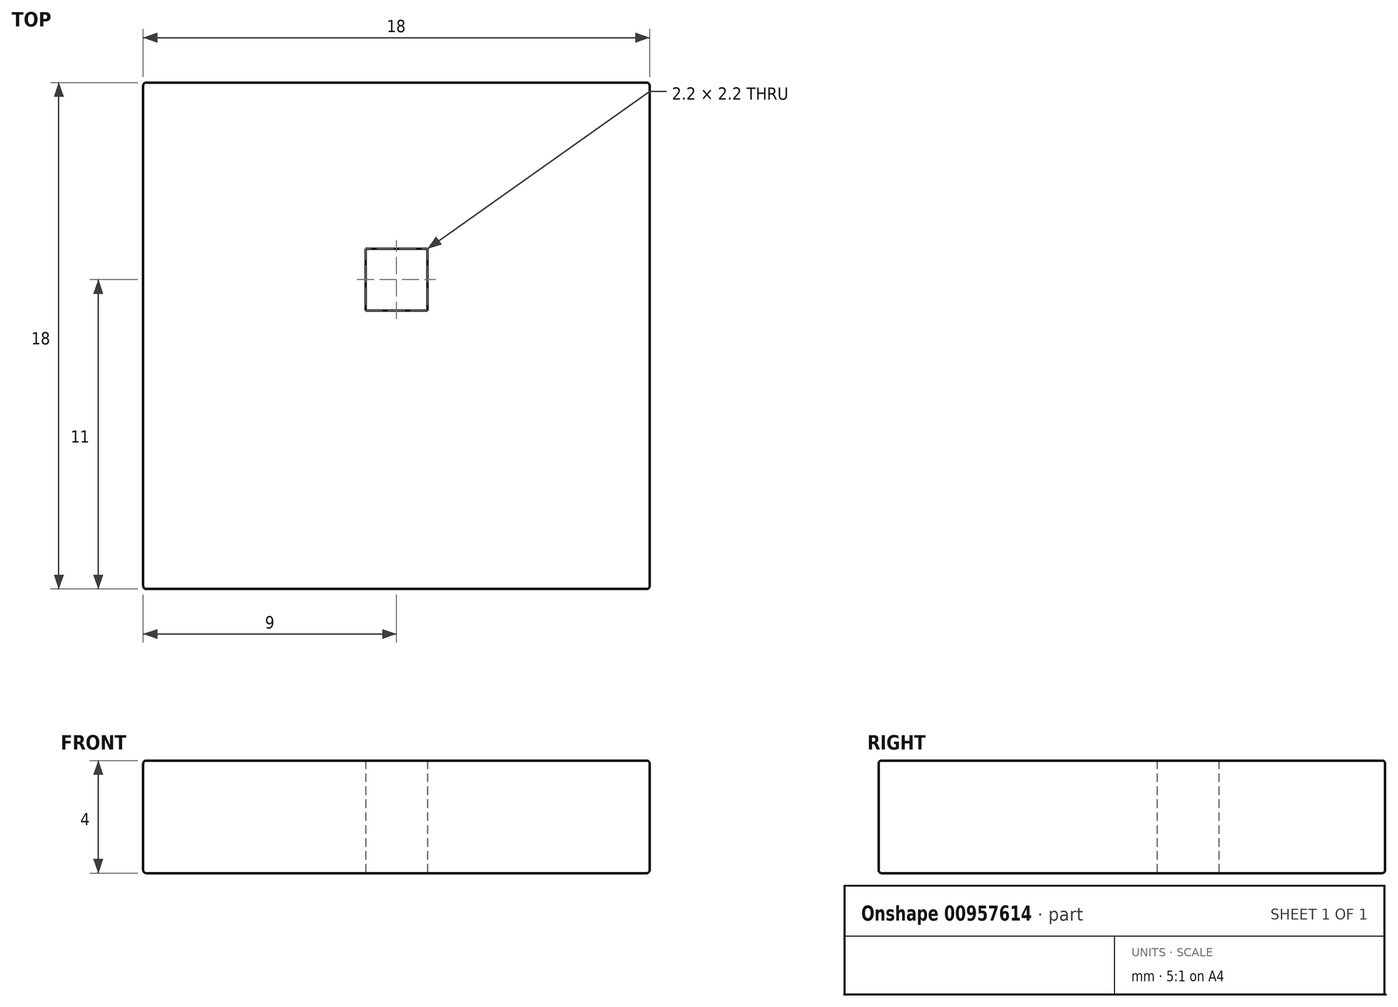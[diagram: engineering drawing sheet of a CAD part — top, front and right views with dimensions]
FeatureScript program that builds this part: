
annotation { "Feature Type Name" : "Feature", "Feature Type Description" : "" }
export const myFeature = defineFeature(function(context is Context, id is Id, definition is map)
    precondition{}
    {
        {
            var Q0;
            Q0=qCreatedBy(makeId("Top.planeOp"),FACE);
            var sketch = newSketch(context, id + "F0", { "sketchPlane" : qUnion([Q0])});
            skLineSegment(sketch, "E0.bottom", {"start": v(-9, 9) * mm, "end": v(9, 9) * mm});
            skLineSegment(sketch, "E0.top", {"start": v(-9, -9) * mm, "end": v(9, -9) * mm});
            skLineSegment(sketch, "E0.left", {"start": v(-9, 9) * mm, "end": v(-9, -9) * mm});
            skLineSegment(sketch, "E0.right", {"start": v(9, 9) * mm, "end": v(9, -9) * mm});
            skPoint(sketch, "E0.middle", {"position": v(0, 0) * mm});
            skLineSegment(sketch, "E1", {"start": v(-8, 9) * mm, "end": v(-8, -9) * mm});
            skLineSegment(sketch, "E2", {"start": v(-7.1, 9) * mm, "end": v(-7.1, -9) * mm});
            skLineSegment(sketch, "E3", {"start": v(-6.9, 9) * mm, "end": v(-6.9, -9) * mm});
            skLineSegment(sketch, "E4", {"start": v(-5.1, 9) * mm, "end": v(-5.1, -9) * mm});
            skLineSegment(sketch, "E5", {"start": v(-4.9, 9) * mm, "end": v(-4.9, -9) * mm});
            skLineSegment(sketch, "E6", {"start": v(-3.1, 9) * mm, "end": v(-3.1, -9) * mm});
            skLineSegment(sketch, "E7", {"start": v(-2.9, 9) * mm, "end": v(-2.9, -9) * mm});
            skLineSegment(sketch, "E8", {"start": v(-1.1, 9) * mm, "end": v(-1.1, -9) * mm});
            skLineSegment(sketch, "E9", {"start": v(-0.9, 9) * mm, "end": v(-0.9, -9) * mm});
            skLineSegment(sketch, "E10", {"start": v(0.9, 9) * mm, "end": v(0.9, -9) * mm});
            skLineSegment(sketch, "E11", {"start": v(1.1, 9) * mm, "end": v(1.1, -9) * mm});
            skLineSegment(sketch, "E12", {"start": v(2.9, 9) * mm, "end": v(2.9, -9) * mm});
            skLineSegment(sketch, "E13", {"start": v(3.1, 9) * mm, "end": v(3.1, -9) * mm});
            skLineSegment(sketch, "E14", {"start": v(4.9, 9) * mm, "end": v(4.9, -9) * mm});
            skLineSegment(sketch, "E15", {"start": v(5.1, 9) * mm, "end": v(5.1, -9) * mm});
            skLineSegment(sketch, "E16", {"start": v(6.9, 9) * mm, "end": v(6.9, -9) * mm});
            skLineSegment(sketch, "E17", {"start": v(7.1, 9) * mm, "end": v(7.1, -9) * mm});
            skLineSegment(sketch, "E18", {"start": v(8, 9) * mm, "end": v(8, -9) * mm});
            skLineSegment(sketch, "E19", {"start": v(9, 8) * mm, "end": v(-9, 8) * mm});
            skLineSegment(sketch, "E20", {"start": v(9, 7.1) * mm, "end": v(-9, 7.1) * mm});
            skLineSegment(sketch, "E21", {"start": v(9, 6.9) * mm, "end": v(-9, 6.9) * mm});
            skLineSegment(sketch, "E22", {"start": v(9, 5.1) * mm, "end": v(-9, 5.1) * mm});
            skLineSegment(sketch, "E23", {"start": v(9, 4.9) * mm, "end": v(-9, 4.9) * mm});
            skLineSegment(sketch, "E24", {"start": v(9, 3.1) * mm, "end": v(-9, 3.1) * mm});
            skLineSegment(sketch, "E25", {"start": v(9, 2.9) * mm, "end": v(-9, 2.9) * mm});
            skLineSegment(sketch, "E26", {"start": v(9, 1.1) * mm, "end": v(-9, 1.1) * mm});
            skLineSegment(sketch, "E27", {"start": v(9, 0.9) * mm, "end": v(-9, 0.9) * mm});
            skLineSegment(sketch, "E28", {"start": v(9, -0.9) * mm, "end": v(-9, -0.9) * mm});
            skLineSegment(sketch, "E29", {"start": v(9, -1.1) * mm, "end": v(-9, -1.1) * mm});
            skLineSegment(sketch, "E30", {"start": v(9, -2.9) * mm, "end": v(-9, -2.9) * mm});
            skLineSegment(sketch, "E31", {"start": v(9, -3.1) * mm, "end": v(-9, -3.1) * mm});
            skLineSegment(sketch, "E32", {"start": v(9, -4.9) * mm, "end": v(-9, -4.9) * mm});
            skLineSegment(sketch, "E33", {"start": v(9, -5.1) * mm, "end": v(-9, -5.1) * mm});
            skLineSegment(sketch, "E34", {"start": v(9, -6.9) * mm, "end": v(-9, -6.9) * mm});
            skLineSegment(sketch, "E35", {"start": v(9, -7.1) * mm, "end": v(-9, -7.1) * mm});
            skLineSegment(sketch, "E36", {"start": v(9, -8) * mm, "end": v(-9, -8) * mm});
            skSolve(sketch);
        }
        {
            var Q0;
            {var subQ0=sQuery(id+"F0.wireOp",EDGE,"E30");var subQ1=sQuery(id+"F0.wireOp",EDGE,"E10");var subQ2=makeQuery(id+"F0.imprint","INTERSECT",VERTEX,{"derivedFrom":[subQ1,subQ0]});Q0=makeQuery(id+"F0.imprint","IMPRINT",FACE,{"disambiguationData":[TD([[makeQuery(id+"F0.imprint","IMPRINT",EDGE,{"disambiguationData":[TD([[subQ2,-1.0]])],"derivedFrom":subQ1}),1.0]])]});}
            var Q1;
            {var subQ0=sQuery(id+"F0.wireOp",EDGE,"E26");var subQ1=sQuery(id+"F0.wireOp",EDGE,"E11");var subQ2=makeQuery(id+"F0.imprint","INTERSECT",VERTEX,{"derivedFrom":[subQ1,subQ0]});Q1=makeQuery(id+"F0.imprint","IMPRINT",FACE,{"disambiguationData":[TD([[makeQuery(id+"F0.imprint","IMPRINT",EDGE,{"disambiguationData":[TD([[subQ2,-1.0]])],"derivedFrom":subQ1}),1.0]])]});}
            var Q2;
            {var subQ0=sQuery(id+"F0.wireOp",EDGE,"E30");var subQ1=sQuery(id+"F0.wireOp",EDGE,"E15");var subQ2=makeQuery(id+"F0.imprint","INTERSECT",VERTEX,{"derivedFrom":[subQ1,subQ0]});Q2=makeQuery(id+"F0.imprint","IMPRINT",FACE,{"disambiguationData":[TD([[makeQuery(id+"F0.imprint","IMPRINT",EDGE,{"disambiguationData":[TD([[subQ2,-1.0]])],"derivedFrom":subQ1}),1.0]])]});}
            var Q3;
            {var subQ0=sQuery(id+"F0.wireOp",EDGE,"E35");var subQ1=sQuery(id+"F0.wireOp",EDGE,"E12");var subQ2=makeQuery(id+"F0.imprint","INTERSECT",VERTEX,{"derivedFrom":[subQ1,subQ0]});Q3=makeQuery(id+"F0.imprint","IMPRINT",FACE,{"disambiguationData":[TD([[makeQuery(id+"F0.imprint","IMPRINT",EDGE,{"disambiguationData":[TD([[subQ2,-1.0]])],"derivedFrom":subQ1}),1.0]])]});}
            var Q4;
            {var subQ0=sQuery(id+"F0.wireOp",EDGE,"E35");var subQ1=sQuery(id+"F0.wireOp",EDGE,"E14");var subQ2=makeQuery(id+"F0.imprint","INTERSECT",VERTEX,{"derivedFrom":[subQ1,subQ0]});Q4=makeQuery(id+"F0.imprint","IMPRINT",FACE,{"disambiguationData":[TD([[makeQuery(id+"F0.imprint","IMPRINT",EDGE,{"disambiguationData":[TD([[subQ2,-1.0]])],"derivedFrom":subQ1}),1.0]])]});}
            var Q5;
            {var subQ0=sQuery(id+"F0.wireOp",EDGE,"E32");var subQ1=sQuery(id+"F0.wireOp",EDGE,"E10");var subQ2=makeQuery(id+"F0.imprint","INTERSECT",VERTEX,{"derivedFrom":[subQ1,subQ0]});Q5=makeQuery(id+"F0.imprint","IMPRINT",FACE,{"disambiguationData":[TD([[makeQuery(id+"F0.imprint","IMPRINT",EDGE,{"disambiguationData":[TD([[subQ2,-1.0]])],"derivedFrom":subQ1}),1.0]])]});}
            var Q6;
            {var subQ0=sQuery(id+"F0.wireOp",EDGE,"E23");var subQ1=sQuery(id+"F0.wireOp",EDGE,"E14");var subQ2=makeQuery(id+"F0.imprint","INTERSECT",VERTEX,{"derivedFrom":[subQ1,subQ0]});Q6=makeQuery(id+"F0.imprint","IMPRINT",FACE,{"disambiguationData":[TD([[makeQuery(id+"F0.imprint","IMPRINT",EDGE,{"disambiguationData":[TD([[subQ2,-1.0]])],"derivedFrom":subQ1}),1.0]])]});}
            var Q7;
            {var subQ0=sQuery(id+"F0.wireOp",EDGE,"E23");var subQ1=sQuery(id+"F0.wireOp",EDGE,"E16");var subQ2=makeQuery(id+"F0.imprint","INTERSECT",VERTEX,{"derivedFrom":[subQ1,subQ0]});Q7=makeQuery(id+"F0.imprint","IMPRINT",FACE,{"disambiguationData":[TD([[makeQuery(id+"F0.imprint","IMPRINT",EDGE,{"disambiguationData":[TD([[subQ2,-1.0]])],"derivedFrom":subQ1}),1.0]])]});}
            var Q8;
            {var subQ0=sQuery(id+"F0.wireOp",EDGE,"E27");var subQ1=sQuery(id+"F0.wireOp",EDGE,"E10");var subQ2=makeQuery(id+"F0.imprint","INTERSECT",VERTEX,{"derivedFrom":[subQ1,subQ0]});Q8=makeQuery(id+"F0.imprint","IMPRINT",FACE,{"disambiguationData":[TD([[makeQuery(id+"F0.imprint","IMPRINT",EDGE,{"disambiguationData":[TD([[subQ2,-1.0]])],"derivedFrom":subQ1}),1.0]])]});}
            var Q9;
            {var subQ0=sQuery(id+"F0.wireOp",EDGE,"E31");var subQ1=sQuery(id+"F0.wireOp",EDGE,"E2");var subQ2=makeQuery(id+"F0.imprint","INTERSECT",VERTEX,{"derivedFrom":[subQ1,subQ0]});Q9=makeQuery(id+"F0.imprint","IMPRINT",FACE,{"disambiguationData":[TD([[makeQuery(id+"F0.imprint","IMPRINT",EDGE,{"disambiguationData":[TD([[subQ2,-1.0]])],"derivedFrom":subQ1}),1.0]])]});}
            var Q10;
            {var subQ0=sQuery(id+"F0.wireOp",EDGE,"E30");var subQ1=sQuery(id+"F0.wireOp",EDGE,"E13");var subQ2=makeQuery(id+"F0.imprint","INTERSECT",VERTEX,{"derivedFrom":[subQ1,subQ0]});Q10=makeQuery(id+"F0.imprint","IMPRINT",FACE,{"disambiguationData":[TD([[makeQuery(id+"F0.imprint","IMPRINT",EDGE,{"disambiguationData":[TD([[subQ2,-1.0]])],"derivedFrom":subQ1}),1.0]])]});}
            var Q11;
            {var subQ0=sQuery(id+"F0.wireOp",EDGE,"E33");var subQ1=sQuery(id+"F0.wireOp",EDGE,"E16");var subQ2=makeQuery(id+"F0.imprint","INTERSECT",VERTEX,{"derivedFrom":[subQ1,subQ0]});Q11=makeQuery(id+"F0.imprint","IMPRINT",FACE,{"disambiguationData":[TD([[makeQuery(id+"F0.imprint","IMPRINT",EDGE,{"disambiguationData":[TD([[subQ2,-1.0]])],"derivedFrom":subQ1}),1.0]])]});}
            var Q12;
            {var subQ0=sQuery(id+"F0.wireOp",EDGE,"E29");var subQ1=sQuery(id+"F0.wireOp",EDGE,"E8");var subQ2=makeQuery(id+"F0.imprint","INTERSECT",VERTEX,{"derivedFrom":[subQ1,subQ0]});Q12=makeQuery(id+"F0.imprint","IMPRINT",FACE,{"disambiguationData":[TD([[makeQuery(id+"F0.imprint","IMPRINT",EDGE,{"disambiguationData":[TD([[subQ2,-1.0]])],"derivedFrom":subQ1}),1.0]])]});}
            var Q13;
            {var subQ0=sQuery(id+"F0.wireOp",EDGE,"E26");var subQ1=sQuery(id+"F0.wireOp",EDGE,"E1");var subQ2=makeQuery(id+"F0.imprint","INTERSECT",VERTEX,{"derivedFrom":[subQ1,subQ0]});Q13=makeQuery(id+"F0.imprint","IMPRINT",FACE,{"disambiguationData":[TD([[makeQuery(id+"F0.imprint","IMPRINT",EDGE,{"disambiguationData":[TD([[subQ2,-1.0]])],"derivedFrom":subQ1}),1.0]])]});}
            var Q14;
            {var subQ0=sQuery(id+"F0.wireOp",EDGE,"E30");var subQ1=sQuery(id+"F0.wireOp",EDGE,"E12");var subQ2=makeQuery(id+"F0.imprint","INTERSECT",VERTEX,{"derivedFrom":[subQ1,subQ0]});Q14=makeQuery(id+"F0.imprint","IMPRINT",FACE,{"disambiguationData":[TD([[makeQuery(id+"F0.imprint","IMPRINT",EDGE,{"disambiguationData":[TD([[subQ2,-1.0]])],"derivedFrom":subQ1}),1.0]])]});}
            var Q15;
            {var subQ0=sQuery(id+"F0.wireOp",EDGE,"E29");var subQ1=sQuery(id+"F0.wireOp",EDGE,"E12");var subQ2=makeQuery(id+"F0.imprint","INTERSECT",VERTEX,{"derivedFrom":[subQ1,subQ0]});Q15=makeQuery(id+"F0.imprint","IMPRINT",FACE,{"disambiguationData":[TD([[makeQuery(id+"F0.imprint","IMPRINT",EDGE,{"disambiguationData":[TD([[subQ2,-1.0]])],"derivedFrom":subQ1}),1.0]])]});}
            var Q16;
            {var subQ0=sQuery(id+"F0.wireOp",EDGE,"E31");var subQ1=sQuery(id+"F0.wireOp",EDGE,"E6");var subQ2=makeQuery(id+"F0.imprint","INTERSECT",VERTEX,{"derivedFrom":[subQ1,subQ0]});Q16=makeQuery(id+"F0.imprint","IMPRINT",FACE,{"disambiguationData":[TD([[makeQuery(id+"F0.imprint","IMPRINT",EDGE,{"disambiguationData":[TD([[subQ2,-1.0]])],"derivedFrom":subQ1}),1.0]])]});}
            var Q17;
            {var subQ0=sQuery(id+"F0.wireOp",EDGE,"E29");var subQ1=sQuery(id+"F0.wireOp",EDGE,"E10");var subQ2=makeQuery(id+"F0.imprint","INTERSECT",VERTEX,{"derivedFrom":[subQ1,subQ0]});Q17=makeQuery(id+"F0.imprint","IMPRINT",FACE,{"disambiguationData":[TD([[makeQuery(id+"F0.imprint","IMPRINT",EDGE,{"disambiguationData":[TD([[subQ2,-1.0]])],"derivedFrom":subQ1}),1.0]])]});}
            var Q18;
            {var subQ0=sQuery(id+"F0.wireOp",EDGE,"E25");var subQ1=sQuery(id+"F0.wireOp",EDGE,"E16");var subQ2=makeQuery(id+"F0.imprint","INTERSECT",VERTEX,{"derivedFrom":[subQ1,subQ0]});Q18=makeQuery(id+"F0.imprint","IMPRINT",FACE,{"disambiguationData":[TD([[makeQuery(id+"F0.imprint","IMPRINT",EDGE,{"disambiguationData":[TD([[subQ2,-1.0]])],"derivedFrom":subQ1}),1.0]])]});}
            var Q19;
            {var subQ0=sQuery(id+"F0.wireOp",EDGE,"E35");var subQ1=sQuery(id+"F0.wireOp",EDGE,"E16");var subQ2=makeQuery(id+"F0.imprint","INTERSECT",VERTEX,{"derivedFrom":[subQ1,subQ0]});Q19=makeQuery(id+"F0.imprint","IMPRINT",FACE,{"disambiguationData":[TD([[makeQuery(id+"F0.imprint","IMPRINT",EDGE,{"disambiguationData":[TD([[subQ2,-1.0]])],"derivedFrom":subQ1}),1.0]])]});}
            var Q20;
            {var subQ0=sQuery(id+"F0.wireOp",EDGE,"E31");var subQ1=sQuery(id+"F0.wireOp",EDGE,"E12");var subQ2=makeQuery(id+"F0.imprint","INTERSECT",VERTEX,{"derivedFrom":[subQ1,subQ0]});Q20=makeQuery(id+"F0.imprint","IMPRINT",FACE,{"disambiguationData":[TD([[makeQuery(id+"F0.imprint","IMPRINT",EDGE,{"disambiguationData":[TD([[subQ2,-1.0]])],"derivedFrom":subQ1}),1.0]])]});}
            var Q21;
            {var subQ0=sQuery(id+"F0.wireOp",EDGE,"E24");var subQ1=sQuery(id+"F0.wireOp",EDGE,"E1");var subQ2=makeQuery(id+"F0.imprint","INTERSECT",VERTEX,{"derivedFrom":[subQ1,subQ0]});Q21=makeQuery(id+"F0.imprint","IMPRINT",FACE,{"disambiguationData":[TD([[makeQuery(id+"F0.imprint","IMPRINT",EDGE,{"disambiguationData":[TD([[subQ2,-1.0]])],"derivedFrom":subQ1}),1.0]])]});}
            var Q22;
            {var subQ0=sQuery(id+"F0.wireOp",EDGE,"E27");var subQ1=sQuery(id+"F0.wireOp",EDGE,"E16");var subQ2=makeQuery(id+"F0.imprint","INTERSECT",VERTEX,{"derivedFrom":[subQ1,subQ0]});Q22=makeQuery(id+"F0.imprint","IMPRINT",FACE,{"disambiguationData":[TD([[makeQuery(id+"F0.imprint","IMPRINT",EDGE,{"disambiguationData":[TD([[subQ2,-1.0]])],"derivedFrom":subQ1}),1.0]])]});}
            var Q23;
            {var subQ0=sQuery(id+"F0.wireOp",EDGE,"E35");var subQ1=sQuery(id+"F0.wireOp",EDGE,"E2");var subQ2=makeQuery(id+"F0.imprint","INTERSECT",VERTEX,{"derivedFrom":[subQ1,subQ0]});Q23=makeQuery(id+"F0.imprint","IMPRINT",FACE,{"disambiguationData":[TD([[makeQuery(id+"F0.imprint","IMPRINT",EDGE,{"disambiguationData":[TD([[subQ2,-1.0]])],"derivedFrom":subQ1}),1.0]])]});}
            var Q24;
            {var subQ0=sQuery(id+"F0.wireOp",EDGE,"E22");var subQ1=sQuery(id+"F0.wireOp",EDGE,"E16");var subQ2=makeQuery(id+"F0.imprint","INTERSECT",VERTEX,{"derivedFrom":[subQ1,subQ0]});Q24=makeQuery(id+"F0.imprint","IMPRINT",FACE,{"disambiguationData":[TD([[makeQuery(id+"F0.imprint","IMPRINT",EDGE,{"disambiguationData":[TD([[subQ2,-1.0]])],"derivedFrom":subQ1}),1.0]])]});}
            var Q25;
            {var subQ0=sQuery(id+"F0.wireOp",EDGE,"E35");var subQ1=sQuery(id+"F0.wireOp",EDGE,"E8");var subQ2=makeQuery(id+"F0.imprint","INTERSECT",VERTEX,{"derivedFrom":[subQ1,subQ0]});Q25=makeQuery(id+"F0.imprint","IMPRINT",FACE,{"disambiguationData":[TD([[makeQuery(id+"F0.imprint","IMPRINT",EDGE,{"disambiguationData":[TD([[subQ2,-1.0]])],"derivedFrom":subQ1}),1.0]])]});}
            var Q26;
            {var subQ0=sQuery(id+"F0.wireOp",EDGE,"E24");var subQ1=sQuery(id+"F0.wireOp",EDGE,"E7");var subQ2=makeQuery(id+"F0.imprint","INTERSECT",VERTEX,{"derivedFrom":[subQ1,subQ0]});Q26=makeQuery(id+"F0.imprint","IMPRINT",FACE,{"disambiguationData":[TD([[makeQuery(id+"F0.imprint","IMPRINT",EDGE,{"disambiguationData":[TD([[subQ2,-1.0]])],"derivedFrom":subQ1}),1.0]])]});}
            var Q27;
            {var subQ0=sQuery(id+"F0.wireOp",EDGE,"E21");var subQ1=sQuery(id+"F0.wireOp",EDGE,"E16");var subQ2=makeQuery(id+"F0.imprint","INTERSECT",VERTEX,{"derivedFrom":[subQ1,subQ0]});Q27=makeQuery(id+"F0.imprint","IMPRINT",FACE,{"disambiguationData":[TD([[makeQuery(id+"F0.imprint","IMPRINT",EDGE,{"disambiguationData":[TD([[subQ2,-1.0]])],"derivedFrom":subQ1}),1.0]])]});}
            var Q28;
            {var subQ0=sQuery(id+"F0.wireOp",EDGE,"E32");var subQ1=sQuery(id+"F0.wireOp",EDGE,"E11");var subQ2=makeQuery(id+"F0.imprint","INTERSECT",VERTEX,{"derivedFrom":[subQ1,subQ0]});Q28=makeQuery(id+"F0.imprint","IMPRINT",FACE,{"disambiguationData":[TD([[makeQuery(id+"F0.imprint","IMPRINT",EDGE,{"disambiguationData":[TD([[subQ2,-1.0]])],"derivedFrom":subQ1}),1.0]])]});}
            var Q29;
            {var subQ0=sQuery(id+"F0.wireOp",EDGE,"E33");var subQ1=sQuery(id+"F0.wireOp",EDGE,"E8");var subQ2=makeQuery(id+"F0.imprint","INTERSECT",VERTEX,{"derivedFrom":[subQ1,subQ0]});Q29=makeQuery(id+"F0.imprint","IMPRINT",FACE,{"disambiguationData":[TD([[makeQuery(id+"F0.imprint","IMPRINT",EDGE,{"disambiguationData":[TD([[subQ2,-1.0]])],"derivedFrom":subQ1}),1.0]])]});}
            var Q30;
            {var subQ0=sQuery(id+"F0.wireOp",EDGE,"E30");var subQ1=sQuery(id+"F0.wireOp",EDGE,"E9");var subQ2=makeQuery(id+"F0.imprint","INTERSECT",VERTEX,{"derivedFrom":[subQ1,subQ0]});Q30=makeQuery(id+"F0.imprint","IMPRINT",FACE,{"disambiguationData":[TD([[makeQuery(id+"F0.imprint","IMPRINT",EDGE,{"disambiguationData":[TD([[subQ2,-1.0]])],"derivedFrom":subQ1}),1.0]])]});}
            var Q31;
            {var subQ0=sQuery(id+"F0.wireOp",EDGE,"E27");var subQ1=sQuery(id+"F0.wireOp",EDGE,"E2");var subQ2=makeQuery(id+"F0.imprint","INTERSECT",VERTEX,{"derivedFrom":[subQ1,subQ0]});Q31=makeQuery(id+"F0.imprint","IMPRINT",FACE,{"disambiguationData":[TD([[makeQuery(id+"F0.imprint","IMPRINT",EDGE,{"disambiguationData":[TD([[subQ2,-1.0]])],"derivedFrom":subQ1}),1.0]])]});}
            var Q32;
            {var subQ0=sQuery(id+"F0.wireOp",EDGE,"E30");var subQ1=sQuery(id+"F0.wireOp",EDGE,"E11");var subQ2=makeQuery(id+"F0.imprint","INTERSECT",VERTEX,{"derivedFrom":[subQ1,subQ0]});Q32=makeQuery(id+"F0.imprint","IMPRINT",FACE,{"disambiguationData":[TD([[makeQuery(id+"F0.imprint","IMPRINT",EDGE,{"disambiguationData":[TD([[subQ2,-1.0]])],"derivedFrom":subQ1}),1.0]])]});}
            var Q33;
            {var subQ0=sQuery(id+"F0.wireOp",EDGE,"E26");var subQ1=sQuery(id+"F0.wireOp",EDGE,"E5");var subQ2=makeQuery(id+"F0.imprint","INTERSECT",VERTEX,{"derivedFrom":[subQ1,subQ0]});Q33=makeQuery(id+"F0.imprint","IMPRINT",FACE,{"disambiguationData":[TD([[makeQuery(id+"F0.imprint","IMPRINT",EDGE,{"disambiguationData":[TD([[subQ2,-1.0]])],"derivedFrom":subQ1}),1.0]])]});}
            var Q34;
            {var subQ0=sQuery(id+"F0.wireOp",EDGE,"E31");var subQ1=sQuery(id+"F0.wireOp",EDGE,"E8");var subQ2=makeQuery(id+"F0.imprint","INTERSECT",VERTEX,{"derivedFrom":[subQ1,subQ0]});Q34=makeQuery(id+"F0.imprint","IMPRINT",FACE,{"disambiguationData":[TD([[makeQuery(id+"F0.imprint","IMPRINT",EDGE,{"disambiguationData":[TD([[subQ2,-1.0]])],"derivedFrom":subQ1}),1.0]])]});}
            var Q35;
            {var subQ0=sQuery(id+"F0.wireOp",EDGE,"E32");var subQ1=sQuery(id+"F0.wireOp",EDGE,"E7");var subQ2=makeQuery(id+"F0.imprint","INTERSECT",VERTEX,{"derivedFrom":[subQ1,subQ0]});Q35=makeQuery(id+"F0.imprint","IMPRINT",FACE,{"disambiguationData":[TD([[makeQuery(id+"F0.imprint","IMPRINT",EDGE,{"disambiguationData":[TD([[subQ2,-1.0]])],"derivedFrom":subQ1}),1.0]])]});}
            var Q36;
            {var subQ0=sQuery(id+"F0.wireOp",EDGE,"E24");var subQ1=sQuery(id+"F0.wireOp",EDGE,"E17");var subQ2=makeQuery(id+"F0.imprint","INTERSECT",VERTEX,{"derivedFrom":[subQ1,subQ0]});Q36=makeQuery(id+"F0.imprint","IMPRINT",FACE,{"disambiguationData":[TD([[makeQuery(id+"F0.imprint","IMPRINT",EDGE,{"disambiguationData":[TD([[subQ2,-1.0]])],"derivedFrom":subQ1}),1.0]])]});}
            var Q37;
            {var subQ0=sQuery(id+"F0.wireOp",EDGE,"E26");var subQ1=sQuery(id+"F0.wireOp",EDGE,"E14");var subQ2=makeQuery(id+"F0.imprint","INTERSECT",VERTEX,{"derivedFrom":[subQ1,subQ0]});Q37=makeQuery(id+"F0.imprint","IMPRINT",FACE,{"disambiguationData":[TD([[makeQuery(id+"F0.imprint","IMPRINT",EDGE,{"disambiguationData":[TD([[subQ2,-1.0]])],"derivedFrom":subQ1}),1.0]])]});}
            var Q38;
            {var subQ0=sQuery(id+"F0.wireOp",EDGE,"E31");var subQ1=sQuery(id+"F0.wireOp",EDGE,"E14");var subQ2=makeQuery(id+"F0.imprint","INTERSECT",VERTEX,{"derivedFrom":[subQ1,subQ0]});Q38=makeQuery(id+"F0.imprint","IMPRINT",FACE,{"disambiguationData":[TD([[makeQuery(id+"F0.imprint","IMPRINT",EDGE,{"disambiguationData":[TD([[subQ2,-1.0]])],"derivedFrom":subQ1}),1.0]])]});}
            var Q39;
            {var subQ0=sQuery(id+"F0.wireOp",EDGE,"E24");var subQ1=sQuery(id+"F0.wireOp",EDGE,"E5");var subQ2=makeQuery(id+"F0.imprint","INTERSECT",VERTEX,{"derivedFrom":[subQ1,subQ0]});Q39=makeQuery(id+"F0.imprint","IMPRINT",FACE,{"disambiguationData":[TD([[makeQuery(id+"F0.imprint","IMPRINT",EDGE,{"disambiguationData":[TD([[subQ2,-1.0]])],"derivedFrom":subQ1}),1.0]])]});}
            var Q40;
            {var subQ0=sQuery(id+"F0.wireOp",EDGE,"E26");var subQ1=sQuery(id+"F0.wireOp",EDGE,"E12");var subQ2=makeQuery(id+"F0.imprint","INTERSECT",VERTEX,{"derivedFrom":[subQ1,subQ0]});Q40=makeQuery(id+"F0.imprint","IMPRINT",FACE,{"disambiguationData":[TD([[makeQuery(id+"F0.imprint","IMPRINT",EDGE,{"disambiguationData":[TD([[subQ2,-1.0]])],"derivedFrom":subQ1}),1.0]])]});}
            var Q41;
            {var subQ0=sQuery(id+"F0.wireOp",EDGE,"E30");var subQ1=sQuery(id+"F0.wireOp",EDGE,"E5");var subQ2=makeQuery(id+"F0.imprint","INTERSECT",VERTEX,{"derivedFrom":[subQ1,subQ0]});Q41=makeQuery(id+"F0.imprint","IMPRINT",FACE,{"disambiguationData":[TD([[makeQuery(id+"F0.imprint","IMPRINT",EDGE,{"disambiguationData":[TD([[subQ2,-1.0]])],"derivedFrom":subQ1}),1.0]])]});}
            var Q42;
            {var subQ0=sQuery(id+"F0.wireOp",EDGE,"E33");var subQ1=sQuery(id+"F0.wireOp",EDGE,"E14");var subQ2=makeQuery(id+"F0.imprint","INTERSECT",VERTEX,{"derivedFrom":[subQ1,subQ0]});Q42=makeQuery(id+"F0.imprint","IMPRINT",FACE,{"disambiguationData":[TD([[makeQuery(id+"F0.imprint","IMPRINT",EDGE,{"disambiguationData":[TD([[subQ2,-1.0]])],"derivedFrom":subQ1}),1.0]])]});}
            var Q43;
            {var subQ0=sQuery(id+"F0.wireOp",EDGE,"E32");var subQ1=sQuery(id+"F0.wireOp",EDGE,"E9");var subQ2=makeQuery(id+"F0.imprint","INTERSECT",VERTEX,{"derivedFrom":[subQ1,subQ0]});Q43=makeQuery(id+"F0.imprint","IMPRINT",FACE,{"disambiguationData":[TD([[makeQuery(id+"F0.imprint","IMPRINT",EDGE,{"disambiguationData":[TD([[subQ2,-1.0]])],"derivedFrom":subQ1}),1.0]])]});}
            var Q44;
            {var subQ0=sQuery(id+"F0.wireOp",EDGE,"E25");var subQ1=sQuery(id+"F0.wireOp",EDGE,"E6");var subQ2=makeQuery(id+"F0.imprint","INTERSECT",VERTEX,{"derivedFrom":[subQ1,subQ0]});Q44=makeQuery(id+"F0.imprint","IMPRINT",FACE,{"disambiguationData":[TD([[makeQuery(id+"F0.imprint","IMPRINT",EDGE,{"disambiguationData":[TD([[subQ2,-1.0]])],"derivedFrom":subQ1}),1.0]])]});}
            var Q45;
            {var subQ0=sQuery(id+"F0.wireOp",EDGE,"E19");var subQ1=sQuery(id+"F0.wireOp",EDGE,"E16");var subQ2=makeQuery(id+"F0.imprint","INTERSECT",VERTEX,{"derivedFrom":[subQ1,subQ0]});Q45=makeQuery(id+"F0.imprint","IMPRINT",FACE,{"disambiguationData":[TD([[makeQuery(id+"F0.imprint","IMPRINT",EDGE,{"disambiguationData":[TD([[subQ2,-1.0]])],"derivedFrom":subQ1}),1.0]])]});}
            var Q46;
            {var subQ0=sQuery(id+"F0.wireOp",EDGE,"E19");var subQ1=sQuery(id+"F0.wireOp",EDGE,"E10");var subQ2=makeQuery(id+"F0.imprint","INTERSECT",VERTEX,{"derivedFrom":[subQ1,subQ0]});Q46=makeQuery(id+"F0.imprint","IMPRINT",FACE,{"disambiguationData":[TD([[makeQuery(id+"F0.imprint","IMPRINT",EDGE,{"disambiguationData":[TD([[subQ2,-1.0]])],"derivedFrom":subQ1}),1.0]])]});}
            var Q47;
            {var subQ0=sQuery(id+"F0.wireOp",EDGE,"E19");var subQ1=sQuery(id+"F0.wireOp",EDGE,"E2");var subQ2=makeQuery(id+"F0.imprint","INTERSECT",VERTEX,{"derivedFrom":[subQ1,subQ0]});Q47=makeQuery(id+"F0.imprint","IMPRINT",FACE,{"disambiguationData":[TD([[makeQuery(id+"F0.imprint","IMPRINT",EDGE,{"disambiguationData":[TD([[subQ2,-1.0]])],"derivedFrom":subQ1}),1.0]])]});}
            var Q48;
            {var subQ0=sQuery(id+"F0.wireOp",EDGE,"E32");var subQ1=sQuery(id+"F0.wireOp",EDGE,"E17");var subQ2=makeQuery(id+"F0.imprint","INTERSECT",VERTEX,{"derivedFrom":[subQ1,subQ0]});Q48=makeQuery(id+"F0.imprint","IMPRINT",FACE,{"disambiguationData":[TD([[makeQuery(id+"F0.imprint","IMPRINT",EDGE,{"disambiguationData":[TD([[subQ2,-1.0]])],"derivedFrom":subQ1}),1.0]])]});}
            var Q49;
            {var subQ0=sQuery(id+"F0.wireOp",EDGE,"E30");var subQ1=sQuery(id+"F0.wireOp",EDGE,"E17");var subQ2=makeQuery(id+"F0.imprint","INTERSECT",VERTEX,{"derivedFrom":[subQ1,subQ0]});Q49=makeQuery(id+"F0.imprint","IMPRINT",FACE,{"disambiguationData":[TD([[makeQuery(id+"F0.imprint","IMPRINT",EDGE,{"disambiguationData":[TD([[subQ2,-1.0]])],"derivedFrom":subQ1}),1.0]])]});}
            var Q50;
            {var subQ0=sQuery(id+"F0.wireOp",EDGE,"E33");var subQ1=sQuery(id+"F0.wireOp",EDGE,"E12");var subQ2=makeQuery(id+"F0.imprint","INTERSECT",VERTEX,{"derivedFrom":[subQ1,subQ0]});Q50=makeQuery(id+"F0.imprint","IMPRINT",FACE,{"disambiguationData":[TD([[makeQuery(id+"F0.imprint","IMPRINT",EDGE,{"disambiguationData":[TD([[subQ2,-1.0]])],"derivedFrom":subQ1}),1.0]])]});}
            var Q51;
            {var subQ0=sQuery(id+"F0.wireOp",EDGE,"E22");var subQ1=sQuery(id+"F0.wireOp",EDGE,"E13");var subQ2=makeQuery(id+"F0.imprint","INTERSECT",VERTEX,{"derivedFrom":[subQ1,subQ0]});Q51=makeQuery(id+"F0.imprint","IMPRINT",FACE,{"disambiguationData":[TD([[makeQuery(id+"F0.imprint","IMPRINT",EDGE,{"disambiguationData":[TD([[subQ2,-1.0]])],"derivedFrom":subQ1}),1.0]])]});}
            var Q52;
            {var subQ0=sQuery(id+"F0.wireOp",EDGE,"E19");var subQ1=sQuery(id+"F0.wireOp",EDGE,"E14");var subQ2=makeQuery(id+"F0.imprint","INTERSECT",VERTEX,{"derivedFrom":[subQ1,subQ0]});Q52=makeQuery(id+"F0.imprint","IMPRINT",FACE,{"disambiguationData":[TD([[makeQuery(id+"F0.imprint","IMPRINT",EDGE,{"disambiguationData":[TD([[subQ2,-1.0]])],"derivedFrom":subQ1}),1.0]])]});}
            var Q53;
            {var subQ0=sQuery(id+"F0.wireOp",EDGE,"E32");var subQ1=sQuery(id+"F0.wireOp",EDGE,"E16");var subQ2=makeQuery(id+"F0.imprint","INTERSECT",VERTEX,{"derivedFrom":[subQ1,subQ0]});Q53=makeQuery(id+"F0.imprint","IMPRINT",FACE,{"disambiguationData":[TD([[makeQuery(id+"F0.imprint","IMPRINT",EDGE,{"disambiguationData":[TD([[subQ2,-1.0]])],"derivedFrom":subQ1}),1.0]])]});}
            var Q54;
            {var subQ0=sQuery(id+"F0.wireOp",EDGE,"E32");var subQ1=sQuery(id+"F0.wireOp",EDGE,"E3");var subQ2=makeQuery(id+"F0.imprint","INTERSECT",VERTEX,{"derivedFrom":[subQ1,subQ0]});Q54=makeQuery(id+"F0.imprint","IMPRINT",FACE,{"disambiguationData":[TD([[makeQuery(id+"F0.imprint","IMPRINT",EDGE,{"disambiguationData":[TD([[subQ2,-1.0]])],"derivedFrom":subQ1}),1.0]])]});}
            var Q55;
            {var subQ0=sQuery(id+"F0.wireOp",EDGE,"E32");var subQ1=sQuery(id+"F0.wireOp",EDGE,"E6");var subQ2=makeQuery(id+"F0.imprint","INTERSECT",VERTEX,{"derivedFrom":[subQ1,subQ0]});Q55=makeQuery(id+"F0.imprint","IMPRINT",FACE,{"disambiguationData":[TD([[makeQuery(id+"F0.imprint","IMPRINT",EDGE,{"disambiguationData":[TD([[subQ2,-1.0]])],"derivedFrom":subQ1}),1.0]])]});}
            var Q56;
            {var subQ0=sQuery(id+"F0.wireOp",EDGE,"E35");var subQ1=sQuery(id+"F0.wireOp",EDGE,"E10");var subQ2=makeQuery(id+"F0.imprint","INTERSECT",VERTEX,{"derivedFrom":[subQ1,subQ0]});Q56=makeQuery(id+"F0.imprint","IMPRINT",FACE,{"disambiguationData":[TD([[makeQuery(id+"F0.imprint","IMPRINT",EDGE,{"disambiguationData":[TD([[subQ2,-1.0]])],"derivedFrom":subQ1}),1.0]])]});}
            var Q57;
            {var subQ0=sQuery(id+"F0.wireOp",EDGE,"E23");var subQ1=sQuery(id+"F0.wireOp",EDGE,"E12");var subQ2=makeQuery(id+"F0.imprint","INTERSECT",VERTEX,{"derivedFrom":[subQ1,subQ0]});Q57=makeQuery(id+"F0.imprint","IMPRINT",FACE,{"disambiguationData":[TD([[makeQuery(id+"F0.imprint","IMPRINT",EDGE,{"disambiguationData":[TD([[subQ2,-1.0]])],"derivedFrom":subQ1}),1.0]])]});}
            var Q58;
            {var subQ0=sQuery(id+"F0.wireOp",EDGE,"E32");var subQ1=sQuery(id+"F0.wireOp",EDGE,"E5");var subQ2=makeQuery(id+"F0.imprint","INTERSECT",VERTEX,{"derivedFrom":[subQ1,subQ0]});Q58=makeQuery(id+"F0.imprint","IMPRINT",FACE,{"disambiguationData":[TD([[makeQuery(id+"F0.imprint","IMPRINT",EDGE,{"disambiguationData":[TD([[subQ2,-1.0]])],"derivedFrom":subQ1}),1.0]])]});}
            var Q59;
            {var subQ0=sQuery(id+"F0.wireOp",EDGE,"E33");var subQ1=sQuery(id+"F0.wireOp",EDGE,"E6");var subQ2=makeQuery(id+"F0.imprint","INTERSECT",VERTEX,{"derivedFrom":[subQ1,subQ0]});Q59=makeQuery(id+"F0.imprint","IMPRINT",FACE,{"disambiguationData":[TD([[makeQuery(id+"F0.imprint","IMPRINT",EDGE,{"disambiguationData":[TD([[subQ2,-1.0]])],"derivedFrom":subQ1}),1.0]])]});}
            var Q60;
            {var subQ0=sQuery(id+"F0.wireOp",EDGE,"E30");var subQ1=sQuery(id+"F0.wireOp",EDGE,"E7");var subQ2=makeQuery(id+"F0.imprint","INTERSECT",VERTEX,{"derivedFrom":[subQ1,subQ0]});Q60=makeQuery(id+"F0.imprint","IMPRINT",FACE,{"disambiguationData":[TD([[makeQuery(id+"F0.imprint","IMPRINT",EDGE,{"disambiguationData":[TD([[subQ2,-1.0]])],"derivedFrom":subQ1}),1.0]])]});}
            var Q61;
            {var subQ0=sQuery(id+"F0.wireOp",EDGE,"E33");var subQ1=sQuery(id+"F0.wireOp",EDGE,"E10");var subQ2=makeQuery(id+"F0.imprint","INTERSECT",VERTEX,{"derivedFrom":[subQ1,subQ0]});Q61=makeQuery(id+"F0.imprint","IMPRINT",FACE,{"disambiguationData":[TD([[makeQuery(id+"F0.imprint","IMPRINT",EDGE,{"disambiguationData":[TD([[subQ2,-1.0]])],"derivedFrom":subQ1}),1.0]])]});}
            var Q62;
            {var subQ0=sQuery(id+"F0.wireOp",EDGE,"E30");var subQ1=sQuery(id+"F0.wireOp",EDGE,"E14");var subQ2=makeQuery(id+"F0.imprint","INTERSECT",VERTEX,{"derivedFrom":[subQ1,subQ0]});Q62=makeQuery(id+"F0.imprint","IMPRINT",FACE,{"disambiguationData":[TD([[makeQuery(id+"F0.imprint","IMPRINT",EDGE,{"disambiguationData":[TD([[subQ2,-1.0]])],"derivedFrom":subQ1}),1.0]])]});}
            var Q63;
            {var subQ0=sQuery(id+"F0.wireOp",EDGE,"E26");var subQ1=sQuery(id+"F0.wireOp",EDGE,"E13");var subQ2=makeQuery(id+"F0.imprint","INTERSECT",VERTEX,{"derivedFrom":[subQ1,subQ0]});Q63=makeQuery(id+"F0.imprint","IMPRINT",FACE,{"disambiguationData":[TD([[makeQuery(id+"F0.imprint","IMPRINT",EDGE,{"disambiguationData":[TD([[subQ2,-1.0]])],"derivedFrom":subQ1}),1.0]])]});}
            var Q64;
            {var subQ0=sQuery(id+"F0.wireOp",EDGE,"E26");var subQ1=sQuery(id+"F0.wireOp",EDGE,"E16");var subQ2=makeQuery(id+"F0.imprint","INTERSECT",VERTEX,{"derivedFrom":[subQ1,subQ0]});Q64=makeQuery(id+"F0.imprint","IMPRINT",FACE,{"disambiguationData":[TD([[makeQuery(id+"F0.imprint","IMPRINT",EDGE,{"disambiguationData":[TD([[subQ2,-1.0]])],"derivedFrom":subQ1}),1.0]])]});}
            var Q65;
            {var subQ0=sQuery(id+"F0.wireOp",EDGE,"E32");var subQ1=sQuery(id+"F0.wireOp",EDGE,"E14");var subQ2=makeQuery(id+"F0.imprint","INTERSECT",VERTEX,{"derivedFrom":[subQ1,subQ0]});Q65=makeQuery(id+"F0.imprint","IMPRINT",FACE,{"disambiguationData":[TD([[makeQuery(id+"F0.imprint","IMPRINT",EDGE,{"disambiguationData":[TD([[subQ2,-1.0]])],"derivedFrom":subQ1}),1.0]])]});}
            var Q66;
            {var subQ0=sQuery(id+"F0.wireOp",EDGE,"E24");var subQ1=sQuery(id+"F0.wireOp",EDGE,"E11");var subQ2=makeQuery(id+"F0.imprint","INTERSECT",VERTEX,{"derivedFrom":[subQ1,subQ0]});Q66=makeQuery(id+"F0.imprint","IMPRINT",FACE,{"disambiguationData":[TD([[makeQuery(id+"F0.imprint","IMPRINT",EDGE,{"disambiguationData":[TD([[subQ2,-1.0]])],"derivedFrom":subQ1}),1.0]])]});}
            var Q67;
            {var subQ0=sQuery(id+"F0.wireOp",EDGE,"E30");var subQ1=sQuery(id+"F0.wireOp",EDGE,"E3");var subQ2=makeQuery(id+"F0.imprint","INTERSECT",VERTEX,{"derivedFrom":[subQ1,subQ0]});Q67=makeQuery(id+"F0.imprint","IMPRINT",FACE,{"disambiguationData":[TD([[makeQuery(id+"F0.imprint","IMPRINT",EDGE,{"disambiguationData":[TD([[subQ2,-1.0]])],"derivedFrom":subQ1}),1.0]])]});}
            var Q68;
            {var subQ0=sQuery(id+"F0.wireOp",EDGE,"E22");var subQ1=sQuery(id+"F0.wireOp",EDGE,"E14");var subQ2=makeQuery(id+"F0.imprint","INTERSECT",VERTEX,{"derivedFrom":[subQ1,subQ0]});Q68=makeQuery(id+"F0.imprint","IMPRINT",FACE,{"disambiguationData":[TD([[makeQuery(id+"F0.imprint","IMPRINT",EDGE,{"disambiguationData":[TD([[subQ2,-1.0]])],"derivedFrom":subQ1}),1.0]])]});}
            var Q69;
            {var subQ0=sQuery(id+"F0.wireOp",EDGE,"E22");var subQ1=sQuery(id+"F0.wireOp",EDGE,"E15");var subQ2=makeQuery(id+"F0.imprint","INTERSECT",VERTEX,{"derivedFrom":[subQ1,subQ0]});Q69=makeQuery(id+"F0.imprint","IMPRINT",FACE,{"disambiguationData":[TD([[makeQuery(id+"F0.imprint","IMPRINT",EDGE,{"disambiguationData":[TD([[subQ2,-1.0]])],"derivedFrom":subQ1}),1.0]])]});}
            var Q70;
            {var subQ0=sQuery(id+"F0.wireOp",EDGE,"E29");var subQ1=sQuery(id+"F0.wireOp",EDGE,"E16");var subQ2=makeQuery(id+"F0.imprint","INTERSECT",VERTEX,{"derivedFrom":[subQ1,subQ0]});Q70=makeQuery(id+"F0.imprint","IMPRINT",FACE,{"disambiguationData":[TD([[makeQuery(id+"F0.imprint","IMPRINT",EDGE,{"disambiguationData":[TD([[subQ2,-1.0]])],"derivedFrom":subQ1}),1.0]])]});}
            var Q71;
            {var subQ0=sQuery(id+"F0.wireOp",EDGE,"E22");var subQ1=sQuery(id+"F0.wireOp",EDGE,"E17");var subQ2=makeQuery(id+"F0.imprint","INTERSECT",VERTEX,{"derivedFrom":[subQ1,subQ0]});Q71=makeQuery(id+"F0.imprint","IMPRINT",FACE,{"disambiguationData":[TD([[makeQuery(id+"F0.imprint","IMPRINT",EDGE,{"disambiguationData":[TD([[subQ2,-1.0]])],"derivedFrom":subQ1}),1.0]])]});}
            var Q72;
            {var subQ0=sQuery(id+"F0.wireOp",EDGE,"E30");var subQ1=sQuery(id+"F0.wireOp",EDGE,"E6");var subQ2=makeQuery(id+"F0.imprint","INTERSECT",VERTEX,{"derivedFrom":[subQ1,subQ0]});Q72=makeQuery(id+"F0.imprint","IMPRINT",FACE,{"disambiguationData":[TD([[makeQuery(id+"F0.imprint","IMPRINT",EDGE,{"disambiguationData":[TD([[subQ2,-1.0]])],"derivedFrom":subQ1}),1.0]])]});}
            var Q73;
            {var subQ0=sQuery(id+"F0.wireOp",EDGE,"E21");var subQ1=sQuery(id+"F0.wireOp",EDGE,"E10");var subQ2=makeQuery(id+"F0.imprint","INTERSECT",VERTEX,{"derivedFrom":[subQ1,subQ0]});Q73=makeQuery(id+"F0.imprint","IMPRINT",FACE,{"disambiguationData":[TD([[makeQuery(id+"F0.imprint","IMPRINT",EDGE,{"disambiguationData":[TD([[subQ2,-1.0]])],"derivedFrom":subQ1}),1.0]])]});}
            var Q74;
            {var subQ0=sQuery(id+"F0.wireOp",EDGE,"E24");var subQ1=sQuery(id+"F0.wireOp",EDGE,"E6");var subQ2=makeQuery(id+"F0.imprint","INTERSECT",VERTEX,{"derivedFrom":[subQ1,subQ0]});Q74=makeQuery(id+"F0.imprint","IMPRINT",FACE,{"disambiguationData":[TD([[makeQuery(id+"F0.imprint","IMPRINT",EDGE,{"disambiguationData":[TD([[subQ2,-1.0]])],"derivedFrom":subQ1}),1.0]])]});}
            var Q75;
            {var subQ0=sQuery(id+"F0.wireOp",EDGE,"E32");var subQ1=sQuery(id+"F0.wireOp",EDGE,"E1");var subQ2=makeQuery(id+"F0.imprint","INTERSECT",VERTEX,{"derivedFrom":[subQ1,subQ0]});Q75=makeQuery(id+"F0.imprint","IMPRINT",FACE,{"disambiguationData":[TD([[makeQuery(id+"F0.imprint","IMPRINT",EDGE,{"disambiguationData":[TD([[subQ2,-1.0]])],"derivedFrom":subQ1}),1.0]])]});}
            var Q76;
            {var subQ0=sQuery(id+"F0.wireOp",EDGE,"E24");var subQ1=sQuery(id+"F0.wireOp",EDGE,"E12");var subQ2=makeQuery(id+"F0.imprint","INTERSECT",VERTEX,{"derivedFrom":[subQ1,subQ0]});Q76=makeQuery(id+"F0.imprint","IMPRINT",FACE,{"disambiguationData":[TD([[makeQuery(id+"F0.imprint","IMPRINT",EDGE,{"disambiguationData":[TD([[subQ2,-1.0]])],"derivedFrom":subQ1}),1.0]])]});}
            var Q77;
            {var subQ0=sQuery(id+"F0.wireOp",EDGE,"E25");var subQ1=sQuery(id+"F0.wireOp",EDGE,"E14");var subQ2=makeQuery(id+"F0.imprint","INTERSECT",VERTEX,{"derivedFrom":[subQ1,subQ0]});Q77=makeQuery(id+"F0.imprint","IMPRINT",FACE,{"disambiguationData":[TD([[makeQuery(id+"F0.imprint","IMPRINT",EDGE,{"disambiguationData":[TD([[subQ2,-1.0]])],"derivedFrom":subQ1}),1.0]])]});}
            var Q78;
            {var subQ0=sQuery(id+"F0.wireOp",EDGE,"E26");var subQ1=sQuery(id+"F0.wireOp",EDGE,"E6");var subQ2=makeQuery(id+"F0.imprint","INTERSECT",VERTEX,{"derivedFrom":[subQ1,subQ0]});Q78=makeQuery(id+"F0.imprint","IMPRINT",FACE,{"disambiguationData":[TD([[makeQuery(id+"F0.imprint","IMPRINT",EDGE,{"disambiguationData":[TD([[subQ2,-1.0]])],"derivedFrom":subQ1}),1.0]])]});}
            var Q79;
            {var subQ0=sQuery(id+"F0.wireOp",EDGE,"E24");var subQ1=sQuery(id+"F0.wireOp",EDGE,"E13");var subQ2=makeQuery(id+"F0.imprint","INTERSECT",VERTEX,{"derivedFrom":[subQ1,subQ0]});Q79=makeQuery(id+"F0.imprint","IMPRINT",FACE,{"disambiguationData":[TD([[makeQuery(id+"F0.imprint","IMPRINT",EDGE,{"disambiguationData":[TD([[subQ2,-1.0]])],"derivedFrom":subQ1}),1.0]])]});}
            var Q80;
            {var subQ0=sQuery(id+"F0.wireOp",EDGE,"E31");var subQ1=sQuery(id+"F0.wireOp",EDGE,"E10");var subQ2=makeQuery(id+"F0.imprint","INTERSECT",VERTEX,{"derivedFrom":[subQ1,subQ0]});Q80=makeQuery(id+"F0.imprint","IMPRINT",FACE,{"disambiguationData":[TD([[makeQuery(id+"F0.imprint","IMPRINT",EDGE,{"disambiguationData":[TD([[subQ2,-1.0]])],"derivedFrom":subQ1}),1.0]])]});}
            var Q81;
            {var subQ0=sQuery(id+"F0.wireOp",EDGE,"E32");var subQ1=sQuery(id+"F0.wireOp",EDGE,"E12");var subQ2=makeQuery(id+"F0.imprint","INTERSECT",VERTEX,{"derivedFrom":[subQ1,subQ0]});Q81=makeQuery(id+"F0.imprint","IMPRINT",FACE,{"disambiguationData":[TD([[makeQuery(id+"F0.imprint","IMPRINT",EDGE,{"disambiguationData":[TD([[subQ2,-1.0]])],"derivedFrom":subQ1}),1.0]])]});}
            var Q82;
            {var subQ0=sQuery(id+"F0.wireOp",EDGE,"E23");var subQ1=sQuery(id+"F0.wireOp",EDGE,"E6");var subQ2=makeQuery(id+"F0.imprint","INTERSECT",VERTEX,{"derivedFrom":[subQ1,subQ0]});Q82=makeQuery(id+"F0.imprint","IMPRINT",FACE,{"disambiguationData":[TD([[makeQuery(id+"F0.imprint","IMPRINT",EDGE,{"disambiguationData":[TD([[subQ2,-1.0]])],"derivedFrom":subQ1}),1.0]])]});}
            var Q83;
            {var subQ0=sQuery(id+"F0.wireOp",EDGE,"E32");var subQ1=sQuery(id+"F0.wireOp",EDGE,"E8");var subQ2=makeQuery(id+"F0.imprint","INTERSECT",VERTEX,{"derivedFrom":[subQ1,subQ0]});Q83=makeQuery(id+"F0.imprint","IMPRINT",FACE,{"disambiguationData":[TD([[makeQuery(id+"F0.imprint","IMPRINT",EDGE,{"disambiguationData":[TD([[subQ2,-1.0]])],"derivedFrom":subQ1}),1.0]])]});}
            var Q84;
            {var subQ0=sQuery(id+"F0.wireOp",EDGE,"E27");var subQ1=sQuery(id+"F0.wireOp",EDGE,"E14");var subQ2=makeQuery(id+"F0.imprint","INTERSECT",VERTEX,{"derivedFrom":[subQ1,subQ0]});Q84=makeQuery(id+"F0.imprint","IMPRINT",FACE,{"disambiguationData":[TD([[makeQuery(id+"F0.imprint","IMPRINT",EDGE,{"disambiguationData":[TD([[subQ2,-1.0]])],"derivedFrom":subQ1}),1.0]])]});}
            var Q85;
            {var subQ0=sQuery(id+"F0.wireOp",EDGE,"E22");var subQ1=sQuery(id+"F0.wireOp",EDGE,"E1");var subQ2=makeQuery(id+"F0.imprint","INTERSECT",VERTEX,{"derivedFrom":[subQ1,subQ0]});Q85=makeQuery(id+"F0.imprint","IMPRINT",FACE,{"disambiguationData":[TD([[makeQuery(id+"F0.imprint","IMPRINT",EDGE,{"disambiguationData":[TD([[subQ2,-1.0]])],"derivedFrom":subQ1}),1.0]])]});}
            var Q86;
            {var subQ0=sQuery(id+"F0.wireOp",EDGE,"E26");var subQ1=sQuery(id+"F0.wireOp",EDGE,"E17");var subQ2=makeQuery(id+"F0.imprint","INTERSECT",VERTEX,{"derivedFrom":[subQ1,subQ0]});Q86=makeQuery(id+"F0.imprint","IMPRINT",FACE,{"disambiguationData":[TD([[makeQuery(id+"F0.imprint","IMPRINT",EDGE,{"disambiguationData":[TD([[subQ2,-1.0]])],"derivedFrom":subQ1}),1.0]])]});}
            var Q87;
            {var subQ0=sQuery(id+"F0.wireOp",EDGE,"E32");var subQ1=sQuery(id+"F0.wireOp",EDGE,"E15");var subQ2=makeQuery(id+"F0.imprint","INTERSECT",VERTEX,{"derivedFrom":[subQ1,subQ0]});Q87=makeQuery(id+"F0.imprint","IMPRINT",FACE,{"disambiguationData":[TD([[makeQuery(id+"F0.imprint","IMPRINT",EDGE,{"disambiguationData":[TD([[subQ2,-1.0]])],"derivedFrom":subQ1}),1.0]])]});}
            var Q88;
            {var subQ0=sQuery(id+"F0.wireOp",EDGE,"E25");var subQ1=sQuery(id+"F0.wireOp",EDGE,"E12");var subQ2=makeQuery(id+"F0.imprint","INTERSECT",VERTEX,{"derivedFrom":[subQ1,subQ0]});Q88=makeQuery(id+"F0.imprint","IMPRINT",FACE,{"disambiguationData":[TD([[makeQuery(id+"F0.imprint","IMPRINT",EDGE,{"disambiguationData":[TD([[subQ2,-1.0]])],"derivedFrom":subQ1}),1.0]])]});}
            var Q89;
            {var subQ0=sQuery(id+"F0.wireOp",EDGE,"E26");var subQ1=sQuery(id+"F0.wireOp",EDGE,"E7");var subQ2=makeQuery(id+"F0.imprint","INTERSECT",VERTEX,{"derivedFrom":[subQ1,subQ0]});Q89=makeQuery(id+"F0.imprint","IMPRINT",FACE,{"disambiguationData":[TD([[makeQuery(id+"F0.imprint","IMPRINT",EDGE,{"disambiguationData":[TD([[subQ2,-1.0]])],"derivedFrom":subQ1}),1.0]])]});}
            var Q90;
            {var subQ0=sQuery(id+"F0.wireOp",EDGE,"E22");var subQ1=sQuery(id+"F0.wireOp",EDGE,"E6");var subQ2=makeQuery(id+"F0.imprint","INTERSECT",VERTEX,{"derivedFrom":[subQ1,subQ0]});Q90=makeQuery(id+"F0.imprint","IMPRINT",FACE,{"disambiguationData":[TD([[makeQuery(id+"F0.imprint","IMPRINT",EDGE,{"disambiguationData":[TD([[subQ2,-1.0]])],"derivedFrom":subQ1}),1.0]])]});}
            var Q91;
            {var subQ0=sQuery(id+"F0.wireOp",EDGE,"E33");var subQ1=sQuery(id+"F0.wireOp",EDGE,"E2");var subQ2=makeQuery(id+"F0.imprint","INTERSECT",VERTEX,{"derivedFrom":[subQ1,subQ0]});Q91=makeQuery(id+"F0.imprint","IMPRINT",FACE,{"disambiguationData":[TD([[makeQuery(id+"F0.imprint","IMPRINT",EDGE,{"disambiguationData":[TD([[subQ2,-1.0]])],"derivedFrom":subQ1}),1.0]])]});}
            var Q92;
            {var subQ0=sQuery(id+"F0.wireOp",EDGE,"E21");var subQ1=sQuery(id+"F0.wireOp",EDGE,"E8");var subQ2=makeQuery(id+"F0.imprint","INTERSECT",VERTEX,{"derivedFrom":[subQ1,subQ0]});Q92=makeQuery(id+"F0.imprint","IMPRINT",FACE,{"disambiguationData":[TD([[makeQuery(id+"F0.imprint","IMPRINT",EDGE,{"disambiguationData":[TD([[subQ2,-1.0]])],"derivedFrom":subQ1}),1.0]])]});}
            var Q93;
            {var subQ0=sQuery(id+"F0.wireOp",EDGE,"E22");var subQ1=sQuery(id+"F0.wireOp",EDGE,"E11");var subQ2=makeQuery(id+"F0.imprint","INTERSECT",VERTEX,{"derivedFrom":[subQ1,subQ0]});Q93=makeQuery(id+"F0.imprint","IMPRINT",FACE,{"disambiguationData":[TD([[makeQuery(id+"F0.imprint","IMPRINT",EDGE,{"disambiguationData":[TD([[subQ2,-1.0]])],"derivedFrom":subQ1}),1.0]])]});}
            var Q94;
            {var subQ0=sQuery(id+"F0.wireOp",EDGE,"E32");var subQ1=sQuery(id+"F0.wireOp",EDGE,"E13");var subQ2=makeQuery(id+"F0.imprint","INTERSECT",VERTEX,{"derivedFrom":[subQ1,subQ0]});Q94=makeQuery(id+"F0.imprint","IMPRINT",FACE,{"disambiguationData":[TD([[makeQuery(id+"F0.imprint","IMPRINT",EDGE,{"disambiguationData":[TD([[subQ2,-1.0]])],"derivedFrom":subQ1}),1.0]])]});}
            var Q95;
            {var subQ0=sQuery(id+"F0.wireOp",EDGE,"E21");var subQ1=sQuery(id+"F0.wireOp",EDGE,"E14");var subQ2=makeQuery(id+"F0.imprint","INTERSECT",VERTEX,{"derivedFrom":[subQ1,subQ0]});Q95=makeQuery(id+"F0.imprint","IMPRINT",FACE,{"disambiguationData":[TD([[makeQuery(id+"F0.imprint","IMPRINT",EDGE,{"disambiguationData":[TD([[subQ2,-1.0]])],"derivedFrom":subQ1}),1.0]])]});}
            var Q96;
            {var subQ0=sQuery(id+"F0.wireOp",EDGE,"E29");var subQ1=sQuery(id+"F0.wireOp",EDGE,"E6");var subQ2=makeQuery(id+"F0.imprint","INTERSECT",VERTEX,{"derivedFrom":[subQ1,subQ0]});Q96=makeQuery(id+"F0.imprint","IMPRINT",FACE,{"disambiguationData":[TD([[makeQuery(id+"F0.imprint","IMPRINT",EDGE,{"disambiguationData":[TD([[subQ2,-1.0]])],"derivedFrom":subQ1}),1.0]])]});}
            var Q97;
            {var subQ0=sQuery(id+"F0.wireOp",EDGE,"E30");var subQ1=sQuery(id+"F0.wireOp",EDGE,"E1");var subQ2=makeQuery(id+"F0.imprint","INTERSECT",VERTEX,{"derivedFrom":[subQ1,subQ0]});Q97=makeQuery(id+"F0.imprint","IMPRINT",FACE,{"disambiguationData":[TD([[makeQuery(id+"F0.imprint","IMPRINT",EDGE,{"disambiguationData":[TD([[subQ2,-1.0]])],"derivedFrom":subQ1}),1.0]])]});}
            var Q98;
            {var subQ0=sQuery(id+"F0.wireOp",EDGE,"E35");var subQ1=sQuery(id+"F0.wireOp",EDGE,"E6");var subQ2=makeQuery(id+"F0.imprint","INTERSECT",VERTEX,{"derivedFrom":[subQ1,subQ0]});Q98=makeQuery(id+"F0.imprint","IMPRINT",FACE,{"disambiguationData":[TD([[makeQuery(id+"F0.imprint","IMPRINT",EDGE,{"disambiguationData":[TD([[subQ2,-1.0]])],"derivedFrom":subQ1}),1.0]])]});}
            var Q99;
            {var subQ0=sQuery(id+"F0.wireOp",EDGE,"E19");var subQ1=sQuery(id+"F0.wireOp",EDGE,"E6");var subQ2=makeQuery(id+"F0.imprint","INTERSECT",VERTEX,{"derivedFrom":[subQ1,subQ0]});Q99=makeQuery(id+"F0.imprint","IMPRINT",FACE,{"disambiguationData":[TD([[makeQuery(id+"F0.imprint","IMPRINT",EDGE,{"disambiguationData":[TD([[subQ2,-1.0]])],"derivedFrom":subQ1}),1.0]])]});}
            var Q100;
            {var subQ0=sQuery(id+"F0.wireOp",EDGE,"E30");var subQ1=sQuery(id+"F0.wireOp",EDGE,"E8");var subQ2=makeQuery(id+"F0.imprint","INTERSECT",VERTEX,{"derivedFrom":[subQ1,subQ0]});Q100=makeQuery(id+"F0.imprint","IMPRINT",FACE,{"disambiguationData":[TD([[makeQuery(id+"F0.imprint","IMPRINT",EDGE,{"disambiguationData":[TD([[subQ2,-1.0]])],"derivedFrom":subQ1}),1.0]])]});}
            var Q101;
            {var subQ0=sQuery(id+"F0.wireOp",EDGE,"E30");var subQ1=sQuery(id+"F0.wireOp",EDGE,"E2");var subQ2=makeQuery(id+"F0.imprint","INTERSECT",VERTEX,{"derivedFrom":[subQ1,subQ0]});Q101=makeQuery(id+"F0.imprint","IMPRINT",FACE,{"disambiguationData":[TD([[makeQuery(id+"F0.imprint","IMPRINT",EDGE,{"disambiguationData":[TD([[subQ2,-1.0]])],"derivedFrom":subQ1}),1.0]])]});}
            var Q102;
            {var subQ0=sQuery(id+"F0.wireOp",EDGE,"E21");var subQ1=sQuery(id+"F0.wireOp",EDGE,"E2");var subQ2=makeQuery(id+"F0.imprint","INTERSECT",VERTEX,{"derivedFrom":[subQ1,subQ0]});Q102=makeQuery(id+"F0.imprint","IMPRINT",FACE,{"disambiguationData":[TD([[makeQuery(id+"F0.imprint","IMPRINT",EDGE,{"disambiguationData":[TD([[subQ2,-1.0]])],"derivedFrom":subQ1}),1.0]])]});}
            var Q103;
            {var subQ0=sQuery(id+"F0.wireOp",EDGE,"E27");var subQ1=sQuery(id+"F0.wireOp",EDGE,"E6");var subQ2=makeQuery(id+"F0.imprint","INTERSECT",VERTEX,{"derivedFrom":[subQ1,subQ0]});Q103=makeQuery(id+"F0.imprint","IMPRINT",FACE,{"disambiguationData":[TD([[makeQuery(id+"F0.imprint","IMPRINT",EDGE,{"disambiguationData":[TD([[subQ2,-1.0]])],"derivedFrom":subQ1}),1.0]])]});}
            var Q104;
            {var subQ0=sQuery(id+"F0.wireOp",EDGE,"E19");var subQ1=sQuery(id+"F0.wireOp",EDGE,"E8");var subQ2=makeQuery(id+"F0.imprint","INTERSECT",VERTEX,{"derivedFrom":[subQ1,subQ0]});Q104=makeQuery(id+"F0.imprint","IMPRINT",FACE,{"disambiguationData":[TD([[makeQuery(id+"F0.imprint","IMPRINT",EDGE,{"disambiguationData":[TD([[subQ2,-1.0]])],"derivedFrom":subQ1}),1.0]])]});}
            var Q105;
            {var subQ0=sQuery(id+"F0.wireOp",EDGE,"E30");var subQ1=sQuery(id+"F0.wireOp",EDGE,"E16");var subQ2=makeQuery(id+"F0.imprint","INTERSECT",VERTEX,{"derivedFrom":[subQ1,subQ0]});Q105=makeQuery(id+"F0.imprint","IMPRINT",FACE,{"disambiguationData":[TD([[makeQuery(id+"F0.imprint","IMPRINT",EDGE,{"disambiguationData":[TD([[subQ2,-1.0]])],"derivedFrom":subQ1}),1.0]])]});}
            var Q106;
            {var subQ0=sQuery(id+"F0.wireOp",EDGE,"E24");var subQ1=sQuery(id+"F0.wireOp",EDGE,"E16");var subQ2=makeQuery(id+"F0.imprint","INTERSECT",VERTEX,{"derivedFrom":[subQ1,subQ0]});Q106=makeQuery(id+"F0.imprint","IMPRINT",FACE,{"disambiguationData":[TD([[makeQuery(id+"F0.imprint","IMPRINT",EDGE,{"disambiguationData":[TD([[subQ2,-1.0]])],"derivedFrom":subQ1}),1.0]])]});}
            var Q107;
            {var subQ0=sQuery(id+"F0.wireOp",EDGE,"E19");var subQ1=sQuery(id+"F0.wireOp",EDGE,"E12");var subQ2=makeQuery(id+"F0.imprint","INTERSECT",VERTEX,{"derivedFrom":[subQ1,subQ0]});Q107=makeQuery(id+"F0.imprint","IMPRINT",FACE,{"disambiguationData":[TD([[makeQuery(id+"F0.imprint","IMPRINT",EDGE,{"disambiguationData":[TD([[subQ2,-1.0]])],"derivedFrom":subQ1}),1.0]])]});}
            var Q108;
            {var subQ0=sQuery(id+"F0.wireOp",EDGE,"E27");var subQ1=sQuery(id+"F0.wireOp",EDGE,"E8");var subQ2=makeQuery(id+"F0.imprint","INTERSECT",VERTEX,{"derivedFrom":[subQ1,subQ0]});Q108=makeQuery(id+"F0.imprint","IMPRINT",FACE,{"disambiguationData":[TD([[makeQuery(id+"F0.imprint","IMPRINT",EDGE,{"disambiguationData":[TD([[subQ2,-1.0]])],"derivedFrom":subQ1}),1.0]])]});}
            var Q109;
            {var subQ0=sQuery(id+"F0.wireOp",EDGE,"E22");var subQ1=sQuery(id+"F0.wireOp",EDGE,"E7");var subQ2=makeQuery(id+"F0.imprint","INTERSECT",VERTEX,{"derivedFrom":[subQ1,subQ0]});Q109=makeQuery(id+"F0.imprint","IMPRINT",FACE,{"disambiguationData":[TD([[makeQuery(id+"F0.imprint","IMPRINT",EDGE,{"disambiguationData":[TD([[subQ2,-1.0]])],"derivedFrom":subQ1}),1.0]])]});}
            var Q110;
            {var subQ0=sQuery(id+"F0.wireOp",EDGE,"E21");var subQ1=sQuery(id+"F0.wireOp",EDGE,"E6");var subQ2=makeQuery(id+"F0.imprint","INTERSECT",VERTEX,{"derivedFrom":[subQ1,subQ0]});Q110=makeQuery(id+"F0.imprint","IMPRINT",FACE,{"disambiguationData":[TD([[makeQuery(id+"F0.imprint","IMPRINT",EDGE,{"disambiguationData":[TD([[subQ2,-1.0]])],"derivedFrom":subQ1}),1.0]])]});}
            var Q111;
            {var subQ0=sQuery(id+"F0.wireOp",EDGE,"E29");var subQ1=sQuery(id+"F0.wireOp",EDGE,"E2");var subQ2=makeQuery(id+"F0.imprint","INTERSECT",VERTEX,{"derivedFrom":[subQ1,subQ0]});Q111=makeQuery(id+"F0.imprint","IMPRINT",FACE,{"disambiguationData":[TD([[makeQuery(id+"F0.imprint","IMPRINT",EDGE,{"disambiguationData":[TD([[subQ2,-1.0]])],"derivedFrom":subQ1}),1.0]])]});}
            var Q112;
            {var subQ0=sQuery(id+"F0.wireOp",EDGE,"E27");var subQ1=sQuery(id+"F0.wireOp",EDGE,"E12");var subQ2=makeQuery(id+"F0.imprint","INTERSECT",VERTEX,{"derivedFrom":[subQ1,subQ0]});Q112=makeQuery(id+"F0.imprint","IMPRINT",FACE,{"disambiguationData":[TD([[makeQuery(id+"F0.imprint","IMPRINT",EDGE,{"disambiguationData":[TD([[subQ2,-1.0]])],"derivedFrom":subQ1}),1.0]])]});}
            var Q113;
            {var subQ0=sQuery(id+"F0.wireOp",EDGE,"E32");var subQ1=sQuery(id+"F0.wireOp",EDGE,"E2");var subQ2=makeQuery(id+"F0.imprint","INTERSECT",VERTEX,{"derivedFrom":[subQ1,subQ0]});Q113=makeQuery(id+"F0.imprint","IMPRINT",FACE,{"disambiguationData":[TD([[makeQuery(id+"F0.imprint","IMPRINT",EDGE,{"disambiguationData":[TD([[subQ2,-1.0]])],"derivedFrom":subQ1}),1.0]])]});}
            var Q114;
            {var subQ0=sQuery(id+"F0.wireOp",EDGE,"E22");var subQ1=sQuery(id+"F0.wireOp",EDGE,"E12");var subQ2=makeQuery(id+"F0.imprint","INTERSECT",VERTEX,{"derivedFrom":[subQ1,subQ0]});Q114=makeQuery(id+"F0.imprint","IMPRINT",FACE,{"disambiguationData":[TD([[makeQuery(id+"F0.imprint","IMPRINT",EDGE,{"disambiguationData":[TD([[subQ2,-1.0]])],"derivedFrom":subQ1}),1.0]])]});}
            var Q115;
            {var subQ0=sQuery(id+"F0.wireOp",EDGE,"E26");var subQ1=sQuery(id+"F0.wireOp",EDGE,"E15");var subQ2=makeQuery(id+"F0.imprint","INTERSECT",VERTEX,{"derivedFrom":[subQ1,subQ0]});Q115=makeQuery(id+"F0.imprint","IMPRINT",FACE,{"disambiguationData":[TD([[makeQuery(id+"F0.imprint","IMPRINT",EDGE,{"disambiguationData":[TD([[subQ2,-1.0]])],"derivedFrom":subQ1}),1.0]])]});}
            var Q116;
            {var subQ0=sQuery(id+"F0.wireOp",EDGE,"E24");var subQ1=sQuery(id+"F0.wireOp",EDGE,"E14");var subQ2=makeQuery(id+"F0.imprint","INTERSECT",VERTEX,{"derivedFrom":[subQ1,subQ0]});Q116=makeQuery(id+"F0.imprint","IMPRINT",FACE,{"disambiguationData":[TD([[makeQuery(id+"F0.imprint","IMPRINT",EDGE,{"disambiguationData":[TD([[subQ2,-1.0]])],"derivedFrom":subQ1}),1.0]])]});}
            var Q117;
            {var subQ0=sQuery(id+"F0.wireOp",EDGE,"E21");var subQ1=sQuery(id+"F0.wireOp",EDGE,"E12");var subQ2=makeQuery(id+"F0.imprint","INTERSECT",VERTEX,{"derivedFrom":[subQ1,subQ0]});Q117=makeQuery(id+"F0.imprint","IMPRINT",FACE,{"disambiguationData":[TD([[makeQuery(id+"F0.imprint","IMPRINT",EDGE,{"disambiguationData":[TD([[subQ2,-1.0]])],"derivedFrom":subQ1}),1.0]])]});}
            var Q118;
            {var subQ0=sQuery(id+"F0.wireOp",EDGE,"E22");var subQ1=sQuery(id+"F0.wireOp",EDGE,"E5");var subQ2=makeQuery(id+"F0.imprint","INTERSECT",VERTEX,{"derivedFrom":[subQ1,subQ0]});Q118=makeQuery(id+"F0.imprint","IMPRINT",FACE,{"disambiguationData":[TD([[makeQuery(id+"F0.imprint","IMPRINT",EDGE,{"disambiguationData":[TD([[subQ2,-1.0]])],"derivedFrom":subQ1}),1.0]])]});}
            var Q119;
            {var subQ0=sQuery(id+"F0.wireOp",EDGE,"E24");var subQ1=sQuery(id+"F0.wireOp",EDGE,"E15");var subQ2=makeQuery(id+"F0.imprint","INTERSECT",VERTEX,{"derivedFrom":[subQ1,subQ0]});Q119=makeQuery(id+"F0.imprint","IMPRINT",FACE,{"disambiguationData":[TD([[makeQuery(id+"F0.imprint","IMPRINT",EDGE,{"disambiguationData":[TD([[subQ2,-1.0]])],"derivedFrom":subQ1}),1.0]])]});}
            var Q120;
            {var subQ0=sQuery(id+"F0.wireOp",EDGE,"E29");var subQ1=sQuery(id+"F0.wireOp",EDGE,"E14");var subQ2=makeQuery(id+"F0.imprint","INTERSECT",VERTEX,{"derivedFrom":[subQ1,subQ0]});Q120=makeQuery(id+"F0.imprint","IMPRINT",FACE,{"disambiguationData":[TD([[makeQuery(id+"F0.imprint","IMPRINT",EDGE,{"disambiguationData":[TD([[subQ2,-1.0]])],"derivedFrom":subQ1}),1.0]])]});}
            var Q121;
            {var subQ0=sQuery(id+"F0.wireOp",EDGE,"E31");var subQ1=sQuery(id+"F0.wireOp",EDGE,"E16");var subQ2=makeQuery(id+"F0.imprint","INTERSECT",VERTEX,{"derivedFrom":[subQ1,subQ0]});Q121=makeQuery(id+"F0.imprint","IMPRINT",FACE,{"disambiguationData":[TD([[makeQuery(id+"F0.imprint","IMPRINT",EDGE,{"disambiguationData":[TD([[subQ2,-1.0]])],"derivedFrom":subQ1}),1.0]])]});}
            var Q122;
            {var subQ0=sQuery(id+"F0.wireOp",EDGE,"E34");var subQ1=sQuery(id+"F0.wireOp",EDGE,"E15");var subQ2=makeQuery(id+"F0.imprint","INTERSECT",VERTEX,{"derivedFrom":[subQ1,subQ0]});Q122=makeQuery(id+"F0.imprint","IMPRINT",FACE,{"disambiguationData":[TD([[makeQuery(id+"F0.imprint","IMPRINT",EDGE,{"disambiguationData":[TD([[subQ2,-1.0]])],"derivedFrom":subQ1}),1.0]])]});}
            var Q123;
            {var subQ0=sQuery(id+"F0.wireOp",EDGE,"E20");var subQ1=sQuery(id+"F0.wireOp",EDGE,"E6");var subQ2=makeQuery(id+"F0.imprint","INTERSECT",VERTEX,{"derivedFrom":[subQ1,subQ0]});Q123=makeQuery(id+"F0.imprint","IMPRINT",FACE,{"disambiguationData":[TD([[makeQuery(id+"F0.imprint","IMPRINT",EDGE,{"disambiguationData":[TD([[subQ2,-1.0]])],"derivedFrom":subQ1}),1.0]])]});}
            var Q124;
            {var subQ0=sQuery(id+"F0.wireOp",EDGE,"E22");var subQ1=sQuery(id+"F0.wireOp",EDGE,"E0.right");var subQ2=makeQuery(id+"F0.imprint","INTERSECT",VERTEX,{"derivedFrom":[subQ1,subQ0]});Q124=makeQuery(id+"F0.imprint","IMPRINT",FACE,{"disambiguationData":[TD([[makeQuery(id+"F0.imprint","IMPRINT",EDGE,{"disambiguationData":[TD([[subQ2,-1.0]])],"derivedFrom":subQ1}),-1.0]])]});}
            var Q125;
            {var subQ0=sQuery(id+"F0.wireOp",EDGE,"E7");var subQ1=sQuery(id+"F0.wireOp",EDGE,"E0.bottom");var subQ2=makeQuery(id+"F0.imprint","INTERSECT",VERTEX,{"derivedFrom":[subQ1,subQ0]});Q125=makeQuery(id+"F0.imprint","IMPRINT",FACE,{"disambiguationData":[TD([[makeQuery(id+"F0.imprint","IMPRINT",EDGE,{"disambiguationData":[TD([[subQ2,-1.0]])],"derivedFrom":subQ1}),-1.0]])]});}
            var Q126;
            {var subQ0=sQuery(id+"F0.wireOp",EDGE,"E20");var subQ1=sQuery(id+"F0.wireOp",EDGE,"E15");var subQ2=makeQuery(id+"F0.imprint","INTERSECT",VERTEX,{"derivedFrom":[subQ1,subQ0]});Q126=makeQuery(id+"F0.imprint","IMPRINT",FACE,{"disambiguationData":[TD([[makeQuery(id+"F0.imprint","IMPRINT",EDGE,{"disambiguationData":[TD([[subQ2,-1.0]])],"derivedFrom":subQ1}),1.0]])]});}
            var Q127;
            {var subQ0=sQuery(id+"F0.wireOp",EDGE,"E30");var subQ1=sQuery(id+"F0.wireOp",EDGE,"E0.left");var subQ2=makeQuery(id+"F0.imprint","INTERSECT",VERTEX,{"derivedFrom":[subQ1,subQ0]});Q127=makeQuery(id+"F0.imprint","IMPRINT",FACE,{"disambiguationData":[TD([[makeQuery(id+"F0.imprint","IMPRINT",EDGE,{"disambiguationData":[TD([[subQ2,-1.0]])],"derivedFrom":subQ1}),1.0]])]});}
            var Q128;
            {var subQ0=sQuery(id+"F0.wireOp",EDGE,"E20");var subQ1=sQuery(id+"F0.wireOp",EDGE,"E1");var subQ2=makeQuery(id+"F0.imprint","INTERSECT",VERTEX,{"derivedFrom":[subQ1,subQ0]});Q128=makeQuery(id+"F0.imprint","IMPRINT",FACE,{"disambiguationData":[TD([[makeQuery(id+"F0.imprint","IMPRINT",EDGE,{"disambiguationData":[TD([[subQ2,-1.0]])],"derivedFrom":subQ1}),1.0]])]});}
            var Q129;
            {var subQ0=sQuery(id+"F0.wireOp",EDGE,"E28");var subQ1=sQuery(id+"F0.wireOp",EDGE,"E12");var subQ2=makeQuery(id+"F0.imprint","INTERSECT",VERTEX,{"derivedFrom":[subQ1,subQ0]});Q129=makeQuery(id+"F0.imprint","IMPRINT",FACE,{"disambiguationData":[TD([[makeQuery(id+"F0.imprint","IMPRINT",EDGE,{"disambiguationData":[TD([[subQ2,-1.0]])],"derivedFrom":subQ1}),1.0]])]});}
            var Q130;
            {var subQ0=sQuery(id+"F0.wireOp",EDGE,"E35");var subQ1=sQuery(id+"F0.wireOp",EDGE,"E0.left");var subQ2=makeQuery(id+"F0.imprint","INTERSECT",VERTEX,{"derivedFrom":[subQ1,subQ0]});Q130=makeQuery(id+"F0.imprint","IMPRINT",FACE,{"disambiguationData":[TD([[makeQuery(id+"F0.imprint","IMPRINT",EDGE,{"disambiguationData":[TD([[subQ2,-1.0]])],"derivedFrom":subQ1}),1.0]])]});}
            var Q131;
            {var subQ0=sQuery(id+"F0.wireOp",EDGE,"E34");var subQ1=sQuery(id+"F0.wireOp",EDGE,"E17");var subQ2=makeQuery(id+"F0.imprint","INTERSECT",VERTEX,{"derivedFrom":[subQ1,subQ0]});Q131=makeQuery(id+"F0.imprint","IMPRINT",FACE,{"disambiguationData":[TD([[makeQuery(id+"F0.imprint","IMPRINT",EDGE,{"disambiguationData":[TD([[subQ2,-1.0]])],"derivedFrom":subQ1}),1.0]])]});}
            var Q132;
            {var subQ0=sQuery(id+"F0.wireOp",EDGE,"E28");var subQ1=sQuery(id+"F0.wireOp",EDGE,"E11");var subQ2=makeQuery(id+"F0.imprint","INTERSECT",VERTEX,{"derivedFrom":[subQ1,subQ0]});Q132=makeQuery(id+"F0.imprint","IMPRINT",FACE,{"disambiguationData":[TD([[makeQuery(id+"F0.imprint","IMPRINT",EDGE,{"disambiguationData":[TD([[subQ2,-1.0]])],"derivedFrom":subQ1}),1.0]])]});}
            var Q133;
            {var subQ0=sQuery(id+"F0.wireOp",EDGE,"E35");var subQ1=sQuery(id+"F0.wireOp",EDGE,"E0.right");var subQ2=makeQuery(id+"F0.imprint","INTERSECT",VERTEX,{"derivedFrom":[subQ1,subQ0]});Q133=makeQuery(id+"F0.imprint","IMPRINT",FACE,{"disambiguationData":[TD([[makeQuery(id+"F0.imprint","IMPRINT",EDGE,{"disambiguationData":[TD([[subQ2,-1.0]])],"derivedFrom":subQ1}),-1.0]])]});}
            var Q134;
            {var subQ0=sQuery(id+"F0.wireOp",EDGE,"E28");var subQ1=sQuery(id+"F0.wireOp",EDGE,"E10");var subQ2=makeQuery(id+"F0.imprint","INTERSECT",VERTEX,{"derivedFrom":[subQ1,subQ0]});Q134=makeQuery(id+"F0.imprint","IMPRINT",FACE,{"disambiguationData":[TD([[makeQuery(id+"F0.imprint","IMPRINT",EDGE,{"disambiguationData":[TD([[subQ2,-1.0]])],"derivedFrom":subQ1}),1.0]])]});}
            var Q135;
            {var subQ0=sQuery(id+"F0.wireOp",EDGE,"E17");var subQ1=sQuery(id+"F0.wireOp",EDGE,"E0.bottom");var subQ2=makeQuery(id+"F0.imprint","INTERSECT",VERTEX,{"derivedFrom":[subQ1,subQ0]});Q135=makeQuery(id+"F0.imprint","IMPRINT",FACE,{"disambiguationData":[TD([[makeQuery(id+"F0.imprint","IMPRINT",EDGE,{"disambiguationData":[TD([[subQ2,-1.0]])],"derivedFrom":subQ1}),-1.0]])]});}
            var Q136;
            {var subQ0=sQuery(id+"F0.wireOp",EDGE,"E13");var subQ1=sQuery(id+"F0.wireOp",EDGE,"E0.bottom");var subQ2=makeQuery(id+"F0.imprint","INTERSECT",VERTEX,{"derivedFrom":[subQ1,subQ0]});Q136=makeQuery(id+"F0.imprint","IMPRINT",FACE,{"disambiguationData":[TD([[makeQuery(id+"F0.imprint","IMPRINT",EDGE,{"disambiguationData":[TD([[subQ2,-1.0]])],"derivedFrom":subQ1}),-1.0]])]});}
            var Q137;
            {var subQ0=sQuery(id+"F0.wireOp",EDGE,"E20");var subQ1=sQuery(id+"F0.wireOp",EDGE,"E5");var subQ2=makeQuery(id+"F0.imprint","INTERSECT",VERTEX,{"derivedFrom":[subQ1,subQ0]});Q137=makeQuery(id+"F0.imprint","IMPRINT",FACE,{"disambiguationData":[TD([[makeQuery(id+"F0.imprint","IMPRINT",EDGE,{"disambiguationData":[TD([[subQ2,-1.0]])],"derivedFrom":subQ1}),1.0]])]});}
            var Q138;
            {var subQ0=sQuery(id+"F0.wireOp",EDGE,"E20");var subQ1=sQuery(id+"F0.wireOp",EDGE,"E16");var subQ2=makeQuery(id+"F0.imprint","INTERSECT",VERTEX,{"derivedFrom":[subQ1,subQ0]});Q138=makeQuery(id+"F0.imprint","IMPRINT",FACE,{"disambiguationData":[TD([[makeQuery(id+"F0.imprint","IMPRINT",EDGE,{"disambiguationData":[TD([[subQ2,-1.0]])],"derivedFrom":subQ1}),1.0]])]});}
            var Q139;
            {var subQ0=sQuery(id+"F0.wireOp",EDGE,"E16");var subQ1=sQuery(id+"F0.wireOp",EDGE,"E0.bottom");var subQ2=makeQuery(id+"F0.imprint","INTERSECT",VERTEX,{"derivedFrom":[subQ1,subQ0]});Q139=makeQuery(id+"F0.imprint","IMPRINT",FACE,{"disambiguationData":[TD([[makeQuery(id+"F0.imprint","IMPRINT",EDGE,{"disambiguationData":[TD([[subQ2,-1.0]])],"derivedFrom":subQ1}),-1.0]])]});}
            var Q140;
            {var subQ0=sQuery(id+"F0.wireOp",EDGE,"E33");var subQ1=sQuery(id+"F0.wireOp",EDGE,"E0.right");var subQ2=makeQuery(id+"F0.imprint","INTERSECT",VERTEX,{"derivedFrom":[subQ1,subQ0]});Q140=makeQuery(id+"F0.imprint","IMPRINT",FACE,{"disambiguationData":[TD([[makeQuery(id+"F0.imprint","IMPRINT",EDGE,{"disambiguationData":[TD([[subQ2,-1.0]])],"derivedFrom":subQ1}),-1.0]])]});}
            var Q141;
            {var subQ0=sQuery(id+"F0.wireOp",EDGE,"E28");var subQ1=sQuery(id+"F0.wireOp",EDGE,"E3");var subQ2=makeQuery(id+"F0.imprint","INTERSECT",VERTEX,{"derivedFrom":[subQ1,subQ0]});Q141=makeQuery(id+"F0.imprint","IMPRINT",FACE,{"disambiguationData":[TD([[makeQuery(id+"F0.imprint","IMPRINT",EDGE,{"disambiguationData":[TD([[subQ2,-1.0]])],"derivedFrom":subQ1}),1.0]])]});}
            var Q142;
            {var subQ0=sQuery(id+"F0.wireOp",EDGE,"E28");var subQ1=sQuery(id+"F0.wireOp",EDGE,"E6");var subQ2=makeQuery(id+"F0.imprint","INTERSECT",VERTEX,{"derivedFrom":[subQ1,subQ0]});Q142=makeQuery(id+"F0.imprint","IMPRINT",FACE,{"disambiguationData":[TD([[makeQuery(id+"F0.imprint","IMPRINT",EDGE,{"disambiguationData":[TD([[subQ2,-1.0]])],"derivedFrom":subQ1}),1.0]])]});}
            var Q143;
            {var subQ0=sQuery(id+"F0.wireOp",EDGE,"E28");var subQ1=sQuery(id+"F0.wireOp",EDGE,"E1");var subQ2=makeQuery(id+"F0.imprint","INTERSECT",VERTEX,{"derivedFrom":[subQ1,subQ0]});Q143=makeQuery(id+"F0.imprint","IMPRINT",FACE,{"disambiguationData":[TD([[makeQuery(id+"F0.imprint","IMPRINT",EDGE,{"disambiguationData":[TD([[subQ2,-1.0]])],"derivedFrom":subQ1}),1.0]])]});}
            var Q144;
            {var subQ0=sQuery(id+"F0.wireOp",EDGE,"E20");var subQ1=sQuery(id+"F0.wireOp",EDGE,"E10");var subQ2=makeQuery(id+"F0.imprint","INTERSECT",VERTEX,{"derivedFrom":[subQ1,subQ0]});Q144=makeQuery(id+"F0.imprint","IMPRINT",FACE,{"disambiguationData":[TD([[makeQuery(id+"F0.imprint","IMPRINT",EDGE,{"disambiguationData":[TD([[subQ2,-1.0]])],"derivedFrom":subQ1}),1.0]])]});}
            var Q145;
            {var subQ0=sQuery(id+"F0.wireOp",EDGE,"E20");var subQ1=sQuery(id+"F0.wireOp",EDGE,"E14");var subQ2=makeQuery(id+"F0.imprint","INTERSECT",VERTEX,{"derivedFrom":[subQ1,subQ0]});Q145=makeQuery(id+"F0.imprint","IMPRINT",FACE,{"disambiguationData":[TD([[makeQuery(id+"F0.imprint","IMPRINT",EDGE,{"disambiguationData":[TD([[subQ2,-1.0]])],"derivedFrom":subQ1}),1.0]])]});}
            var Q146;
            {var subQ0=sQuery(id+"F0.wireOp",EDGE,"E4");var subQ1=sQuery(id+"F0.wireOp",EDGE,"E0.bottom");var subQ2=makeQuery(id+"F0.imprint","INTERSECT",VERTEX,{"derivedFrom":[subQ1,subQ0]});Q146=makeQuery(id+"F0.imprint","IMPRINT",FACE,{"disambiguationData":[TD([[makeQuery(id+"F0.imprint","IMPRINT",EDGE,{"disambiguationData":[TD([[subQ2,-1.0]])],"derivedFrom":subQ1}),-1.0]])]});}
            var Q147;
            {var subQ0=sQuery(id+"F0.wireOp",EDGE,"E14");var subQ1=sQuery(id+"F0.wireOp",EDGE,"E0.bottom");var subQ2=makeQuery(id+"F0.imprint","INTERSECT",VERTEX,{"derivedFrom":[subQ1,subQ0]});Q147=makeQuery(id+"F0.imprint","IMPRINT",FACE,{"disambiguationData":[TD([[makeQuery(id+"F0.imprint","IMPRINT",EDGE,{"disambiguationData":[TD([[subQ2,-1.0]])],"derivedFrom":subQ1}),-1.0]])]});}
            var Q148;
            {var subQ0=sQuery(id+"F0.wireOp",EDGE,"E7");var subQ1=sQuery(id+"F0.wireOp",EDGE,"E0.top");var subQ2=makeQuery(id+"F0.imprint","INTERSECT",VERTEX,{"derivedFrom":[subQ1,subQ0]});Q148=makeQuery(id+"F0.imprint","IMPRINT",FACE,{"disambiguationData":[TD([[makeQuery(id+"F0.imprint","IMPRINT",EDGE,{"disambiguationData":[TD([[subQ2,-1.0]])],"derivedFrom":subQ1}),1.0]])]});}
            var Q149;
            {var subQ0=sQuery(id+"F0.wireOp",EDGE,"E30");var subQ1=sQuery(id+"F0.wireOp",EDGE,"E4");var subQ2=makeQuery(id+"F0.imprint","INTERSECT",VERTEX,{"derivedFrom":[subQ1,subQ0]});Q149=makeQuery(id+"F0.imprint","IMPRINT",FACE,{"disambiguationData":[TD([[makeQuery(id+"F0.imprint","IMPRINT",EDGE,{"disambiguationData":[TD([[subQ2,-1.0]])],"derivedFrom":subQ1}),1.0]])]});}
            var Q150;
            {var subQ0=sQuery(id+"F0.wireOp",EDGE,"E23");var subQ1=sQuery(id+"F0.wireOp",EDGE,"E0.right");var subQ2=makeQuery(id+"F0.imprint","INTERSECT",VERTEX,{"derivedFrom":[subQ1,subQ0]});Q150=makeQuery(id+"F0.imprint","IMPRINT",FACE,{"disambiguationData":[TD([[makeQuery(id+"F0.imprint","IMPRINT",EDGE,{"disambiguationData":[TD([[subQ2,-1.0]])],"derivedFrom":subQ1}),-1.0]])]});}
            var Q151;
            {var subQ0=sQuery(id+"F0.wireOp",EDGE,"E34");var subQ1=sQuery(id+"F0.wireOp",EDGE,"E16");var subQ2=makeQuery(id+"F0.imprint","INTERSECT",VERTEX,{"derivedFrom":[subQ1,subQ0]});Q151=makeQuery(id+"F0.imprint","IMPRINT",FACE,{"disambiguationData":[TD([[makeQuery(id+"F0.imprint","IMPRINT",EDGE,{"disambiguationData":[TD([[subQ2,-1.0]])],"derivedFrom":subQ1}),1.0]])]});}
            var Q152;
            {var subQ0=sQuery(id+"F0.wireOp",EDGE,"E32");var subQ1=sQuery(id+"F0.wireOp",EDGE,"E0.left");var subQ2=makeQuery(id+"F0.imprint","INTERSECT",VERTEX,{"derivedFrom":[subQ1,subQ0]});Q152=makeQuery(id+"F0.imprint","IMPRINT",FACE,{"disambiguationData":[TD([[makeQuery(id+"F0.imprint","IMPRINT",EDGE,{"disambiguationData":[TD([[subQ2,-1.0]])],"derivedFrom":subQ1}),1.0]])]});}
            var Q153;
            {var subQ0=sQuery(id+"F0.wireOp",EDGE,"E34");var subQ1=sQuery(id+"F0.wireOp",EDGE,"E7");var subQ2=makeQuery(id+"F0.imprint","INTERSECT",VERTEX,{"derivedFrom":[subQ1,subQ0]});Q153=makeQuery(id+"F0.imprint","IMPRINT",FACE,{"disambiguationData":[TD([[makeQuery(id+"F0.imprint","IMPRINT",EDGE,{"disambiguationData":[TD([[subQ2,-1.0]])],"derivedFrom":subQ1}),1.0]])]});}
            var Q154;
            {var subQ0=sQuery(id+"F0.wireOp",EDGE,"E14");var subQ1=sQuery(id+"F0.wireOp",EDGE,"E0.top");var subQ2=makeQuery(id+"F0.imprint","INTERSECT",VERTEX,{"derivedFrom":[subQ1,subQ0]});Q154=makeQuery(id+"F0.imprint","IMPRINT",FACE,{"disambiguationData":[TD([[makeQuery(id+"F0.imprint","IMPRINT",EDGE,{"disambiguationData":[TD([[subQ2,-1.0]])],"derivedFrom":subQ1}),1.0]])]});}
            var Q155;
            {var subQ0=sQuery(id+"F0.wireOp",EDGE,"E34");var subQ1=sQuery(id+"F0.wireOp",EDGE,"E1");var subQ2=makeQuery(id+"F0.imprint","INTERSECT",VERTEX,{"derivedFrom":[subQ1,subQ0]});Q155=makeQuery(id+"F0.imprint","IMPRINT",FACE,{"disambiguationData":[TD([[makeQuery(id+"F0.imprint","IMPRINT",EDGE,{"disambiguationData":[TD([[subQ2,-1.0]])],"derivedFrom":subQ1}),1.0]])]});}
            var Q156;
            {var subQ0=sQuery(id+"F0.wireOp",EDGE,"E21");var subQ1=sQuery(id+"F0.wireOp",EDGE,"E0.right");var subQ2=makeQuery(id+"F0.imprint","INTERSECT",VERTEX,{"derivedFrom":[subQ1,subQ0]});Q156=makeQuery(id+"F0.imprint","IMPRINT",FACE,{"disambiguationData":[TD([[makeQuery(id+"F0.imprint","IMPRINT",EDGE,{"disambiguationData":[TD([[subQ2,-1.0]])],"derivedFrom":subQ1}),-1.0]])]});}
            var Q157;
            {var subQ0=sQuery(id+"F0.wireOp",EDGE,"E16");var subQ1=sQuery(id+"F0.wireOp",EDGE,"E0.top");var subQ2=makeQuery(id+"F0.imprint","INTERSECT",VERTEX,{"derivedFrom":[subQ1,subQ0]});Q157=makeQuery(id+"F0.imprint","IMPRINT",FACE,{"disambiguationData":[TD([[makeQuery(id+"F0.imprint","IMPRINT",EDGE,{"disambiguationData":[TD([[subQ2,-1.0]])],"derivedFrom":subQ1}),1.0]])]});}
            var Q158;
            {var subQ0=sQuery(id+"F0.wireOp",EDGE,"E31");var subQ1=sQuery(id+"F0.wireOp",EDGE,"E4");var subQ2=makeQuery(id+"F0.imprint","INTERSECT",VERTEX,{"derivedFrom":[subQ1,subQ0]});Q158=makeQuery(id+"F0.imprint","IMPRINT",FACE,{"disambiguationData":[TD([[makeQuery(id+"F0.imprint","IMPRINT",EDGE,{"disambiguationData":[TD([[subQ2,-1.0]])],"derivedFrom":subQ1}),1.0]])]});}
            var Q159;
            {var subQ0=sQuery(id+"F0.wireOp",EDGE,"E32");var subQ1=sQuery(id+"F0.wireOp",EDGE,"E4");var subQ2=makeQuery(id+"F0.imprint","INTERSECT",VERTEX,{"derivedFrom":[subQ1,subQ0]});Q159=makeQuery(id+"F0.imprint","IMPRINT",FACE,{"disambiguationData":[TD([[makeQuery(id+"F0.imprint","IMPRINT",EDGE,{"disambiguationData":[TD([[subQ2,-1.0]])],"derivedFrom":subQ1}),1.0]])]});}
            var Q160;
            {var subQ0=sQuery(id+"F0.wireOp",EDGE,"E33");var subQ1=sQuery(id+"F0.wireOp",EDGE,"E0.left");var subQ2=makeQuery(id+"F0.imprint","INTERSECT",VERTEX,{"derivedFrom":[subQ1,subQ0]});Q160=makeQuery(id+"F0.imprint","IMPRINT",FACE,{"disambiguationData":[TD([[makeQuery(id+"F0.imprint","IMPRINT",EDGE,{"disambiguationData":[TD([[subQ2,-1.0]])],"derivedFrom":subQ1}),1.0]])]});}
            var Q161;
            {var subQ0=sQuery(id+"F0.wireOp",EDGE,"E20");var subQ1=sQuery(id+"F0.wireOp",EDGE,"E3");var subQ2=makeQuery(id+"F0.imprint","INTERSECT",VERTEX,{"derivedFrom":[subQ1,subQ0]});Q161=makeQuery(id+"F0.imprint","IMPRINT",FACE,{"disambiguationData":[TD([[makeQuery(id+"F0.imprint","IMPRINT",EDGE,{"disambiguationData":[TD([[subQ2,-1.0]])],"derivedFrom":subQ1}),1.0]])]});}
            var Q162;
            {var subQ0=sQuery(id+"F0.wireOp",EDGE,"E20");var subQ1=sQuery(id+"F0.wireOp",EDGE,"E17");var subQ2=makeQuery(id+"F0.imprint","INTERSECT",VERTEX,{"derivedFrom":[subQ1,subQ0]});Q162=makeQuery(id+"F0.imprint","IMPRINT",FACE,{"disambiguationData":[TD([[makeQuery(id+"F0.imprint","IMPRINT",EDGE,{"disambiguationData":[TD([[subQ2,-1.0]])],"derivedFrom":subQ1}),1.0]])]});}
            var Q163;
            {var subQ0=sQuery(id+"F0.wireOp",EDGE,"E28");var subQ1=sQuery(id+"F0.wireOp",EDGE,"E13");var subQ2=makeQuery(id+"F0.imprint","INTERSECT",VERTEX,{"derivedFrom":[subQ1,subQ0]});Q163=makeQuery(id+"F0.imprint","IMPRINT",FACE,{"disambiguationData":[TD([[makeQuery(id+"F0.imprint","IMPRINT",EDGE,{"disambiguationData":[TD([[subQ2,-1.0]])],"derivedFrom":subQ1}),1.0]])]});}
            var Q164;
            {var subQ0=sQuery(id+"F0.wireOp",EDGE,"E35");var subQ1=sQuery(id+"F0.wireOp",EDGE,"E4");var subQ2=makeQuery(id+"F0.imprint","INTERSECT",VERTEX,{"derivedFrom":[subQ1,subQ0]});Q164=makeQuery(id+"F0.imprint","IMPRINT",FACE,{"disambiguationData":[TD([[makeQuery(id+"F0.imprint","IMPRINT",EDGE,{"disambiguationData":[TD([[subQ2,-1.0]])],"derivedFrom":subQ1}),1.0]])]});}
            var Q165;
            {var subQ0=sQuery(id+"F0.wireOp",EDGE,"E34");var subQ1=sQuery(id+"F0.wireOp",EDGE,"E11");var subQ2=makeQuery(id+"F0.imprint","INTERSECT",VERTEX,{"derivedFrom":[subQ1,subQ0]});Q165=makeQuery(id+"F0.imprint","IMPRINT",FACE,{"disambiguationData":[TD([[makeQuery(id+"F0.imprint","IMPRINT",EDGE,{"disambiguationData":[TD([[subQ2,-1.0]])],"derivedFrom":subQ1}),1.0]])]});}
            var Q166;
            {var subQ0=sQuery(id+"F0.wireOp",EDGE,"E11");var subQ1=sQuery(id+"F0.wireOp",EDGE,"E0.bottom");var subQ2=makeQuery(id+"F0.imprint","INTERSECT",VERTEX,{"derivedFrom":[subQ1,subQ0]});Q166=makeQuery(id+"F0.imprint","IMPRINT",FACE,{"disambiguationData":[TD([[makeQuery(id+"F0.imprint","IMPRINT",EDGE,{"disambiguationData":[TD([[subQ2,-1.0]])],"derivedFrom":subQ1}),-1.0]])]});}
            var Q167;
            {var subQ0=sQuery(id+"F0.wireOp",EDGE,"E23");var subQ1=sQuery(id+"F0.wireOp",EDGE,"E0.left");var subQ2=makeQuery(id+"F0.imprint","INTERSECT",VERTEX,{"derivedFrom":[subQ1,subQ0]});Q167=makeQuery(id+"F0.imprint","IMPRINT",FACE,{"disambiguationData":[TD([[makeQuery(id+"F0.imprint","IMPRINT",EDGE,{"disambiguationData":[TD([[subQ2,-1.0]])],"derivedFrom":subQ1}),1.0]])]});}
            var Q168;
            {var subQ0=sQuery(id+"F0.wireOp",EDGE,"E26");var subQ1=sQuery(id+"F0.wireOp",EDGE,"E0.left");var subQ2=makeQuery(id+"F0.imprint","INTERSECT",VERTEX,{"derivedFrom":[subQ1,subQ0]});Q168=makeQuery(id+"F0.imprint","IMPRINT",FACE,{"disambiguationData":[TD([[makeQuery(id+"F0.imprint","IMPRINT",EDGE,{"disambiguationData":[TD([[subQ2,-1.0]])],"derivedFrom":subQ1}),1.0]])]});}
            var Q169;
            {var subQ0=sQuery(id+"F0.wireOp",EDGE,"E24");var subQ1=sQuery(id+"F0.wireOp",EDGE,"E0.left");var subQ2=makeQuery(id+"F0.imprint","INTERSECT",VERTEX,{"derivedFrom":[subQ1,subQ0]});Q169=makeQuery(id+"F0.imprint","IMPRINT",FACE,{"disambiguationData":[TD([[makeQuery(id+"F0.imprint","IMPRINT",EDGE,{"disambiguationData":[TD([[subQ2,-1.0]])],"derivedFrom":subQ1}),1.0]])]});}
            var Q170;
            {var subQ0=sQuery(id+"F0.wireOp",EDGE,"E31");var subQ1=sQuery(id+"F0.wireOp",EDGE,"E0.left");var subQ2=makeQuery(id+"F0.imprint","INTERSECT",VERTEX,{"derivedFrom":[subQ1,subQ0]});Q170=makeQuery(id+"F0.imprint","IMPRINT",FACE,{"disambiguationData":[TD([[makeQuery(id+"F0.imprint","IMPRINT",EDGE,{"disambiguationData":[TD([[subQ2,-1.0]])],"derivedFrom":subQ1}),1.0]])]});}
            var Q171;
            {var subQ0=sQuery(id+"F0.wireOp",EDGE,"E20");var subQ1=sQuery(id+"F0.wireOp",EDGE,"E0.right");var subQ2=makeQuery(id+"F0.imprint","INTERSECT",VERTEX,{"derivedFrom":[subQ1,subQ0]});Q171=makeQuery(id+"F0.imprint","IMPRINT",FACE,{"disambiguationData":[TD([[makeQuery(id+"F0.imprint","IMPRINT",EDGE,{"disambiguationData":[TD([[subQ2,-1.0]])],"derivedFrom":subQ1}),-1.0]])]});}
            var Q172;
            {var subQ0=sQuery(id+"F0.wireOp",EDGE,"E8");var subQ1=sQuery(id+"F0.wireOp",EDGE,"E0.bottom");var subQ2=makeQuery(id+"F0.imprint","INTERSECT",VERTEX,{"derivedFrom":[subQ1,subQ0]});Q172=makeQuery(id+"F0.imprint","IMPRINT",FACE,{"disambiguationData":[TD([[makeQuery(id+"F0.imprint","IMPRINT",EDGE,{"disambiguationData":[TD([[subQ2,-1.0]])],"derivedFrom":subQ1}),-1.0]])]});}
            var Q173;
            {var subQ0=sQuery(id+"F0.wireOp",EDGE,"E30");var subQ1=sQuery(id+"F0.wireOp",EDGE,"E0.right");var subQ2=makeQuery(id+"F0.imprint","INTERSECT",VERTEX,{"derivedFrom":[subQ1,subQ0]});Q173=makeQuery(id+"F0.imprint","IMPRINT",FACE,{"disambiguationData":[TD([[makeQuery(id+"F0.imprint","IMPRINT",EDGE,{"disambiguationData":[TD([[subQ2,-1.0]])],"derivedFrom":subQ1}),-1.0]])]});}
            var Q174;
            {var subQ0=sQuery(id+"F0.wireOp",EDGE,"E20");var subQ1=sQuery(id+"F0.wireOp",EDGE,"E9");var subQ2=makeQuery(id+"F0.imprint","INTERSECT",VERTEX,{"derivedFrom":[subQ1,subQ0]});Q174=makeQuery(id+"F0.imprint","IMPRINT",FACE,{"disambiguationData":[TD([[makeQuery(id+"F0.imprint","IMPRINT",EDGE,{"disambiguationData":[TD([[subQ2,-1.0]])],"derivedFrom":subQ1}),1.0]])]});}
            var Q175;
            {var subQ0=sQuery(id+"F0.wireOp",EDGE,"E20");var subQ1=sQuery(id+"F0.wireOp",EDGE,"E4");var subQ2=makeQuery(id+"F0.imprint","INTERSECT",VERTEX,{"derivedFrom":[subQ1,subQ0]});Q175=makeQuery(id+"F0.imprint","IMPRINT",FACE,{"disambiguationData":[TD([[makeQuery(id+"F0.imprint","IMPRINT",EDGE,{"disambiguationData":[TD([[subQ2,-1.0]])],"derivedFrom":subQ1}),1.0]])]});}
            var Q176;
            {var subQ0=sQuery(id+"F0.wireOp",EDGE,"E19");var subQ1=sQuery(id+"F0.wireOp",EDGE,"E0.left");var subQ2=makeQuery(id+"F0.imprint","INTERSECT",VERTEX,{"derivedFrom":[subQ1,subQ0]});Q176=makeQuery(id+"F0.imprint","IMPRINT",FACE,{"disambiguationData":[TD([[makeQuery(id+"F0.imprint","IMPRINT",EDGE,{"disambiguationData":[TD([[subQ2,-1.0]])],"derivedFrom":subQ1}),1.0]])]});}
            var Q177;
            {var subQ0=sQuery(id+"F0.wireOp",EDGE,"E22");var subQ1=sQuery(id+"F0.wireOp",EDGE,"E0.left");var subQ2=makeQuery(id+"F0.imprint","INTERSECT",VERTEX,{"derivedFrom":[subQ1,subQ0]});Q177=makeQuery(id+"F0.imprint","IMPRINT",FACE,{"disambiguationData":[TD([[makeQuery(id+"F0.imprint","IMPRINT",EDGE,{"disambiguationData":[TD([[subQ2,-1.0]])],"derivedFrom":subQ1}),1.0]])]});}
            var Q178;
            {var subQ0=sQuery(id+"F0.wireOp",EDGE,"E34");var subQ1=sQuery(id+"F0.wireOp",EDGE,"E0.left");var subQ2=makeQuery(id+"F0.imprint","INTERSECT",VERTEX,{"derivedFrom":[subQ1,subQ0]});Q178=makeQuery(id+"F0.imprint","IMPRINT",FACE,{"disambiguationData":[TD([[makeQuery(id+"F0.imprint","IMPRINT",EDGE,{"disambiguationData":[TD([[subQ2,-1.0]])],"derivedFrom":subQ1}),1.0]])]});}
            var Q179;
            {var subQ0=sQuery(id+"F0.wireOp",EDGE,"E34");var subQ1=sQuery(id+"F0.wireOp",EDGE,"E10");var subQ2=makeQuery(id+"F0.imprint","INTERSECT",VERTEX,{"derivedFrom":[subQ1,subQ0]});Q179=makeQuery(id+"F0.imprint","IMPRINT",FACE,{"disambiguationData":[TD([[makeQuery(id+"F0.imprint","IMPRINT",EDGE,{"disambiguationData":[TD([[subQ2,-1.0]])],"derivedFrom":subQ1}),1.0]])]});}
            var Q180;
            {var subQ0=sQuery(id+"F0.wireOp",EDGE,"E20");var subQ1=sQuery(id+"F0.wireOp",EDGE,"E8");var subQ2=makeQuery(id+"F0.imprint","INTERSECT",VERTEX,{"derivedFrom":[subQ1,subQ0]});Q180=makeQuery(id+"F0.imprint","IMPRINT",FACE,{"disambiguationData":[TD([[makeQuery(id+"F0.imprint","IMPRINT",EDGE,{"disambiguationData":[TD([[subQ2,-1.0]])],"derivedFrom":subQ1}),1.0]])]});}
            var Q181;
            {var subQ0=sQuery(id+"F0.wireOp",EDGE,"E25");var subQ1=sQuery(id+"F0.wireOp",EDGE,"E0.left");var subQ2=makeQuery(id+"F0.imprint","INTERSECT",VERTEX,{"derivedFrom":[subQ1,subQ0]});Q181=makeQuery(id+"F0.imprint","IMPRINT",FACE,{"disambiguationData":[TD([[makeQuery(id+"F0.imprint","IMPRINT",EDGE,{"disambiguationData":[TD([[subQ2,-1.0]])],"derivedFrom":subQ1}),1.0]])]});}
            var Q182;
            {var subQ0=sQuery(id+"F0.wireOp",EDGE,"E26");var subQ1=sQuery(id+"F0.wireOp",EDGE,"E0.right");var subQ2=makeQuery(id+"F0.imprint","INTERSECT",VERTEX,{"derivedFrom":[subQ1,subQ0]});Q182=makeQuery(id+"F0.imprint","IMPRINT",FACE,{"disambiguationData":[TD([[makeQuery(id+"F0.imprint","IMPRINT",EDGE,{"disambiguationData":[TD([[subQ2,-1.0]])],"derivedFrom":subQ1}),-1.0]])]});}
            var Q183;
            {var subQ0=sQuery(id+"F0.wireOp",EDGE,"E20");var subQ1=sQuery(id+"F0.wireOp",EDGE,"E11");var subQ2=makeQuery(id+"F0.imprint","INTERSECT",VERTEX,{"derivedFrom":[subQ1,subQ0]});Q183=makeQuery(id+"F0.imprint","IMPRINT",FACE,{"disambiguationData":[TD([[makeQuery(id+"F0.imprint","IMPRINT",EDGE,{"disambiguationData":[TD([[subQ2,-1.0]])],"derivedFrom":subQ1}),1.0]])]});}
            var Q184;
            {var subQ0=sQuery(id+"F0.wireOp",EDGE,"E34");var subQ1=sQuery(id+"F0.wireOp",EDGE,"E12");var subQ2=makeQuery(id+"F0.imprint","INTERSECT",VERTEX,{"derivedFrom":[subQ1,subQ0]});Q184=makeQuery(id+"F0.imprint","IMPRINT",FACE,{"disambiguationData":[TD([[makeQuery(id+"F0.imprint","IMPRINT",EDGE,{"disambiguationData":[TD([[subQ2,-1.0]])],"derivedFrom":subQ1}),1.0]])]});}
            var Q185;
            {var subQ0=sQuery(id+"F0.wireOp",EDGE,"E1");var subQ1=sQuery(id+"F0.wireOp",EDGE,"E0.top");var subQ2=makeQuery(id+"F0.imprint","INTERSECT",VERTEX,{"derivedFrom":[subQ1,subQ0]});Q185=makeQuery(id+"F0.imprint","IMPRINT",FACE,{"disambiguationData":[TD([[makeQuery(id+"F0.imprint","IMPRINT",EDGE,{"disambiguationData":[TD([[subQ2,-1.0]])],"derivedFrom":subQ1}),1.0]])]});}
            var Q186;
            {var subQ0=sQuery(id+"F0.wireOp",EDGE,"E8");var subQ1=sQuery(id+"F0.wireOp",EDGE,"E0.top");var subQ2=makeQuery(id+"F0.imprint","INTERSECT",VERTEX,{"derivedFrom":[subQ1,subQ0]});Q186=makeQuery(id+"F0.imprint","IMPRINT",FACE,{"disambiguationData":[TD([[makeQuery(id+"F0.imprint","IMPRINT",EDGE,{"disambiguationData":[TD([[subQ2,-1.0]])],"derivedFrom":subQ1}),1.0]])]});}
            var Q187;
            {var subQ0=sQuery(id+"F0.wireOp",EDGE,"E34");var subQ1=sQuery(id+"F0.wireOp",EDGE,"E8");var subQ2=makeQuery(id+"F0.imprint","INTERSECT",VERTEX,{"derivedFrom":[subQ1,subQ0]});Q187=makeQuery(id+"F0.imprint","IMPRINT",FACE,{"disambiguationData":[TD([[makeQuery(id+"F0.imprint","IMPRINT",EDGE,{"disambiguationData":[TD([[subQ2,-1.0]])],"derivedFrom":subQ1}),1.0]])]});}
            var Q188;
            {var subQ0=sQuery(id+"F0.wireOp",EDGE,"E29");var subQ1=sQuery(id+"F0.wireOp",EDGE,"E0.right");var subQ2=makeQuery(id+"F0.imprint","INTERSECT",VERTEX,{"derivedFrom":[subQ1,subQ0]});Q188=makeQuery(id+"F0.imprint","IMPRINT",FACE,{"disambiguationData":[TD([[makeQuery(id+"F0.imprint","IMPRINT",EDGE,{"disambiguationData":[TD([[subQ2,-1.0]])],"derivedFrom":subQ1}),-1.0]])]});}
            var Q189;
            {var subQ0=sQuery(id+"F0.wireOp",EDGE,"E28");var subQ1=sQuery(id+"F0.wireOp",EDGE,"E17");var subQ2=makeQuery(id+"F0.imprint","INTERSECT",VERTEX,{"derivedFrom":[subQ1,subQ0]});Q189=makeQuery(id+"F0.imprint","IMPRINT",FACE,{"disambiguationData":[TD([[makeQuery(id+"F0.imprint","IMPRINT",EDGE,{"disambiguationData":[TD([[subQ2,-1.0]])],"derivedFrom":subQ1}),1.0]])]});}
            var Q190;
            {var subQ0=sQuery(id+"F0.wireOp",EDGE,"E34");var subQ1=sQuery(id+"F0.wireOp",EDGE,"E2");var subQ2=makeQuery(id+"F0.imprint","INTERSECT",VERTEX,{"derivedFrom":[subQ1,subQ0]});Q190=makeQuery(id+"F0.imprint","IMPRINT",FACE,{"disambiguationData":[TD([[makeQuery(id+"F0.imprint","IMPRINT",EDGE,{"disambiguationData":[TD([[subQ2,-1.0]])],"derivedFrom":subQ1}),1.0]])]});}
            var Q191;
            {var subQ0=sQuery(id+"F0.wireOp",EDGE,"E15");var subQ1=sQuery(id+"F0.wireOp",EDGE,"E0.bottom");var subQ2=makeQuery(id+"F0.imprint","INTERSECT",VERTEX,{"derivedFrom":[subQ1,subQ0]});Q191=makeQuery(id+"F0.imprint","IMPRINT",FACE,{"disambiguationData":[TD([[makeQuery(id+"F0.imprint","IMPRINT",EDGE,{"disambiguationData":[TD([[subQ2,-1.0]])],"derivedFrom":subQ1}),-1.0]])]});}
            var Q192;
            {var subQ0=sQuery(id+"F0.wireOp",EDGE,"E28");var subQ1=sQuery(id+"F0.wireOp",EDGE,"E9");var subQ2=makeQuery(id+"F0.imprint","INTERSECT",VERTEX,{"derivedFrom":[subQ1,subQ0]});Q192=makeQuery(id+"F0.imprint","IMPRINT",FACE,{"disambiguationData":[TD([[makeQuery(id+"F0.imprint","IMPRINT",EDGE,{"disambiguationData":[TD([[subQ2,-1.0]])],"derivedFrom":subQ1}),1.0]])]});}
            var Q193;
            {var subQ0=sQuery(id+"F0.wireOp",EDGE,"E5");var subQ1=sQuery(id+"F0.wireOp",EDGE,"E0.bottom");var subQ2=makeQuery(id+"F0.imprint","INTERSECT",VERTEX,{"derivedFrom":[subQ1,subQ0]});Q193=makeQuery(id+"F0.imprint","IMPRINT",FACE,{"disambiguationData":[TD([[makeQuery(id+"F0.imprint","IMPRINT",EDGE,{"disambiguationData":[TD([[subQ2,-1.0]])],"derivedFrom":subQ1}),-1.0]])]});}
            var Q194;
            {var subQ0=sQuery(id+"F0.wireOp",EDGE,"E2");var subQ1=sQuery(id+"F0.wireOp",EDGE,"E0.bottom");var subQ2=makeQuery(id+"F0.imprint","INTERSECT",VERTEX,{"derivedFrom":[subQ1,subQ0]});Q194=makeQuery(id+"F0.imprint","IMPRINT",FACE,{"disambiguationData":[TD([[makeQuery(id+"F0.imprint","IMPRINT",EDGE,{"disambiguationData":[TD([[subQ2,-1.0]])],"derivedFrom":subQ1}),-1.0]])]});}
            var Q195;
            {var subQ0=sQuery(id+"F0.wireOp",EDGE,"E34");var subQ1=sQuery(id+"F0.wireOp",EDGE,"E14");var subQ2=makeQuery(id+"F0.imprint","INTERSECT",VERTEX,{"derivedFrom":[subQ1,subQ0]});Q195=makeQuery(id+"F0.imprint","IMPRINT",FACE,{"disambiguationData":[TD([[makeQuery(id+"F0.imprint","IMPRINT",EDGE,{"disambiguationData":[TD([[subQ2,-1.0]])],"derivedFrom":subQ1}),1.0]])]});}
            var Q196;
            {var subQ0=sQuery(id+"F0.wireOp",EDGE,"E3");var subQ1=sQuery(id+"F0.wireOp",EDGE,"E0.bottom");var subQ2=makeQuery(id+"F0.imprint","INTERSECT",VERTEX,{"derivedFrom":[subQ1,subQ0]});Q196=makeQuery(id+"F0.imprint","IMPRINT",FACE,{"disambiguationData":[TD([[makeQuery(id+"F0.imprint","IMPRINT",EDGE,{"disambiguationData":[TD([[subQ2,-1.0]])],"derivedFrom":subQ1}),-1.0]])]});}
            var Q197;
            {var subQ0=sQuery(id+"F0.wireOp",EDGE,"E28");var subQ1=sQuery(id+"F0.wireOp",EDGE,"E7");var subQ2=makeQuery(id+"F0.imprint","INTERSECT",VERTEX,{"derivedFrom":[subQ1,subQ0]});Q197=makeQuery(id+"F0.imprint","IMPRINT",FACE,{"disambiguationData":[TD([[makeQuery(id+"F0.imprint","IMPRINT",EDGE,{"disambiguationData":[TD([[subQ2,-1.0]])],"derivedFrom":subQ1}),1.0]])]});}
            var Q198;
            {var subQ0=sQuery(id+"F0.wireOp",EDGE,"E34");var subQ1=sQuery(id+"F0.wireOp",EDGE,"E9");var subQ2=makeQuery(id+"F0.imprint","INTERSECT",VERTEX,{"derivedFrom":[subQ1,subQ0]});Q198=makeQuery(id+"F0.imprint","IMPRINT",FACE,{"disambiguationData":[TD([[makeQuery(id+"F0.imprint","IMPRINT",EDGE,{"disambiguationData":[TD([[subQ2,-1.0]])],"derivedFrom":subQ1}),1.0]])]});}
            var Q199;
            {var subQ0=sQuery(id+"F0.wireOp",EDGE,"E13");var subQ1=sQuery(id+"F0.wireOp",EDGE,"E0.top");var subQ2=makeQuery(id+"F0.imprint","INTERSECT",VERTEX,{"derivedFrom":[subQ1,subQ0]});Q199=makeQuery(id+"F0.imprint","IMPRINT",FACE,{"disambiguationData":[TD([[makeQuery(id+"F0.imprint","IMPRINT",EDGE,{"disambiguationData":[TD([[subQ2,-1.0]])],"derivedFrom":subQ1}),1.0]])]});}
            var Q200;
            {var subQ0=sQuery(id+"F0.wireOp",EDGE,"E28");var subQ1=sQuery(id+"F0.wireOp",EDGE,"E0.left");var subQ2=makeQuery(id+"F0.imprint","INTERSECT",VERTEX,{"derivedFrom":[subQ1,subQ0]});Q200=makeQuery(id+"F0.imprint","IMPRINT",FACE,{"disambiguationData":[TD([[makeQuery(id+"F0.imprint","IMPRINT",EDGE,{"disambiguationData":[TD([[subQ2,-1.0]])],"derivedFrom":subQ1}),1.0]])]});}
            var Q201;
            {var subQ0=sQuery(id+"F0.wireOp",EDGE,"E29");var subQ1=sQuery(id+"F0.wireOp",EDGE,"E4");var subQ2=makeQuery(id+"F0.imprint","INTERSECT",VERTEX,{"derivedFrom":[subQ1,subQ0]});Q201=makeQuery(id+"F0.imprint","IMPRINT",FACE,{"disambiguationData":[TD([[makeQuery(id+"F0.imprint","IMPRINT",EDGE,{"disambiguationData":[TD([[subQ2,-1.0]])],"derivedFrom":subQ1}),1.0]])]});}
            var Q202;
            {var subQ0=sQuery(id+"F0.wireOp",EDGE,"E20");var subQ1=sQuery(id+"F0.wireOp",EDGE,"E2");var subQ2=makeQuery(id+"F0.imprint","INTERSECT",VERTEX,{"derivedFrom":[subQ1,subQ0]});Q202=makeQuery(id+"F0.imprint","IMPRINT",FACE,{"disambiguationData":[TD([[makeQuery(id+"F0.imprint","IMPRINT",EDGE,{"disambiguationData":[TD([[subQ2,-1.0]])],"derivedFrom":subQ1}),1.0]])]});}
            var Q203;
            {var subQ0=sQuery(id+"F0.wireOp",EDGE,"E27");var subQ1=sQuery(id+"F0.wireOp",EDGE,"E4");var subQ2=makeQuery(id+"F0.imprint","INTERSECT",VERTEX,{"derivedFrom":[subQ1,subQ0]});Q203=makeQuery(id+"F0.imprint","IMPRINT",FACE,{"disambiguationData":[TD([[makeQuery(id+"F0.imprint","IMPRINT",EDGE,{"disambiguationData":[TD([[subQ2,-1.0]])],"derivedFrom":subQ1}),1.0]])]});}
            var Q204;
            {var subQ0=sQuery(id+"F0.wireOp",EDGE,"E10");var subQ1=sQuery(id+"F0.wireOp",EDGE,"E0.top");var subQ2=makeQuery(id+"F0.imprint","INTERSECT",VERTEX,{"derivedFrom":[subQ1,subQ0]});Q204=makeQuery(id+"F0.imprint","IMPRINT",FACE,{"disambiguationData":[TD([[makeQuery(id+"F0.imprint","IMPRINT",EDGE,{"disambiguationData":[TD([[subQ2,-1.0]])],"derivedFrom":subQ1}),1.0]])]});}
            var Q205;
            {var subQ0=sQuery(id+"F0.wireOp",EDGE,"E21");var subQ1=sQuery(id+"F0.wireOp",EDGE,"E0.left");var subQ2=makeQuery(id+"F0.imprint","INTERSECT",VERTEX,{"derivedFrom":[subQ1,subQ0]});Q205=makeQuery(id+"F0.imprint","IMPRINT",FACE,{"disambiguationData":[TD([[makeQuery(id+"F0.imprint","IMPRINT",EDGE,{"disambiguationData":[TD([[subQ2,-1.0]])],"derivedFrom":subQ1}),1.0]])]});}
            var Q206;
            {var subQ0=sQuery(id+"F0.wireOp",EDGE,"E28");var subQ1=sQuery(id+"F0.wireOp",EDGE,"E15");var subQ2=makeQuery(id+"F0.imprint","INTERSECT",VERTEX,{"derivedFrom":[subQ1,subQ0]});Q206=makeQuery(id+"F0.imprint","IMPRINT",FACE,{"disambiguationData":[TD([[makeQuery(id+"F0.imprint","IMPRINT",EDGE,{"disambiguationData":[TD([[subQ2,-1.0]])],"derivedFrom":subQ1}),1.0]])]});}
            var Q207;
            {var subQ0=sQuery(id+"F0.wireOp",EDGE,"E9");var subQ1=sQuery(id+"F0.wireOp",EDGE,"E0.top");var subQ2=makeQuery(id+"F0.imprint","INTERSECT",VERTEX,{"derivedFrom":[subQ1,subQ0]});Q207=makeQuery(id+"F0.imprint","IMPRINT",FACE,{"disambiguationData":[TD([[makeQuery(id+"F0.imprint","IMPRINT",EDGE,{"disambiguationData":[TD([[subQ2,-1.0]])],"derivedFrom":subQ1}),1.0]])]});}
            var Q208;
            {var subQ0=sQuery(id+"F0.wireOp",EDGE,"E34");var subQ1=sQuery(id+"F0.wireOp",EDGE,"E13");var subQ2=makeQuery(id+"F0.imprint","INTERSECT",VERTEX,{"derivedFrom":[subQ1,subQ0]});Q208=makeQuery(id+"F0.imprint","IMPRINT",FACE,{"disambiguationData":[TD([[makeQuery(id+"F0.imprint","IMPRINT",EDGE,{"disambiguationData":[TD([[subQ2,-1.0]])],"derivedFrom":subQ1}),1.0]])]});}
            var Q209;
            {var subQ0=sQuery(id+"F0.wireOp",EDGE,"E29");var subQ1=sQuery(id+"F0.wireOp",EDGE,"E0.left");var subQ2=makeQuery(id+"F0.imprint","INTERSECT",VERTEX,{"derivedFrom":[subQ1,subQ0]});Q209=makeQuery(id+"F0.imprint","IMPRINT",FACE,{"disambiguationData":[TD([[makeQuery(id+"F0.imprint","IMPRINT",EDGE,{"disambiguationData":[TD([[subQ2,-1.0]])],"derivedFrom":subQ1}),1.0]])]});}
            var Q210;
            {var subQ0=sQuery(id+"F0.wireOp",EDGE,"E31");var subQ1=sQuery(id+"F0.wireOp",EDGE,"E0.right");var subQ2=makeQuery(id+"F0.imprint","INTERSECT",VERTEX,{"derivedFrom":[subQ1,subQ0]});Q210=makeQuery(id+"F0.imprint","IMPRINT",FACE,{"disambiguationData":[TD([[makeQuery(id+"F0.imprint","IMPRINT",EDGE,{"disambiguationData":[TD([[subQ2,-1.0]])],"derivedFrom":subQ1}),-1.0]])]});}
            var Q211;
            {var subQ0=sQuery(id+"F0.wireOp",EDGE,"E11");var subQ1=sQuery(id+"F0.wireOp",EDGE,"E0.top");var subQ2=makeQuery(id+"F0.imprint","INTERSECT",VERTEX,{"derivedFrom":[subQ1,subQ0]});Q211=makeQuery(id+"F0.imprint","IMPRINT",FACE,{"disambiguationData":[TD([[makeQuery(id+"F0.imprint","IMPRINT",EDGE,{"disambiguationData":[TD([[subQ2,-1.0]])],"derivedFrom":subQ1}),1.0]])]});}
            var Q212;
            {var subQ0=sQuery(id+"F0.wireOp",EDGE,"E4");var subQ1=sQuery(id+"F0.wireOp",EDGE,"E0.top");var subQ2=makeQuery(id+"F0.imprint","INTERSECT",VERTEX,{"derivedFrom":[subQ1,subQ0]});Q212=makeQuery(id+"F0.imprint","IMPRINT",FACE,{"disambiguationData":[TD([[makeQuery(id+"F0.imprint","IMPRINT",EDGE,{"disambiguationData":[TD([[subQ2,-1.0]])],"derivedFrom":subQ1}),1.0]])]});}
            var Q213;
            {var subQ0=sQuery(id+"F0.wireOp",EDGE,"E12");var subQ1=sQuery(id+"F0.wireOp",EDGE,"E0.top");var subQ2=makeQuery(id+"F0.imprint","INTERSECT",VERTEX,{"derivedFrom":[subQ1,subQ0]});Q213=makeQuery(id+"F0.imprint","IMPRINT",FACE,{"disambiguationData":[TD([[makeQuery(id+"F0.imprint","IMPRINT",EDGE,{"disambiguationData":[TD([[subQ2,-1.0]])],"derivedFrom":subQ1}),1.0]])]});}
            var Q214;
            {var subQ0=sQuery(id+"F0.wireOp",EDGE,"E28");var subQ1=sQuery(id+"F0.wireOp",EDGE,"E8");var subQ2=makeQuery(id+"F0.imprint","INTERSECT",VERTEX,{"derivedFrom":[subQ1,subQ0]});Q214=makeQuery(id+"F0.imprint","IMPRINT",FACE,{"disambiguationData":[TD([[makeQuery(id+"F0.imprint","IMPRINT",EDGE,{"disambiguationData":[TD([[subQ2,-1.0]])],"derivedFrom":subQ1}),1.0]])]});}
            var Q215;
            {var subQ0=sQuery(id+"F0.wireOp",EDGE,"E20");var subQ1=sQuery(id+"F0.wireOp",EDGE,"E7");var subQ2=makeQuery(id+"F0.imprint","INTERSECT",VERTEX,{"derivedFrom":[subQ1,subQ0]});Q215=makeQuery(id+"F0.imprint","IMPRINT",FACE,{"disambiguationData":[TD([[makeQuery(id+"F0.imprint","IMPRINT",EDGE,{"disambiguationData":[TD([[subQ2,-1.0]])],"derivedFrom":subQ1}),1.0]])]});}
            var Q216;
            {var subQ0=sQuery(id+"F0.wireOp",EDGE,"E2");var subQ1=sQuery(id+"F0.wireOp",EDGE,"E0.top");var subQ2=makeQuery(id+"F0.imprint","INTERSECT",VERTEX,{"derivedFrom":[subQ1,subQ0]});Q216=makeQuery(id+"F0.imprint","IMPRINT",FACE,{"disambiguationData":[TD([[makeQuery(id+"F0.imprint","IMPRINT",EDGE,{"disambiguationData":[TD([[subQ2,-1.0]])],"derivedFrom":subQ1}),1.0]])]});}
            var Q217;
            {var subQ0=sQuery(id+"F0.wireOp",EDGE,"E28");var subQ1=sQuery(id+"F0.wireOp",EDGE,"E2");var subQ2=makeQuery(id+"F0.imprint","INTERSECT",VERTEX,{"derivedFrom":[subQ1,subQ0]});Q217=makeQuery(id+"F0.imprint","IMPRINT",FACE,{"disambiguationData":[TD([[makeQuery(id+"F0.imprint","IMPRINT",EDGE,{"disambiguationData":[TD([[subQ2,-1.0]])],"derivedFrom":subQ1}),1.0]])]});}
            var Q218;
            {var subQ0=sQuery(id+"F0.wireOp",EDGE,"E28");var subQ1=sQuery(id+"F0.wireOp",EDGE,"E5");var subQ2=makeQuery(id+"F0.imprint","INTERSECT",VERTEX,{"derivedFrom":[subQ1,subQ0]});Q218=makeQuery(id+"F0.imprint","IMPRINT",FACE,{"disambiguationData":[TD([[makeQuery(id+"F0.imprint","IMPRINT",EDGE,{"disambiguationData":[TD([[subQ2,-1.0]])],"derivedFrom":subQ1}),1.0]])]});}
            var Q219;
            {var subQ0=sQuery(id+"F0.wireOp",EDGE,"E34");var subQ1=sQuery(id+"F0.wireOp",EDGE,"E6");var subQ2=makeQuery(id+"F0.imprint","INTERSECT",VERTEX,{"derivedFrom":[subQ1,subQ0]});Q219=makeQuery(id+"F0.imprint","IMPRINT",FACE,{"disambiguationData":[TD([[makeQuery(id+"F0.imprint","IMPRINT",EDGE,{"disambiguationData":[TD([[subQ2,-1.0]])],"derivedFrom":subQ1}),1.0]])]});}
            var Q220;
            {var subQ0=sQuery(id+"F0.wireOp",EDGE,"E17");var subQ1=sQuery(id+"F0.wireOp",EDGE,"E0.top");var subQ2=makeQuery(id+"F0.imprint","INTERSECT",VERTEX,{"derivedFrom":[subQ1,subQ0]});Q220=makeQuery(id+"F0.imprint","IMPRINT",FACE,{"disambiguationData":[TD([[makeQuery(id+"F0.imprint","IMPRINT",EDGE,{"disambiguationData":[TD([[subQ2,-1.0]])],"derivedFrom":subQ1}),1.0]])]});}
            var Q221;
            {var subQ0=sQuery(id+"F0.wireOp",EDGE,"E21");var subQ1=sQuery(id+"F0.wireOp",EDGE,"E4");var subQ2=makeQuery(id+"F0.imprint","INTERSECT",VERTEX,{"derivedFrom":[subQ1,subQ0]});Q221=makeQuery(id+"F0.imprint","IMPRINT",FACE,{"disambiguationData":[TD([[makeQuery(id+"F0.imprint","IMPRINT",EDGE,{"disambiguationData":[TD([[subQ2,-1.0]])],"derivedFrom":subQ1}),1.0]])]});}
            var Q222;
            {var subQ0=sQuery(id+"F0.wireOp",EDGE,"E19");var subQ1=sQuery(id+"F0.wireOp",EDGE,"E0.right");var subQ2=makeQuery(id+"F0.imprint","INTERSECT",VERTEX,{"derivedFrom":[subQ1,subQ0]});Q222=makeQuery(id+"F0.imprint","IMPRINT",FACE,{"disambiguationData":[TD([[makeQuery(id+"F0.imprint","IMPRINT",EDGE,{"disambiguationData":[TD([[subQ2,-1.0]])],"derivedFrom":subQ1}),-1.0]])]});}
            var Q223;
            {var subQ0=sQuery(id+"F0.wireOp",EDGE,"E5");var subQ1=sQuery(id+"F0.wireOp",EDGE,"E0.top");var subQ2=makeQuery(id+"F0.imprint","INTERSECT",VERTEX,{"derivedFrom":[subQ1,subQ0]});Q223=makeQuery(id+"F0.imprint","IMPRINT",FACE,{"disambiguationData":[TD([[makeQuery(id+"F0.imprint","IMPRINT",EDGE,{"disambiguationData":[TD([[subQ2,-1.0]])],"derivedFrom":subQ1}),1.0]])]});}
            var Q224;
            {var subQ0=sQuery(id+"F0.wireOp",EDGE,"E1");var subQ1=sQuery(id+"F0.wireOp",EDGE,"E0.bottom");var subQ2=makeQuery(id+"F0.imprint","INTERSECT",VERTEX,{"derivedFrom":[subQ1,subQ0]});Q224=makeQuery(id+"F0.imprint","IMPRINT",FACE,{"disambiguationData":[TD([[makeQuery(id+"F0.imprint","IMPRINT",EDGE,{"disambiguationData":[TD([[subQ2,-1.0]])],"derivedFrom":subQ1}),-1.0]])]});}
            var Q225;
            {var subQ0=sQuery(id+"F0.wireOp",EDGE,"E33");var subQ1=sQuery(id+"F0.wireOp",EDGE,"E4");var subQ2=makeQuery(id+"F0.imprint","INTERSECT",VERTEX,{"derivedFrom":[subQ1,subQ0]});Q225=makeQuery(id+"F0.imprint","IMPRINT",FACE,{"disambiguationData":[TD([[makeQuery(id+"F0.imprint","IMPRINT",EDGE,{"disambiguationData":[TD([[subQ2,-1.0]])],"derivedFrom":subQ1}),1.0]])]});}
            var Q226;
            {var subQ0=sQuery(id+"F0.wireOp",EDGE,"E19");var subQ1=sQuery(id+"F0.wireOp",EDGE,"E4");var subQ2=makeQuery(id+"F0.imprint","INTERSECT",VERTEX,{"derivedFrom":[subQ1,subQ0]});Q226=makeQuery(id+"F0.imprint","IMPRINT",FACE,{"disambiguationData":[TD([[makeQuery(id+"F0.imprint","IMPRINT",EDGE,{"disambiguationData":[TD([[subQ2,-1.0]])],"derivedFrom":subQ1}),1.0]])]});}
            var Q227;
            {var subQ0=sQuery(id+"F0.wireOp",EDGE,"E3");var subQ1=sQuery(id+"F0.wireOp",EDGE,"E0.top");var subQ2=makeQuery(id+"F0.imprint","INTERSECT",VERTEX,{"derivedFrom":[subQ1,subQ0]});Q227=makeQuery(id+"F0.imprint","IMPRINT",FACE,{"disambiguationData":[TD([[makeQuery(id+"F0.imprint","IMPRINT",EDGE,{"disambiguationData":[TD([[subQ2,-1.0]])],"derivedFrom":subQ1}),1.0]])]});}
            var Q228;
            {var subQ0=sQuery(id+"F0.wireOp",EDGE,"E28");var subQ1=sQuery(id+"F0.wireOp",EDGE,"E0.right");var subQ2=makeQuery(id+"F0.imprint","INTERSECT",VERTEX,{"derivedFrom":[subQ1,subQ0]});Q228=makeQuery(id+"F0.imprint","IMPRINT",FACE,{"disambiguationData":[TD([[makeQuery(id+"F0.imprint","IMPRINT",EDGE,{"disambiguationData":[TD([[subQ2,-1.0]])],"derivedFrom":subQ1}),-1.0]])]});}
            var Q229;
            {var subQ0=sQuery(id+"F0.wireOp",EDGE,"E32");var subQ1=sQuery(id+"F0.wireOp",EDGE,"E0.right");var subQ2=makeQuery(id+"F0.imprint","INTERSECT",VERTEX,{"derivedFrom":[subQ1,subQ0]});Q229=makeQuery(id+"F0.imprint","IMPRINT",FACE,{"disambiguationData":[TD([[makeQuery(id+"F0.imprint","IMPRINT",EDGE,{"disambiguationData":[TD([[subQ2,-1.0]])],"derivedFrom":subQ1}),-1.0]])]});}
            var Q230;
            {var subQ0=sQuery(id+"F0.wireOp",EDGE,"E27");var subQ1=sQuery(id+"F0.wireOp",EDGE,"E0.right");var subQ2=makeQuery(id+"F0.imprint","INTERSECT",VERTEX,{"derivedFrom":[subQ1,subQ0]});Q230=makeQuery(id+"F0.imprint","IMPRINT",FACE,{"disambiguationData":[TD([[makeQuery(id+"F0.imprint","IMPRINT",EDGE,{"disambiguationData":[TD([[subQ2,-1.0]])],"derivedFrom":subQ1}),-1.0]])]});}
            var Q231;
            {var subQ0=sQuery(id+"F0.wireOp",EDGE,"E6");var subQ1=sQuery(id+"F0.wireOp",EDGE,"E0.top");var subQ2=makeQuery(id+"F0.imprint","INTERSECT",VERTEX,{"derivedFrom":[subQ1,subQ0]});Q231=makeQuery(id+"F0.imprint","IMPRINT",FACE,{"disambiguationData":[TD([[makeQuery(id+"F0.imprint","IMPRINT",EDGE,{"disambiguationData":[TD([[subQ2,-1.0]])],"derivedFrom":subQ1}),1.0]])]});}
            var Q232;
            {var subQ0=sQuery(id+"F0.wireOp",EDGE,"E20");var subQ1=sQuery(id+"F0.wireOp",EDGE,"E0.left");var subQ2=makeQuery(id+"F0.imprint","INTERSECT",VERTEX,{"derivedFrom":[subQ1,subQ0]});Q232=makeQuery(id+"F0.imprint","IMPRINT",FACE,{"disambiguationData":[TD([[makeQuery(id+"F0.imprint","IMPRINT",EDGE,{"disambiguationData":[TD([[subQ2,-1.0]])],"derivedFrom":subQ1}),1.0]])]});}
            var Q233;
            {var subQ0=sQuery(id+"F0.wireOp",EDGE,"E27");var subQ1=sQuery(id+"F0.wireOp",EDGE,"E0.left");var subQ2=makeQuery(id+"F0.imprint","INTERSECT",VERTEX,{"derivedFrom":[subQ1,subQ0]});Q233=makeQuery(id+"F0.imprint","IMPRINT",FACE,{"disambiguationData":[TD([[makeQuery(id+"F0.imprint","IMPRINT",EDGE,{"disambiguationData":[TD([[subQ2,-1.0]])],"derivedFrom":subQ1}),1.0]])]});}
            var Q234;
            {var subQ0=sQuery(id+"F0.wireOp",EDGE,"E34");var subQ1=sQuery(id+"F0.wireOp",EDGE,"E5");var subQ2=makeQuery(id+"F0.imprint","INTERSECT",VERTEX,{"derivedFrom":[subQ1,subQ0]});Q234=makeQuery(id+"F0.imprint","IMPRINT",FACE,{"disambiguationData":[TD([[makeQuery(id+"F0.imprint","IMPRINT",EDGE,{"disambiguationData":[TD([[subQ2,-1.0]])],"derivedFrom":subQ1}),1.0]])]});}
            var Q235;
            {var subQ0=sQuery(id+"F0.wireOp",EDGE,"E9");var subQ1=sQuery(id+"F0.wireOp",EDGE,"E0.bottom");var subQ2=makeQuery(id+"F0.imprint","INTERSECT",VERTEX,{"derivedFrom":[subQ1,subQ0]});Q235=makeQuery(id+"F0.imprint","IMPRINT",FACE,{"disambiguationData":[TD([[makeQuery(id+"F0.imprint","IMPRINT",EDGE,{"disambiguationData":[TD([[subQ2,-1.0]])],"derivedFrom":subQ1}),-1.0]])]});}
            var Q236;
            {var subQ0=sQuery(id+"F0.wireOp",EDGE,"E28");var subQ1=sQuery(id+"F0.wireOp",EDGE,"E14");var subQ2=makeQuery(id+"F0.imprint","INTERSECT",VERTEX,{"derivedFrom":[subQ1,subQ0]});Q236=makeQuery(id+"F0.imprint","IMPRINT",FACE,{"disambiguationData":[TD([[makeQuery(id+"F0.imprint","IMPRINT",EDGE,{"disambiguationData":[TD([[subQ2,-1.0]])],"derivedFrom":subQ1}),1.0]])]});}
            var Q237;
            {var subQ0=sQuery(id+"F0.wireOp",EDGE,"E34");var subQ1=sQuery(id+"F0.wireOp",EDGE,"E0.right");var subQ2=makeQuery(id+"F0.imprint","INTERSECT",VERTEX,{"derivedFrom":[subQ1,subQ0]});Q237=makeQuery(id+"F0.imprint","IMPRINT",FACE,{"disambiguationData":[TD([[makeQuery(id+"F0.imprint","IMPRINT",EDGE,{"disambiguationData":[TD([[subQ2,-1.0]])],"derivedFrom":subQ1}),-1.0]])]});}
            var Q238;
            {var subQ0=sQuery(id+"F0.wireOp",EDGE,"E28");var subQ1=sQuery(id+"F0.wireOp",EDGE,"E16");var subQ2=makeQuery(id+"F0.imprint","INTERSECT",VERTEX,{"derivedFrom":[subQ1,subQ0]});Q238=makeQuery(id+"F0.imprint","IMPRINT",FACE,{"disambiguationData":[TD([[makeQuery(id+"F0.imprint","IMPRINT",EDGE,{"disambiguationData":[TD([[subQ2,-1.0]])],"derivedFrom":subQ1}),1.0]])]});}
            var Q239;
            {var subQ0=sQuery(id+"F0.wireOp",EDGE,"E24");var subQ1=sQuery(id+"F0.wireOp",EDGE,"E0.right");var subQ2=makeQuery(id+"F0.imprint","INTERSECT",VERTEX,{"derivedFrom":[subQ1,subQ0]});Q239=makeQuery(id+"F0.imprint","IMPRINT",FACE,{"disambiguationData":[TD([[makeQuery(id+"F0.imprint","IMPRINT",EDGE,{"disambiguationData":[TD([[subQ2,-1.0]])],"derivedFrom":subQ1}),-1.0]])]});}
            var Q240;
            {var subQ0=sQuery(id+"F0.wireOp",EDGE,"E20");var subQ1=sQuery(id+"F0.wireOp",EDGE,"E13");var subQ2=makeQuery(id+"F0.imprint","INTERSECT",VERTEX,{"derivedFrom":[subQ1,subQ0]});Q240=makeQuery(id+"F0.imprint","IMPRINT",FACE,{"disambiguationData":[TD([[makeQuery(id+"F0.imprint","IMPRINT",EDGE,{"disambiguationData":[TD([[subQ2,-1.0]])],"derivedFrom":subQ1}),1.0]])]});}
            var Q241;
            {var subQ0=sQuery(id+"F0.wireOp",EDGE,"E20");var subQ1=sQuery(id+"F0.wireOp",EDGE,"E12");var subQ2=makeQuery(id+"F0.imprint","INTERSECT",VERTEX,{"derivedFrom":[subQ1,subQ0]});Q241=makeQuery(id+"F0.imprint","IMPRINT",FACE,{"disambiguationData":[TD([[makeQuery(id+"F0.imprint","IMPRINT",EDGE,{"disambiguationData":[TD([[subQ2,-1.0]])],"derivedFrom":subQ1}),1.0]])]});}
            var Q242;
            {var subQ0=sQuery(id+"F0.wireOp",EDGE,"E12");var subQ1=sQuery(id+"F0.wireOp",EDGE,"E0.bottom");var subQ2=makeQuery(id+"F0.imprint","INTERSECT",VERTEX,{"derivedFrom":[subQ1,subQ0]});Q242=makeQuery(id+"F0.imprint","IMPRINT",FACE,{"disambiguationData":[TD([[makeQuery(id+"F0.imprint","IMPRINT",EDGE,{"disambiguationData":[TD([[subQ2,-1.0]])],"derivedFrom":subQ1}),-1.0]])]});}
            var Q243;
            {var subQ0=sQuery(id+"F0.wireOp",EDGE,"E6");var subQ1=sQuery(id+"F0.wireOp",EDGE,"E0.bottom");var subQ2=makeQuery(id+"F0.imprint","INTERSECT",VERTEX,{"derivedFrom":[subQ1,subQ0]});Q243=makeQuery(id+"F0.imprint","IMPRINT",FACE,{"disambiguationData":[TD([[makeQuery(id+"F0.imprint","IMPRINT",EDGE,{"disambiguationData":[TD([[subQ2,-1.0]])],"derivedFrom":subQ1}),-1.0]])]});}
            var Q244;
            {var subQ0=sQuery(id+"F0.wireOp",EDGE,"E10");var subQ1=sQuery(id+"F0.wireOp",EDGE,"E0.bottom");var subQ2=makeQuery(id+"F0.imprint","INTERSECT",VERTEX,{"derivedFrom":[subQ1,subQ0]});Q244=makeQuery(id+"F0.imprint","IMPRINT",FACE,{"disambiguationData":[TD([[makeQuery(id+"F0.imprint","IMPRINT",EDGE,{"disambiguationData":[TD([[subQ2,-1.0]])],"derivedFrom":subQ1}),-1.0]])]});}
            var Q245;
            {var subQ0=sQuery(id+"F0.wireOp",EDGE,"E34");var subQ1=sQuery(id+"F0.wireOp",EDGE,"E3");var subQ2=makeQuery(id+"F0.imprint","INTERSECT",VERTEX,{"derivedFrom":[subQ1,subQ0]});Q245=makeQuery(id+"F0.imprint","IMPRINT",FACE,{"disambiguationData":[TD([[makeQuery(id+"F0.imprint","IMPRINT",EDGE,{"disambiguationData":[TD([[subQ2,-1.0]])],"derivedFrom":subQ1}),1.0]])]});}
            var Q246;
            {var subQ0=sQuery(id+"F0.wireOp",EDGE,"E15");var subQ1=sQuery(id+"F0.wireOp",EDGE,"E0.top");var subQ2=makeQuery(id+"F0.imprint","INTERSECT",VERTEX,{"derivedFrom":[subQ1,subQ0]});Q246=makeQuery(id+"F0.imprint","IMPRINT",FACE,{"disambiguationData":[TD([[makeQuery(id+"F0.imprint","IMPRINT",EDGE,{"disambiguationData":[TD([[subQ2,-1.0]])],"derivedFrom":subQ1}),1.0]])]});}
            var Q247;
            {var subQ0=sQuery(id+"F0.wireOp",EDGE,"E28");var subQ1=sQuery(id+"F0.wireOp",EDGE,"E4");var subQ2=makeQuery(id+"F0.imprint","INTERSECT",VERTEX,{"derivedFrom":[subQ1,subQ0]});Q247=makeQuery(id+"F0.imprint","IMPRINT",FACE,{"disambiguationData":[TD([[makeQuery(id+"F0.imprint","IMPRINT",EDGE,{"disambiguationData":[TD([[subQ2,-1.0]])],"derivedFrom":subQ1}),1.0]])]});}
            var Q248;
            {var subQ0=sQuery(id+"F0.wireOp",EDGE,"E25");var subQ1=sQuery(id+"F0.wireOp",EDGE,"E0.right");var subQ2=makeQuery(id+"F0.imprint","INTERSECT",VERTEX,{"derivedFrom":[subQ1,subQ0]});Q248=makeQuery(id+"F0.imprint","IMPRINT",FACE,{"disambiguationData":[TD([[makeQuery(id+"F0.imprint","IMPRINT",EDGE,{"disambiguationData":[TD([[subQ2,-1.0]])],"derivedFrom":subQ1}),-1.0]])]});}
            var Q249;
            {var subQ0=sQuery(id+"F0.wireOp",EDGE,"E34");var subQ1=sQuery(id+"F0.wireOp",EDGE,"E4");var subQ2=makeQuery(id+"F0.imprint","INTERSECT",VERTEX,{"derivedFrom":[subQ1,subQ0]});Q249=makeQuery(id+"F0.imprint","IMPRINT",FACE,{"disambiguationData":[TD([[makeQuery(id+"F0.imprint","IMPRINT",EDGE,{"disambiguationData":[TD([[subQ2,-1.0]])],"derivedFrom":subQ1}),1.0]])]});}
            var Q250;
            {var subQ0=sQuery(id+"F0.wireOp",EDGE,"E0.right");var subQ1=sQuery(id+"F0.wireOp",EDGE,"E0.top");var subQ2=makeQuery(id+"F0.imprint","INTERSECT",VERTEX,{"derivedFrom":[subQ1,subQ0]});Q250=makeQuery(id+"F0.imprint","IMPRINT",FACE,{"disambiguationData":[TD([[makeQuery(id+"F0.imprint","IMPRINT",EDGE,{"disambiguationData":[TD([[subQ2,1.0]])],"derivedFrom":subQ1}),1.0]])]});}
            var Q251;
            {var subQ0=sQuery(id+"F0.wireOp",EDGE,"E0.right");var subQ1=sQuery(id+"F0.wireOp",EDGE,"E0.bottom");var subQ2=makeQuery(id+"F0.imprint","INTERSECT",VERTEX,{"derivedFrom":[subQ1,subQ0]});Q251=makeQuery(id+"F0.imprint","IMPRINT",FACE,{"disambiguationData":[TD([[makeQuery(id+"F0.imprint","IMPRINT",EDGE,{"disambiguationData":[TD([[subQ2,1.0]])],"derivedFrom":subQ1}),-1.0]])]});}
            var Q252;
            {var subQ0=sQuery(id+"F0.wireOp",EDGE,"E0.left");var subQ1=sQuery(id+"F0.wireOp",EDGE,"E0.top");var subQ2=makeQuery(id+"F0.imprint","INTERSECT",VERTEX,{"derivedFrom":[subQ1,subQ0]});Q252=makeQuery(id+"F0.imprint","IMPRINT",FACE,{"disambiguationData":[TD([[makeQuery(id+"F0.imprint","IMPRINT",EDGE,{"disambiguationData":[TD([[subQ2,-1.0]])],"derivedFrom":subQ1}),1.0]])]});}
            var Q253;
            {var subQ0=sQuery(id+"F0.wireOp",EDGE,"E0.left");var subQ1=sQuery(id+"F0.wireOp",EDGE,"E0.bottom");var subQ2=makeQuery(id+"F0.imprint","INTERSECT",VERTEX,{"derivedFrom":[subQ1,subQ0]});Q253=makeQuery(id+"F0.imprint","IMPRINT",FACE,{"disambiguationData":[TD([[makeQuery(id+"F0.imprint","IMPRINT",EDGE,{"disambiguationData":[TD([[subQ2,-1.0]])],"derivedFrom":subQ1}),-1.0]])]});}
            var Q254;
            {var subQ0=sQuery(id+"F0.wireOp",EDGE,"E21");var subQ1=sQuery(id+"F0.wireOp",EDGE,"E1");var subQ2=makeQuery(id+"F0.imprint","INTERSECT",VERTEX,{"derivedFrom":[subQ1,subQ0]});Q254=makeQuery(id+"F0.imprint","IMPRINT",FACE,{"disambiguationData":[TD([[makeQuery(id+"F0.imprint","IMPRINT",EDGE,{"disambiguationData":[TD([[subQ2,-1.0]])],"derivedFrom":subQ1}),1.0]])]});}
            var Q255;
            {var subQ0=sQuery(id+"F0.wireOp",EDGE,"E23");var subQ1=sQuery(id+"F0.wireOp",EDGE,"E1");var subQ2=makeQuery(id+"F0.imprint","INTERSECT",VERTEX,{"derivedFrom":[subQ1,subQ0]});Q255=makeQuery(id+"F0.imprint","IMPRINT",FACE,{"disambiguationData":[TD([[makeQuery(id+"F0.imprint","IMPRINT",EDGE,{"disambiguationData":[TD([[subQ2,-1.0]])],"derivedFrom":subQ1}),1.0]])]});}
            var Q256;
            {var subQ0=sQuery(id+"F0.wireOp",EDGE,"E31");var subQ1=sQuery(id+"F0.wireOp",EDGE,"E1");var subQ2=makeQuery(id+"F0.imprint","INTERSECT",VERTEX,{"derivedFrom":[subQ1,subQ0]});Q256=makeQuery(id+"F0.imprint","IMPRINT",FACE,{"disambiguationData":[TD([[makeQuery(id+"F0.imprint","IMPRINT",EDGE,{"disambiguationData":[TD([[subQ2,-1.0]])],"derivedFrom":subQ1}),1.0]])]});}
            var Q257;
            {var subQ0=sQuery(id+"F0.wireOp",EDGE,"E19");var subQ1=sQuery(id+"F0.wireOp",EDGE,"E1");var subQ2=makeQuery(id+"F0.imprint","INTERSECT",VERTEX,{"derivedFrom":[subQ1,subQ0]});Q257=makeQuery(id+"F0.imprint","IMPRINT",FACE,{"disambiguationData":[TD([[makeQuery(id+"F0.imprint","IMPRINT",EDGE,{"disambiguationData":[TD([[subQ2,-1.0]])],"derivedFrom":subQ1}),1.0]])]});}
            var Q258;
            {var subQ0=sQuery(id+"F0.wireOp",EDGE,"E35");var subQ1=sQuery(id+"F0.wireOp",EDGE,"E1");var subQ2=makeQuery(id+"F0.imprint","INTERSECT",VERTEX,{"derivedFrom":[subQ1,subQ0]});Q258=makeQuery(id+"F0.imprint","IMPRINT",FACE,{"disambiguationData":[TD([[makeQuery(id+"F0.imprint","IMPRINT",EDGE,{"disambiguationData":[TD([[subQ2,-1.0]])],"derivedFrom":subQ1}),1.0]])]});}
            var Q259;
            {var subQ0=sQuery(id+"F0.wireOp",EDGE,"E29");var subQ1=sQuery(id+"F0.wireOp",EDGE,"E1");var subQ2=makeQuery(id+"F0.imprint","INTERSECT",VERTEX,{"derivedFrom":[subQ1,subQ0]});Q259=makeQuery(id+"F0.imprint","IMPRINT",FACE,{"disambiguationData":[TD([[makeQuery(id+"F0.imprint","IMPRINT",EDGE,{"disambiguationData":[TD([[subQ2,-1.0]])],"derivedFrom":subQ1}),1.0]])]});}
            var Q260;
            {var subQ0=sQuery(id+"F0.wireOp",EDGE,"E33");var subQ1=sQuery(id+"F0.wireOp",EDGE,"E1");var subQ2=makeQuery(id+"F0.imprint","INTERSECT",VERTEX,{"derivedFrom":[subQ1,subQ0]});Q260=makeQuery(id+"F0.imprint","IMPRINT",FACE,{"disambiguationData":[TD([[makeQuery(id+"F0.imprint","IMPRINT",EDGE,{"disambiguationData":[TD([[subQ2,-1.0]])],"derivedFrom":subQ1}),1.0]])]});}
            var Q261;
            {var subQ0=sQuery(id+"F0.wireOp",EDGE,"E27");var subQ1=sQuery(id+"F0.wireOp",EDGE,"E1");var subQ2=makeQuery(id+"F0.imprint","INTERSECT",VERTEX,{"derivedFrom":[subQ1,subQ0]});Q261=makeQuery(id+"F0.imprint","IMPRINT",FACE,{"disambiguationData":[TD([[makeQuery(id+"F0.imprint","IMPRINT",EDGE,{"disambiguationData":[TD([[subQ2,-1.0]])],"derivedFrom":subQ1}),1.0]])]});}
            var Q262;
            {var subQ0=sQuery(id+"F0.wireOp",EDGE,"E25");var subQ1=sQuery(id+"F0.wireOp",EDGE,"E1");var subQ2=makeQuery(id+"F0.imprint","INTERSECT",VERTEX,{"derivedFrom":[subQ1,subQ0]});Q262=makeQuery(id+"F0.imprint","IMPRINT",FACE,{"disambiguationData":[TD([[makeQuery(id+"F0.imprint","IMPRINT",EDGE,{"disambiguationData":[TD([[subQ2,-1.0]])],"derivedFrom":subQ1}),1.0]])]});}
            var Q263;
            {var subQ0=sQuery(id+"F0.wireOp",EDGE,"E19");var subQ1=sQuery(id+"F0.wireOp",EDGE,"E17");var subQ2=makeQuery(id+"F0.imprint","INTERSECT",VERTEX,{"derivedFrom":[subQ1,subQ0]});Q263=makeQuery(id+"F0.imprint","IMPRINT",FACE,{"disambiguationData":[TD([[makeQuery(id+"F0.imprint","IMPRINT",EDGE,{"disambiguationData":[TD([[subQ2,-1.0]])],"derivedFrom":subQ1}),1.0]])]});}
            var Q264;
            {var subQ0=sQuery(id+"F0.wireOp",EDGE,"E21");var subQ1=sQuery(id+"F0.wireOp",EDGE,"E17");var subQ2=makeQuery(id+"F0.imprint","INTERSECT",VERTEX,{"derivedFrom":[subQ1,subQ0]});Q264=makeQuery(id+"F0.imprint","IMPRINT",FACE,{"disambiguationData":[TD([[makeQuery(id+"F0.imprint","IMPRINT",EDGE,{"disambiguationData":[TD([[subQ2,-1.0]])],"derivedFrom":subQ1}),1.0]])]});}
            var Q265;
            {var subQ0=sQuery(id+"F0.wireOp",EDGE,"E23");var subQ1=sQuery(id+"F0.wireOp",EDGE,"E17");var subQ2=makeQuery(id+"F0.imprint","INTERSECT",VERTEX,{"derivedFrom":[subQ1,subQ0]});Q265=makeQuery(id+"F0.imprint","IMPRINT",FACE,{"disambiguationData":[TD([[makeQuery(id+"F0.imprint","IMPRINT",EDGE,{"disambiguationData":[TD([[subQ2,-1.0]])],"derivedFrom":subQ1}),1.0]])]});}
            var Q266;
            {var subQ0=sQuery(id+"F0.wireOp",EDGE,"E25");var subQ1=sQuery(id+"F0.wireOp",EDGE,"E17");var subQ2=makeQuery(id+"F0.imprint","INTERSECT",VERTEX,{"derivedFrom":[subQ1,subQ0]});Q266=makeQuery(id+"F0.imprint","IMPRINT",FACE,{"disambiguationData":[TD([[makeQuery(id+"F0.imprint","IMPRINT",EDGE,{"disambiguationData":[TD([[subQ2,-1.0]])],"derivedFrom":subQ1}),1.0]])]});}
            var Q267;
            {var subQ0=sQuery(id+"F0.wireOp",EDGE,"E27");var subQ1=sQuery(id+"F0.wireOp",EDGE,"E17");var subQ2=makeQuery(id+"F0.imprint","INTERSECT",VERTEX,{"derivedFrom":[subQ1,subQ0]});Q267=makeQuery(id+"F0.imprint","IMPRINT",FACE,{"disambiguationData":[TD([[makeQuery(id+"F0.imprint","IMPRINT",EDGE,{"disambiguationData":[TD([[subQ2,-1.0]])],"derivedFrom":subQ1}),1.0]])]});}
            var Q268;
            {var subQ0=sQuery(id+"F0.wireOp",EDGE,"E29");var subQ1=sQuery(id+"F0.wireOp",EDGE,"E17");var subQ2=makeQuery(id+"F0.imprint","INTERSECT",VERTEX,{"derivedFrom":[subQ1,subQ0]});Q268=makeQuery(id+"F0.imprint","IMPRINT",FACE,{"disambiguationData":[TD([[makeQuery(id+"F0.imprint","IMPRINT",EDGE,{"disambiguationData":[TD([[subQ2,-1.0]])],"derivedFrom":subQ1}),1.0]])]});}
            var Q269;
            {var subQ0=sQuery(id+"F0.wireOp",EDGE,"E31");var subQ1=sQuery(id+"F0.wireOp",EDGE,"E17");var subQ2=makeQuery(id+"F0.imprint","INTERSECT",VERTEX,{"derivedFrom":[subQ1,subQ0]});Q269=makeQuery(id+"F0.imprint","IMPRINT",FACE,{"disambiguationData":[TD([[makeQuery(id+"F0.imprint","IMPRINT",EDGE,{"disambiguationData":[TD([[subQ2,-1.0]])],"derivedFrom":subQ1}),1.0]])]});}
            var Q270;
            {var subQ0=sQuery(id+"F0.wireOp",EDGE,"E33");var subQ1=sQuery(id+"F0.wireOp",EDGE,"E17");var subQ2=makeQuery(id+"F0.imprint","INTERSECT",VERTEX,{"derivedFrom":[subQ1,subQ0]});Q270=makeQuery(id+"F0.imprint","IMPRINT",FACE,{"disambiguationData":[TD([[makeQuery(id+"F0.imprint","IMPRINT",EDGE,{"disambiguationData":[TD([[subQ2,-1.0]])],"derivedFrom":subQ1}),1.0]])]});}
            var Q271;
            {var subQ0=sQuery(id+"F0.wireOp",EDGE,"E35");var subQ1=sQuery(id+"F0.wireOp",EDGE,"E17");var subQ2=makeQuery(id+"F0.imprint","INTERSECT",VERTEX,{"derivedFrom":[subQ1,subQ0]});Q271=makeQuery(id+"F0.imprint","IMPRINT",FACE,{"disambiguationData":[TD([[makeQuery(id+"F0.imprint","IMPRINT",EDGE,{"disambiguationData":[TD([[subQ2,-1.0]])],"derivedFrom":subQ1}),1.0]])]});}
            var Q272;
            {var subQ0=sQuery(id+"F0.wireOp",EDGE,"E21");var subQ1=sQuery(id+"F0.wireOp",EDGE,"E5");var subQ2=makeQuery(id+"F0.imprint","INTERSECT",VERTEX,{"derivedFrom":[subQ1,subQ0]});Q272=makeQuery(id+"F0.imprint","IMPRINT",FACE,{"disambiguationData":[TD([[makeQuery(id+"F0.imprint","IMPRINT",EDGE,{"disambiguationData":[TD([[subQ2,-1.0]])],"derivedFrom":subQ1}),1.0]])]});}
            var Q273;
            {var subQ0=sQuery(id+"F0.wireOp",EDGE,"E21");var subQ1=sQuery(id+"F0.wireOp",EDGE,"E7");var subQ2=makeQuery(id+"F0.imprint","INTERSECT",VERTEX,{"derivedFrom":[subQ1,subQ0]});Q273=makeQuery(id+"F0.imprint","IMPRINT",FACE,{"disambiguationData":[TD([[makeQuery(id+"F0.imprint","IMPRINT",EDGE,{"disambiguationData":[TD([[subQ2,-1.0]])],"derivedFrom":subQ1}),1.0]])]});}
            var Q274;
            {var subQ0=sQuery(id+"F0.wireOp",EDGE,"E21");var subQ1=sQuery(id+"F0.wireOp",EDGE,"E9");var subQ2=makeQuery(id+"F0.imprint","INTERSECT",VERTEX,{"derivedFrom":[subQ1,subQ0]});Q274=makeQuery(id+"F0.imprint","IMPRINT",FACE,{"disambiguationData":[TD([[makeQuery(id+"F0.imprint","IMPRINT",EDGE,{"disambiguationData":[TD([[subQ2,-1.0]])],"derivedFrom":subQ1}),1.0]])]});}
            var Q275;
            {var subQ0=sQuery(id+"F0.wireOp",EDGE,"E21");var subQ1=sQuery(id+"F0.wireOp",EDGE,"E11");var subQ2=makeQuery(id+"F0.imprint","INTERSECT",VERTEX,{"derivedFrom":[subQ1,subQ0]});Q275=makeQuery(id+"F0.imprint","IMPRINT",FACE,{"disambiguationData":[TD([[makeQuery(id+"F0.imprint","IMPRINT",EDGE,{"disambiguationData":[TD([[subQ2,-1.0]])],"derivedFrom":subQ1}),1.0]])]});}
            var Q276;
            {var subQ0=sQuery(id+"F0.wireOp",EDGE,"E21");var subQ1=sQuery(id+"F0.wireOp",EDGE,"E13");var subQ2=makeQuery(id+"F0.imprint","INTERSECT",VERTEX,{"derivedFrom":[subQ1,subQ0]});Q276=makeQuery(id+"F0.imprint","IMPRINT",FACE,{"disambiguationData":[TD([[makeQuery(id+"F0.imprint","IMPRINT",EDGE,{"disambiguationData":[TD([[subQ2,-1.0]])],"derivedFrom":subQ1}),1.0]])]});}
            var Q277;
            {var subQ0=sQuery(id+"F0.wireOp",EDGE,"E21");var subQ1=sQuery(id+"F0.wireOp",EDGE,"E15");var subQ2=makeQuery(id+"F0.imprint","INTERSECT",VERTEX,{"derivedFrom":[subQ1,subQ0]});Q277=makeQuery(id+"F0.imprint","IMPRINT",FACE,{"disambiguationData":[TD([[makeQuery(id+"F0.imprint","IMPRINT",EDGE,{"disambiguationData":[TD([[subQ2,-1.0]])],"derivedFrom":subQ1}),1.0]])]});}
            var Q278;
            {var subQ0=sQuery(id+"F0.wireOp",EDGE,"E19");var subQ1=sQuery(id+"F0.wireOp",EDGE,"E15");var subQ2=makeQuery(id+"F0.imprint","INTERSECT",VERTEX,{"derivedFrom":[subQ1,subQ0]});Q278=makeQuery(id+"F0.imprint","IMPRINT",FACE,{"disambiguationData":[TD([[makeQuery(id+"F0.imprint","IMPRINT",EDGE,{"disambiguationData":[TD([[subQ2,-1.0]])],"derivedFrom":subQ1}),1.0]])]});}
            var Q279;
            {var subQ0=sQuery(id+"F0.wireOp",EDGE,"E23");var subQ1=sQuery(id+"F0.wireOp",EDGE,"E15");var subQ2=makeQuery(id+"F0.imprint","INTERSECT",VERTEX,{"derivedFrom":[subQ1,subQ0]});Q279=makeQuery(id+"F0.imprint","IMPRINT",FACE,{"disambiguationData":[TD([[makeQuery(id+"F0.imprint","IMPRINT",EDGE,{"disambiguationData":[TD([[subQ2,-1.0]])],"derivedFrom":subQ1}),1.0]])]});}
            var Q280;
            {var subQ0=sQuery(id+"F0.wireOp",EDGE,"E25");var subQ1=sQuery(id+"F0.wireOp",EDGE,"E15");var subQ2=makeQuery(id+"F0.imprint","INTERSECT",VERTEX,{"derivedFrom":[subQ1,subQ0]});Q280=makeQuery(id+"F0.imprint","IMPRINT",FACE,{"disambiguationData":[TD([[makeQuery(id+"F0.imprint","IMPRINT",EDGE,{"disambiguationData":[TD([[subQ2,-1.0]])],"derivedFrom":subQ1}),1.0]])]});}
            var Q281;
            {var subQ0=sQuery(id+"F0.wireOp",EDGE,"E27");var subQ1=sQuery(id+"F0.wireOp",EDGE,"E15");var subQ2=makeQuery(id+"F0.imprint","INTERSECT",VERTEX,{"derivedFrom":[subQ1,subQ0]});Q281=makeQuery(id+"F0.imprint","IMPRINT",FACE,{"disambiguationData":[TD([[makeQuery(id+"F0.imprint","IMPRINT",EDGE,{"disambiguationData":[TD([[subQ2,-1.0]])],"derivedFrom":subQ1}),1.0]])]});}
            var Q282;
            {var subQ0=sQuery(id+"F0.wireOp",EDGE,"E29");var subQ1=sQuery(id+"F0.wireOp",EDGE,"E15");var subQ2=makeQuery(id+"F0.imprint","INTERSECT",VERTEX,{"derivedFrom":[subQ1,subQ0]});Q282=makeQuery(id+"F0.imprint","IMPRINT",FACE,{"disambiguationData":[TD([[makeQuery(id+"F0.imprint","IMPRINT",EDGE,{"disambiguationData":[TD([[subQ2,-1.0]])],"derivedFrom":subQ1}),1.0]])]});}
            var Q283;
            {var subQ0=sQuery(id+"F0.wireOp",EDGE,"E31");var subQ1=sQuery(id+"F0.wireOp",EDGE,"E15");var subQ2=makeQuery(id+"F0.imprint","INTERSECT",VERTEX,{"derivedFrom":[subQ1,subQ0]});Q283=makeQuery(id+"F0.imprint","IMPRINT",FACE,{"disambiguationData":[TD([[makeQuery(id+"F0.imprint","IMPRINT",EDGE,{"disambiguationData":[TD([[subQ2,-1.0]])],"derivedFrom":subQ1}),1.0]])]});}
            var Q284;
            {var subQ0=sQuery(id+"F0.wireOp",EDGE,"E33");var subQ1=sQuery(id+"F0.wireOp",EDGE,"E15");var subQ2=makeQuery(id+"F0.imprint","INTERSECT",VERTEX,{"derivedFrom":[subQ1,subQ0]});Q284=makeQuery(id+"F0.imprint","IMPRINT",FACE,{"disambiguationData":[TD([[makeQuery(id+"F0.imprint","IMPRINT",EDGE,{"disambiguationData":[TD([[subQ2,-1.0]])],"derivedFrom":subQ1}),1.0]])]});}
            var Q285;
            {var subQ0=sQuery(id+"F0.wireOp",EDGE,"E35");var subQ1=sQuery(id+"F0.wireOp",EDGE,"E15");var subQ2=makeQuery(id+"F0.imprint","INTERSECT",VERTEX,{"derivedFrom":[subQ1,subQ0]});Q285=makeQuery(id+"F0.imprint","IMPRINT",FACE,{"disambiguationData":[TD([[makeQuery(id+"F0.imprint","IMPRINT",EDGE,{"disambiguationData":[TD([[subQ2,-1.0]])],"derivedFrom":subQ1}),1.0]])]});}
            var Q286;
            {var subQ0=sQuery(id+"F0.wireOp",EDGE,"E23");var subQ1=sQuery(id+"F0.wireOp",EDGE,"E5");var subQ2=makeQuery(id+"F0.imprint","INTERSECT",VERTEX,{"derivedFrom":[subQ1,subQ0]});Q286=makeQuery(id+"F0.imprint","IMPRINT",FACE,{"disambiguationData":[TD([[makeQuery(id+"F0.imprint","IMPRINT",EDGE,{"disambiguationData":[TD([[subQ2,-1.0]])],"derivedFrom":subQ1}),1.0]])]});}
            var Q287;
            {var subQ0=sQuery(id+"F0.wireOp",EDGE,"E23");var subQ1=sQuery(id+"F0.wireOp",EDGE,"E7");var subQ2=makeQuery(id+"F0.imprint","INTERSECT",VERTEX,{"derivedFrom":[subQ1,subQ0]});Q287=makeQuery(id+"F0.imprint","IMPRINT",FACE,{"disambiguationData":[TD([[makeQuery(id+"F0.imprint","IMPRINT",EDGE,{"disambiguationData":[TD([[subQ2,-1.0]])],"derivedFrom":subQ1}),1.0]])]});}
            var Q288;
            {var subQ0=sQuery(id+"F0.wireOp",EDGE,"E23");var subQ1=sQuery(id+"F0.wireOp",EDGE,"E11");var subQ2=makeQuery(id+"F0.imprint","INTERSECT",VERTEX,{"derivedFrom":[subQ1,subQ0]});Q288=makeQuery(id+"F0.imprint","IMPRINT",FACE,{"disambiguationData":[TD([[makeQuery(id+"F0.imprint","IMPRINT",EDGE,{"disambiguationData":[TD([[subQ2,-1.0]])],"derivedFrom":subQ1}),1.0]])]});}
            var Q289;
            {var subQ0=sQuery(id+"F0.wireOp",EDGE,"E23");var subQ1=sQuery(id+"F0.wireOp",EDGE,"E13");var subQ2=makeQuery(id+"F0.imprint","INTERSECT",VERTEX,{"derivedFrom":[subQ1,subQ0]});Q289=makeQuery(id+"F0.imprint","IMPRINT",FACE,{"disambiguationData":[TD([[makeQuery(id+"F0.imprint","IMPRINT",EDGE,{"disambiguationData":[TD([[subQ2,-1.0]])],"derivedFrom":subQ1}),1.0]])]});}
            var Q290;
            {var subQ0=sQuery(id+"F0.wireOp",EDGE,"E19");var subQ1=sQuery(id+"F0.wireOp",EDGE,"E13");var subQ2=makeQuery(id+"F0.imprint","INTERSECT",VERTEX,{"derivedFrom":[subQ1,subQ0]});Q290=makeQuery(id+"F0.imprint","IMPRINT",FACE,{"disambiguationData":[TD([[makeQuery(id+"F0.imprint","IMPRINT",EDGE,{"disambiguationData":[TD([[subQ2,-1.0]])],"derivedFrom":subQ1}),1.0]])]});}
            var Q291;
            {var subQ0=sQuery(id+"F0.wireOp",EDGE,"E25");var subQ1=sQuery(id+"F0.wireOp",EDGE,"E13");var subQ2=makeQuery(id+"F0.imprint","INTERSECT",VERTEX,{"derivedFrom":[subQ1,subQ0]});Q291=makeQuery(id+"F0.imprint","IMPRINT",FACE,{"disambiguationData":[TD([[makeQuery(id+"F0.imprint","IMPRINT",EDGE,{"disambiguationData":[TD([[subQ2,-1.0]])],"derivedFrom":subQ1}),1.0]])]});}
            var Q292;
            {var subQ0=sQuery(id+"F0.wireOp",EDGE,"E25");var subQ1=sQuery(id+"F0.wireOp",EDGE,"E11");var subQ2=makeQuery(id+"F0.imprint","INTERSECT",VERTEX,{"derivedFrom":[subQ1,subQ0]});Q292=makeQuery(id+"F0.imprint","IMPRINT",FACE,{"disambiguationData":[TD([[makeQuery(id+"F0.imprint","IMPRINT",EDGE,{"disambiguationData":[TD([[subQ2,-1.0]])],"derivedFrom":subQ1}),1.0]])]});}
            var Q293;
            {var subQ0=sQuery(id+"F0.wireOp",EDGE,"E19");var subQ1=sQuery(id+"F0.wireOp",EDGE,"E7");var subQ2=makeQuery(id+"F0.imprint","INTERSECT",VERTEX,{"derivedFrom":[subQ1,subQ0]});Q293=makeQuery(id+"F0.imprint","IMPRINT",FACE,{"disambiguationData":[TD([[makeQuery(id+"F0.imprint","IMPRINT",EDGE,{"disambiguationData":[TD([[subQ2,-1.0]])],"derivedFrom":subQ1}),1.0]])]});}
            var Q294;
            {var subQ0=sQuery(id+"F0.wireOp",EDGE,"E33");var subQ1=sQuery(id+"F0.wireOp",EDGE,"E7");var subQ2=makeQuery(id+"F0.imprint","INTERSECT",VERTEX,{"derivedFrom":[subQ1,subQ0]});Q294=makeQuery(id+"F0.imprint","IMPRINT",FACE,{"disambiguationData":[TD([[makeQuery(id+"F0.imprint","IMPRINT",EDGE,{"disambiguationData":[TD([[subQ2,-1.0]])],"derivedFrom":subQ1}),1.0]])]});}
            var Q295;
            {var subQ0=sQuery(id+"F0.wireOp",EDGE,"E35");var subQ1=sQuery(id+"F0.wireOp",EDGE,"E7");var subQ2=makeQuery(id+"F0.imprint","INTERSECT",VERTEX,{"derivedFrom":[subQ1,subQ0]});Q295=makeQuery(id+"F0.imprint","IMPRINT",FACE,{"disambiguationData":[TD([[makeQuery(id+"F0.imprint","IMPRINT",EDGE,{"disambiguationData":[TD([[subQ2,-1.0]])],"derivedFrom":subQ1}),1.0]])]});}
            var Q296;
            {var subQ0=sQuery(id+"F0.wireOp",EDGE,"E27");var subQ1=sQuery(id+"F0.wireOp",EDGE,"E11");var subQ2=makeQuery(id+"F0.imprint","INTERSECT",VERTEX,{"derivedFrom":[subQ1,subQ0]});Q296=makeQuery(id+"F0.imprint","IMPRINT",FACE,{"disambiguationData":[TD([[makeQuery(id+"F0.imprint","IMPRINT",EDGE,{"disambiguationData":[TD([[subQ2,-1.0]])],"derivedFrom":subQ1}),1.0]])]});}
            var Q297;
            {var subQ0=sQuery(id+"F0.wireOp",EDGE,"E27");var subQ1=sQuery(id+"F0.wireOp",EDGE,"E13");var subQ2=makeQuery(id+"F0.imprint","INTERSECT",VERTEX,{"derivedFrom":[subQ1,subQ0]});Q297=makeQuery(id+"F0.imprint","IMPRINT",FACE,{"disambiguationData":[TD([[makeQuery(id+"F0.imprint","IMPRINT",EDGE,{"disambiguationData":[TD([[subQ2,-1.0]])],"derivedFrom":subQ1}),1.0]])]});}
            var Q298;
            {var subQ0=sQuery(id+"F0.wireOp",EDGE,"E19");var subQ1=sQuery(id+"F0.wireOp",EDGE,"E5");var subQ2=makeQuery(id+"F0.imprint","INTERSECT",VERTEX,{"derivedFrom":[subQ1,subQ0]});Q298=makeQuery(id+"F0.imprint","IMPRINT",FACE,{"disambiguationData":[TD([[makeQuery(id+"F0.imprint","IMPRINT",EDGE,{"disambiguationData":[TD([[subQ2,-1.0]])],"derivedFrom":subQ1}),1.0]])]});}
            var Q299;
            {var subQ0=sQuery(id+"F0.wireOp",EDGE,"E33");var subQ1=sQuery(id+"F0.wireOp",EDGE,"E5");var subQ2=makeQuery(id+"F0.imprint","INTERSECT",VERTEX,{"derivedFrom":[subQ1,subQ0]});Q299=makeQuery(id+"F0.imprint","IMPRINT",FACE,{"disambiguationData":[TD([[makeQuery(id+"F0.imprint","IMPRINT",EDGE,{"disambiguationData":[TD([[subQ2,-1.0]])],"derivedFrom":subQ1}),1.0]])]});}
            var Q300;
            {var subQ0=sQuery(id+"F0.wireOp",EDGE,"E19");var subQ1=sQuery(id+"F0.wireOp",EDGE,"E9");var subQ2=makeQuery(id+"F0.imprint","INTERSECT",VERTEX,{"derivedFrom":[subQ1,subQ0]});Q300=makeQuery(id+"F0.imprint","IMPRINT",FACE,{"disambiguationData":[TD([[makeQuery(id+"F0.imprint","IMPRINT",EDGE,{"disambiguationData":[TD([[subQ2,-1.0]])],"derivedFrom":subQ1}),1.0]])]});}
            var Q301;
            {var subQ0=sQuery(id+"F0.wireOp",EDGE,"E31");var subQ1=sQuery(id+"F0.wireOp",EDGE,"E9");var subQ2=makeQuery(id+"F0.imprint","INTERSECT",VERTEX,{"derivedFrom":[subQ1,subQ0]});Q301=makeQuery(id+"F0.imprint","IMPRINT",FACE,{"disambiguationData":[TD([[makeQuery(id+"F0.imprint","IMPRINT",EDGE,{"disambiguationData":[TD([[subQ2,-1.0]])],"derivedFrom":subQ1}),1.0]])]});}
            var Q302;
            {var subQ0=sQuery(id+"F0.wireOp",EDGE,"E35");var subQ1=sQuery(id+"F0.wireOp",EDGE,"E5");var subQ2=makeQuery(id+"F0.imprint","INTERSECT",VERTEX,{"derivedFrom":[subQ1,subQ0]});Q302=makeQuery(id+"F0.imprint","IMPRINT",FACE,{"disambiguationData":[TD([[makeQuery(id+"F0.imprint","IMPRINT",EDGE,{"disambiguationData":[TD([[subQ2,-1.0]])],"derivedFrom":subQ1}),1.0]])]});}
            var Q303;
            {var subQ0=sQuery(id+"F0.wireOp",EDGE,"E31");var subQ1=sQuery(id+"F0.wireOp",EDGE,"E5");var subQ2=makeQuery(id+"F0.imprint","INTERSECT",VERTEX,{"derivedFrom":[subQ1,subQ0]});Q303=makeQuery(id+"F0.imprint","IMPRINT",FACE,{"disambiguationData":[TD([[makeQuery(id+"F0.imprint","IMPRINT",EDGE,{"disambiguationData":[TD([[subQ2,-1.0]])],"derivedFrom":subQ1}),1.0]])]});}
            var Q304;
            {var subQ0=sQuery(id+"F0.wireOp",EDGE,"E31");var subQ1=sQuery(id+"F0.wireOp",EDGE,"E11");var subQ2=makeQuery(id+"F0.imprint","INTERSECT",VERTEX,{"derivedFrom":[subQ1,subQ0]});Q304=makeQuery(id+"F0.imprint","IMPRINT",FACE,{"disambiguationData":[TD([[makeQuery(id+"F0.imprint","IMPRINT",EDGE,{"disambiguationData":[TD([[subQ2,-1.0]])],"derivedFrom":subQ1}),1.0]])]});}
            var Q305;
            {var subQ0=sQuery(id+"F0.wireOp",EDGE,"E35");var subQ1=sQuery(id+"F0.wireOp",EDGE,"E9");var subQ2=makeQuery(id+"F0.imprint","INTERSECT",VERTEX,{"derivedFrom":[subQ1,subQ0]});Q305=makeQuery(id+"F0.imprint","IMPRINT",FACE,{"disambiguationData":[TD([[makeQuery(id+"F0.imprint","IMPRINT",EDGE,{"disambiguationData":[TD([[subQ2,-1.0]])],"derivedFrom":subQ1}),1.0]])]});}
            var Q306;
            {var subQ0=sQuery(id+"F0.wireOp",EDGE,"E31");var subQ1=sQuery(id+"F0.wireOp",EDGE,"E7");var subQ2=makeQuery(id+"F0.imprint","INTERSECT",VERTEX,{"derivedFrom":[subQ1,subQ0]});Q306=makeQuery(id+"F0.imprint","IMPRINT",FACE,{"disambiguationData":[TD([[makeQuery(id+"F0.imprint","IMPRINT",EDGE,{"disambiguationData":[TD([[subQ2,-1.0]])],"derivedFrom":subQ1}),1.0]])]});}
            var Q307;
            {var subQ0=sQuery(id+"F0.wireOp",EDGE,"E31");var subQ1=sQuery(id+"F0.wireOp",EDGE,"E13");var subQ2=makeQuery(id+"F0.imprint","INTERSECT",VERTEX,{"derivedFrom":[subQ1,subQ0]});Q307=makeQuery(id+"F0.imprint","IMPRINT",FACE,{"disambiguationData":[TD([[makeQuery(id+"F0.imprint","IMPRINT",EDGE,{"disambiguationData":[TD([[subQ2,-1.0]])],"derivedFrom":subQ1}),1.0]])]});}
            var Q308;
            {var subQ0=sQuery(id+"F0.wireOp",EDGE,"E25");var subQ1=sQuery(id+"F0.wireOp",EDGE,"E5");var subQ2=makeQuery(id+"F0.imprint","INTERSECT",VERTEX,{"derivedFrom":[subQ1,subQ0]});Q308=makeQuery(id+"F0.imprint","IMPRINT",FACE,{"disambiguationData":[TD([[makeQuery(id+"F0.imprint","IMPRINT",EDGE,{"disambiguationData":[TD([[subQ2,-1.0]])],"derivedFrom":subQ1}),1.0]])]});}
            var Q309;
            {var subQ0=sQuery(id+"F0.wireOp",EDGE,"E29");var subQ1=sQuery(id+"F0.wireOp",EDGE,"E5");var subQ2=makeQuery(id+"F0.imprint","INTERSECT",VERTEX,{"derivedFrom":[subQ1,subQ0]});Q309=makeQuery(id+"F0.imprint","IMPRINT",FACE,{"disambiguationData":[TD([[makeQuery(id+"F0.imprint","IMPRINT",EDGE,{"disambiguationData":[TD([[subQ2,-1.0]])],"derivedFrom":subQ1}),1.0]])]});}
            var Q310;
            {var subQ0=sQuery(id+"F0.wireOp",EDGE,"E29");var subQ1=sQuery(id+"F0.wireOp",EDGE,"E11");var subQ2=makeQuery(id+"F0.imprint","INTERSECT",VERTEX,{"derivedFrom":[subQ1,subQ0]});Q310=makeQuery(id+"F0.imprint","IMPRINT",FACE,{"disambiguationData":[TD([[makeQuery(id+"F0.imprint","IMPRINT",EDGE,{"disambiguationData":[TD([[subQ2,-1.0]])],"derivedFrom":subQ1}),1.0]])]});}
            var Q311;
            {var subQ0=sQuery(id+"F0.wireOp",EDGE,"E29");var subQ1=sQuery(id+"F0.wireOp",EDGE,"E7");var subQ2=makeQuery(id+"F0.imprint","INTERSECT",VERTEX,{"derivedFrom":[subQ1,subQ0]});Q311=makeQuery(id+"F0.imprint","IMPRINT",FACE,{"disambiguationData":[TD([[makeQuery(id+"F0.imprint","IMPRINT",EDGE,{"disambiguationData":[TD([[subQ2,-1.0]])],"derivedFrom":subQ1}),1.0]])]});}
            var Q312;
            {var subQ0=sQuery(id+"F0.wireOp",EDGE,"E29");var subQ1=sQuery(id+"F0.wireOp",EDGE,"E13");var subQ2=makeQuery(id+"F0.imprint","INTERSECT",VERTEX,{"derivedFrom":[subQ1,subQ0]});Q312=makeQuery(id+"F0.imprint","IMPRINT",FACE,{"disambiguationData":[TD([[makeQuery(id+"F0.imprint","IMPRINT",EDGE,{"disambiguationData":[TD([[subQ2,-1.0]])],"derivedFrom":subQ1}),1.0]])]});}
            var Q313;
            {var subQ0=sQuery(id+"F0.wireOp",EDGE,"E33");var subQ1=sQuery(id+"F0.wireOp",EDGE,"E9");var subQ2=makeQuery(id+"F0.imprint","INTERSECT",VERTEX,{"derivedFrom":[subQ1,subQ0]});Q313=makeQuery(id+"F0.imprint","IMPRINT",FACE,{"disambiguationData":[TD([[makeQuery(id+"F0.imprint","IMPRINT",EDGE,{"disambiguationData":[TD([[subQ2,-1.0]])],"derivedFrom":subQ1}),1.0]])]});}
            var Q314;
            {var subQ0=sQuery(id+"F0.wireOp",EDGE,"E29");var subQ1=sQuery(id+"F0.wireOp",EDGE,"E9");var subQ2=makeQuery(id+"F0.imprint","INTERSECT",VERTEX,{"derivedFrom":[subQ1,subQ0]});Q314=makeQuery(id+"F0.imprint","IMPRINT",FACE,{"disambiguationData":[TD([[makeQuery(id+"F0.imprint","IMPRINT",EDGE,{"disambiguationData":[TD([[subQ2,-1.0]])],"derivedFrom":subQ1}),1.0]])]});}
            var Q315;
            {var subQ0=sQuery(id+"F0.wireOp",EDGE,"E27");var subQ1=sQuery(id+"F0.wireOp",EDGE,"E7");var subQ2=makeQuery(id+"F0.imprint","INTERSECT",VERTEX,{"derivedFrom":[subQ1,subQ0]});Q315=makeQuery(id+"F0.imprint","IMPRINT",FACE,{"disambiguationData":[TD([[makeQuery(id+"F0.imprint","IMPRINT",EDGE,{"disambiguationData":[TD([[subQ2,-1.0]])],"derivedFrom":subQ1}),1.0]])]});}
            var Q316;
            {var subQ0=sQuery(id+"F0.wireOp",EDGE,"E27");var subQ1=sQuery(id+"F0.wireOp",EDGE,"E5");var subQ2=makeQuery(id+"F0.imprint","INTERSECT",VERTEX,{"derivedFrom":[subQ1,subQ0]});Q316=makeQuery(id+"F0.imprint","IMPRINT",FACE,{"disambiguationData":[TD([[makeQuery(id+"F0.imprint","IMPRINT",EDGE,{"disambiguationData":[TD([[subQ2,-1.0]])],"derivedFrom":subQ1}),1.0]])]});}
            var Q317;
            {var subQ0=sQuery(id+"F0.wireOp",EDGE,"E35");var subQ1=sQuery(id+"F0.wireOp",EDGE,"E11");var subQ2=makeQuery(id+"F0.imprint","INTERSECT",VERTEX,{"derivedFrom":[subQ1,subQ0]});Q317=makeQuery(id+"F0.imprint","IMPRINT",FACE,{"disambiguationData":[TD([[makeQuery(id+"F0.imprint","IMPRINT",EDGE,{"disambiguationData":[TD([[subQ2,-1.0]])],"derivedFrom":subQ1}),1.0]])]});}
            var Q318;
            {var subQ0=sQuery(id+"F0.wireOp",EDGE,"E33");var subQ1=sQuery(id+"F0.wireOp",EDGE,"E11");var subQ2=makeQuery(id+"F0.imprint","INTERSECT",VERTEX,{"derivedFrom":[subQ1,subQ0]});Q318=makeQuery(id+"F0.imprint","IMPRINT",FACE,{"disambiguationData":[TD([[makeQuery(id+"F0.imprint","IMPRINT",EDGE,{"disambiguationData":[TD([[subQ2,-1.0]])],"derivedFrom":subQ1}),1.0]])]});}
            var Q319;
            {var subQ0=sQuery(id+"F0.wireOp",EDGE,"E19");var subQ1=sQuery(id+"F0.wireOp",EDGE,"E11");var subQ2=makeQuery(id+"F0.imprint","INTERSECT",VERTEX,{"derivedFrom":[subQ1,subQ0]});Q319=makeQuery(id+"F0.imprint","IMPRINT",FACE,{"disambiguationData":[TD([[makeQuery(id+"F0.imprint","IMPRINT",EDGE,{"disambiguationData":[TD([[subQ2,-1.0]])],"derivedFrom":subQ1}),1.0]])]});}
            var Q320;
            {var subQ0=sQuery(id+"F0.wireOp",EDGE,"E25");var subQ1=sQuery(id+"F0.wireOp",EDGE,"E7");var subQ2=makeQuery(id+"F0.imprint","INTERSECT",VERTEX,{"derivedFrom":[subQ1,subQ0]});Q320=makeQuery(id+"F0.imprint","IMPRINT",FACE,{"disambiguationData":[TD([[makeQuery(id+"F0.imprint","IMPRINT",EDGE,{"disambiguationData":[TD([[subQ2,-1.0]])],"derivedFrom":subQ1}),1.0]])]});}
            var Q321;
            {var subQ0=sQuery(id+"F0.wireOp",EDGE,"E35");var subQ1=sQuery(id+"F0.wireOp",EDGE,"E13");var subQ2=makeQuery(id+"F0.imprint","INTERSECT",VERTEX,{"derivedFrom":[subQ1,subQ0]});Q321=makeQuery(id+"F0.imprint","IMPRINT",FACE,{"disambiguationData":[TD([[makeQuery(id+"F0.imprint","IMPRINT",EDGE,{"disambiguationData":[TD([[subQ2,-1.0]])],"derivedFrom":subQ1}),1.0]])]});}
            var Q322;
            {var subQ0=sQuery(id+"F0.wireOp",EDGE,"E33");var subQ1=sQuery(id+"F0.wireOp",EDGE,"E13");var subQ2=makeQuery(id+"F0.imprint","INTERSECT",VERTEX,{"derivedFrom":[subQ1,subQ0]});Q322=makeQuery(id+"F0.imprint","IMPRINT",FACE,{"disambiguationData":[TD([[makeQuery(id+"F0.imprint","IMPRINT",EDGE,{"disambiguationData":[TD([[subQ2,-1.0]])],"derivedFrom":subQ1}),1.0]])]});}
            var Q323;
            {var subQ0=sQuery(id+"F0.wireOp",EDGE,"E27");var subQ1=sQuery(id+"F0.wireOp",EDGE,"E9");var subQ2=makeQuery(id+"F0.imprint","INTERSECT",VERTEX,{"derivedFrom":[subQ1,subQ0]});Q323=makeQuery(id+"F0.imprint","IMPRINT",FACE,{"disambiguationData":[TD([[makeQuery(id+"F0.imprint","IMPRINT",EDGE,{"disambiguationData":[TD([[subQ2,-1.0]])],"derivedFrom":subQ1}),1.0]])]});}
            var Q324;
            {var subQ0=sQuery(id+"F0.wireOp",EDGE,"E31");var subQ1=sQuery(id+"F0.wireOp",EDGE,"E3");var subQ2=makeQuery(id+"F0.imprint","INTERSECT",VERTEX,{"derivedFrom":[subQ1,subQ0]});Q324=makeQuery(id+"F0.imprint","IMPRINT",FACE,{"disambiguationData":[TD([[makeQuery(id+"F0.imprint","IMPRINT",EDGE,{"disambiguationData":[TD([[subQ2,-1.0]])],"derivedFrom":subQ1}),1.0]])]});}
            var Q325;
            {var subQ0=sQuery(id+"F0.wireOp",EDGE,"E27");var subQ1=sQuery(id+"F0.wireOp",EDGE,"E3");var subQ2=makeQuery(id+"F0.imprint","INTERSECT",VERTEX,{"derivedFrom":[subQ1,subQ0]});Q325=makeQuery(id+"F0.imprint","IMPRINT",FACE,{"disambiguationData":[TD([[makeQuery(id+"F0.imprint","IMPRINT",EDGE,{"disambiguationData":[TD([[subQ2,-1.0]])],"derivedFrom":subQ1}),1.0]])]});}
            var Q326;
            {var subQ0=sQuery(id+"F0.wireOp",EDGE,"E35");var subQ1=sQuery(id+"F0.wireOp",EDGE,"E3");var subQ2=makeQuery(id+"F0.imprint","INTERSECT",VERTEX,{"derivedFrom":[subQ1,subQ0]});Q326=makeQuery(id+"F0.imprint","IMPRINT",FACE,{"disambiguationData":[TD([[makeQuery(id+"F0.imprint","IMPRINT",EDGE,{"disambiguationData":[TD([[subQ2,-1.0]])],"derivedFrom":subQ1}),1.0]])]});}
            var Q327;
            {var subQ0=sQuery(id+"F0.wireOp",EDGE,"E33");var subQ1=sQuery(id+"F0.wireOp",EDGE,"E3");var subQ2=makeQuery(id+"F0.imprint","INTERSECT",VERTEX,{"derivedFrom":[subQ1,subQ0]});Q327=makeQuery(id+"F0.imprint","IMPRINT",FACE,{"disambiguationData":[TD([[makeQuery(id+"F0.imprint","IMPRINT",EDGE,{"disambiguationData":[TD([[subQ2,-1.0]])],"derivedFrom":subQ1}),1.0]])]});}
            var Q328;
            {var subQ0=sQuery(id+"F0.wireOp",EDGE,"E29");var subQ1=sQuery(id+"F0.wireOp",EDGE,"E3");var subQ2=makeQuery(id+"F0.imprint","INTERSECT",VERTEX,{"derivedFrom":[subQ1,subQ0]});Q328=makeQuery(id+"F0.imprint","IMPRINT",FACE,{"disambiguationData":[TD([[makeQuery(id+"F0.imprint","IMPRINT",EDGE,{"disambiguationData":[TD([[subQ2,-1.0]])],"derivedFrom":subQ1}),1.0]])]});}
            var Q329;
            {var subQ0=sQuery(id+"F0.wireOp",EDGE,"E21");var subQ1=sQuery(id+"F0.wireOp",EDGE,"E3");var subQ2=makeQuery(id+"F0.imprint","INTERSECT",VERTEX,{"derivedFrom":[subQ1,subQ0]});Q329=makeQuery(id+"F0.imprint","IMPRINT",FACE,{"disambiguationData":[TD([[makeQuery(id+"F0.imprint","IMPRINT",EDGE,{"disambiguationData":[TD([[subQ2,-1.0]])],"derivedFrom":subQ1}),1.0]])]});}
            var Q330;
            {var subQ0=sQuery(id+"F0.wireOp",EDGE,"E19");var subQ1=sQuery(id+"F0.wireOp",EDGE,"E3");var subQ2=makeQuery(id+"F0.imprint","INTERSECT",VERTEX,{"derivedFrom":[subQ1,subQ0]});Q330=makeQuery(id+"F0.imprint","IMPRINT",FACE,{"disambiguationData":[TD([[makeQuery(id+"F0.imprint","IMPRINT",EDGE,{"disambiguationData":[TD([[subQ2,-1.0]])],"derivedFrom":subQ1}),1.0]])]});}
            var Q331;
            {var subQ0=sQuery(id+"F0.wireOp",EDGE,"E26");var subQ1=sQuery(id+"F0.wireOp",EDGE,"E4");var subQ2=makeQuery(id+"F0.imprint","INTERSECT",VERTEX,{"derivedFrom":[subQ1,subQ0]});Q331=makeQuery(id+"F0.imprint","IMPRINT",FACE,{"disambiguationData":[TD([[makeQuery(id+"F0.imprint","IMPRINT",EDGE,{"disambiguationData":[TD([[subQ2,-1.0]])],"derivedFrom":subQ1}),1.0]])]});}
            var Q332;
            {var subQ0=sQuery(id+"F0.wireOp",EDGE,"E26");var subQ1=sQuery(id+"F0.wireOp",EDGE,"E3");var subQ2=makeQuery(id+"F0.imprint","INTERSECT",VERTEX,{"derivedFrom":[subQ1,subQ0]});Q332=makeQuery(id+"F0.imprint","IMPRINT",FACE,{"disambiguationData":[TD([[makeQuery(id+"F0.imprint","IMPRINT",EDGE,{"disambiguationData":[TD([[subQ2,-1.0]])],"derivedFrom":subQ1}),1.0]])]});}
            var Q333;
            {var subQ0=sQuery(id+"F0.wireOp",EDGE,"E26");var subQ1=sQuery(id+"F0.wireOp",EDGE,"E2");var subQ2=makeQuery(id+"F0.imprint","INTERSECT",VERTEX,{"derivedFrom":[subQ1,subQ0]});Q333=makeQuery(id+"F0.imprint","IMPRINT",FACE,{"disambiguationData":[TD([[makeQuery(id+"F0.imprint","IMPRINT",EDGE,{"disambiguationData":[TD([[subQ2,-1.0]])],"derivedFrom":subQ1}),1.0]])]});}
            var Q334;
            {var subQ0=sQuery(id+"F0.wireOp",EDGE,"E25");var subQ1=sQuery(id+"F0.wireOp",EDGE,"E3");var subQ2=makeQuery(id+"F0.imprint","INTERSECT",VERTEX,{"derivedFrom":[subQ1,subQ0]});Q334=makeQuery(id+"F0.imprint","IMPRINT",FACE,{"disambiguationData":[TD([[makeQuery(id+"F0.imprint","IMPRINT",EDGE,{"disambiguationData":[TD([[subQ2,-1.0]])],"derivedFrom":subQ1}),1.0]])]});}
            var Q335;
            {var subQ0=sQuery(id+"F0.wireOp",EDGE,"E25");var subQ1=sQuery(id+"F0.wireOp",EDGE,"E4");var subQ2=makeQuery(id+"F0.imprint","INTERSECT",VERTEX,{"derivedFrom":[subQ1,subQ0]});Q335=makeQuery(id+"F0.imprint","IMPRINT",FACE,{"disambiguationData":[TD([[makeQuery(id+"F0.imprint","IMPRINT",EDGE,{"disambiguationData":[TD([[subQ2,-1.0]])],"derivedFrom":subQ1}),1.0]])]});}
            var Q336;
            {var subQ0=sQuery(id+"F0.wireOp",EDGE,"E25");var subQ1=sQuery(id+"F0.wireOp",EDGE,"E2");var subQ2=makeQuery(id+"F0.imprint","INTERSECT",VERTEX,{"derivedFrom":[subQ1,subQ0]});Q336=makeQuery(id+"F0.imprint","IMPRINT",FACE,{"disambiguationData":[TD([[makeQuery(id+"F0.imprint","IMPRINT",EDGE,{"disambiguationData":[TD([[subQ2,-1.0]])],"derivedFrom":subQ1}),1.0]])]});}
            var Q337;
            {var subQ0=sQuery(id+"F0.wireOp",EDGE,"E22");var subQ1=sQuery(id+"F0.wireOp",EDGE,"E2");var subQ2=makeQuery(id+"F0.imprint","INTERSECT",VERTEX,{"derivedFrom":[subQ1,subQ0]});Q337=makeQuery(id+"F0.imprint","IMPRINT",FACE,{"disambiguationData":[TD([[makeQuery(id+"F0.imprint","IMPRINT",EDGE,{"disambiguationData":[TD([[subQ2,-1.0]])],"derivedFrom":subQ1}),1.0]])]});}
            var Q338;
            {var subQ0=sQuery(id+"F0.wireOp",EDGE,"E22");var subQ1=sQuery(id+"F0.wireOp",EDGE,"E3");var subQ2=makeQuery(id+"F0.imprint","INTERSECT",VERTEX,{"derivedFrom":[subQ1,subQ0]});Q338=makeQuery(id+"F0.imprint","IMPRINT",FACE,{"disambiguationData":[TD([[makeQuery(id+"F0.imprint","IMPRINT",EDGE,{"disambiguationData":[TD([[subQ2,-1.0]])],"derivedFrom":subQ1}),1.0]])]});}
            var Q339;
            {var subQ0=sQuery(id+"F0.wireOp",EDGE,"E22");var subQ1=sQuery(id+"F0.wireOp",EDGE,"E4");var subQ2=makeQuery(id+"F0.imprint","INTERSECT",VERTEX,{"derivedFrom":[subQ1,subQ0]});Q339=makeQuery(id+"F0.imprint","IMPRINT",FACE,{"disambiguationData":[TD([[makeQuery(id+"F0.imprint","IMPRINT",EDGE,{"disambiguationData":[TD([[subQ2,-1.0]])],"derivedFrom":subQ1}),1.0]])]});}
            var Q340;
            {var subQ0=sQuery(id+"F0.wireOp",EDGE,"E23");var subQ1=sQuery(id+"F0.wireOp",EDGE,"E2");var subQ2=makeQuery(id+"F0.imprint","INTERSECT",VERTEX,{"derivedFrom":[subQ1,subQ0]});Q340=makeQuery(id+"F0.imprint","IMPRINT",FACE,{"disambiguationData":[TD([[makeQuery(id+"F0.imprint","IMPRINT",EDGE,{"disambiguationData":[TD([[subQ2,-1.0]])],"derivedFrom":subQ1}),1.0]])]});}
            var Q341;
            {var subQ0=sQuery(id+"F0.wireOp",EDGE,"E23");var subQ1=sQuery(id+"F0.wireOp",EDGE,"E3");var subQ2=makeQuery(id+"F0.imprint","INTERSECT",VERTEX,{"derivedFrom":[subQ1,subQ0]});Q341=makeQuery(id+"F0.imprint","IMPRINT",FACE,{"disambiguationData":[TD([[makeQuery(id+"F0.imprint","IMPRINT",EDGE,{"disambiguationData":[TD([[subQ2,-1.0]])],"derivedFrom":subQ1}),1.0]])]});}
            var Q342;
            {var subQ0=sQuery(id+"F0.wireOp",EDGE,"E23");var subQ1=sQuery(id+"F0.wireOp",EDGE,"E4");var subQ2=makeQuery(id+"F0.imprint","INTERSECT",VERTEX,{"derivedFrom":[subQ1,subQ0]});Q342=makeQuery(id+"F0.imprint","IMPRINT",FACE,{"disambiguationData":[TD([[makeQuery(id+"F0.imprint","IMPRINT",EDGE,{"disambiguationData":[TD([[subQ2,-1.0]])],"derivedFrom":subQ1}),1.0]])]});}
            var Q343;
            {var subQ0=sQuery(id+"F0.wireOp",EDGE,"E24");var subQ1=sQuery(id+"F0.wireOp",EDGE,"E2");var subQ2=makeQuery(id+"F0.imprint","INTERSECT",VERTEX,{"derivedFrom":[subQ1,subQ0]});Q343=makeQuery(id+"F0.imprint","IMPRINT",FACE,{"disambiguationData":[TD([[makeQuery(id+"F0.imprint","IMPRINT",EDGE,{"disambiguationData":[TD([[subQ2,-1.0]])],"derivedFrom":subQ1}),1.0]])]});}
            var Q344;
            {var subQ0=sQuery(id+"F0.wireOp",EDGE,"E24");var subQ1=sQuery(id+"F0.wireOp",EDGE,"E3");var subQ2=makeQuery(id+"F0.imprint","INTERSECT",VERTEX,{"derivedFrom":[subQ1,subQ0]});Q344=makeQuery(id+"F0.imprint","IMPRINT",FACE,{"disambiguationData":[TD([[makeQuery(id+"F0.imprint","IMPRINT",EDGE,{"disambiguationData":[TD([[subQ2,-1.0]])],"derivedFrom":subQ1}),1.0]])]});}
            var Q345;
            {var subQ0=sQuery(id+"F0.wireOp",EDGE,"E24");var subQ1=sQuery(id+"F0.wireOp",EDGE,"E4");var subQ2=makeQuery(id+"F0.imprint","INTERSECT",VERTEX,{"derivedFrom":[subQ1,subQ0]});Q345=makeQuery(id+"F0.imprint","IMPRINT",FACE,{"disambiguationData":[TD([[makeQuery(id+"F0.imprint","IMPRINT",EDGE,{"disambiguationData":[TD([[subQ2,-1.0]])],"derivedFrom":subQ1}),1.0]])]});}
            var Q346;
            {var subQ0=sQuery(id+"F0.wireOp",EDGE,"E22");var subQ1=sQuery(id+"F0.wireOp",EDGE,"E8");var subQ2=makeQuery(id+"F0.imprint","INTERSECT",VERTEX,{"derivedFrom":[subQ1,subQ0]});Q346=makeQuery(id+"F0.imprint","IMPRINT",FACE,{"disambiguationData":[TD([[makeQuery(id+"F0.imprint","IMPRINT",EDGE,{"disambiguationData":[TD([[subQ2,-1.0]])],"derivedFrom":subQ1}),1.0]])]});}
            var Q347;
            {var subQ0=sQuery(id+"F0.wireOp",EDGE,"E22");var subQ1=sQuery(id+"F0.wireOp",EDGE,"E9");var subQ2=makeQuery(id+"F0.imprint","INTERSECT",VERTEX,{"derivedFrom":[subQ1,subQ0]});Q347=makeQuery(id+"F0.imprint","IMPRINT",FACE,{"disambiguationData":[TD([[makeQuery(id+"F0.imprint","IMPRINT",EDGE,{"disambiguationData":[TD([[subQ2,-1.0]])],"derivedFrom":subQ1}),1.0]])]});}
            var Q348;
            {var subQ0=sQuery(id+"F0.wireOp",EDGE,"E22");var subQ1=sQuery(id+"F0.wireOp",EDGE,"E10");var subQ2=makeQuery(id+"F0.imprint","INTERSECT",VERTEX,{"derivedFrom":[subQ1,subQ0]});Q348=makeQuery(id+"F0.imprint","IMPRINT",FACE,{"disambiguationData":[TD([[makeQuery(id+"F0.imprint","IMPRINT",EDGE,{"disambiguationData":[TD([[subQ2,-1.0]])],"derivedFrom":subQ1}),1.0]])]});}
            var Q349;
            {var subQ0=sQuery(id+"F0.wireOp",EDGE,"E23");var subQ1=sQuery(id+"F0.wireOp",EDGE,"E8");var subQ2=makeQuery(id+"F0.imprint","INTERSECT",VERTEX,{"derivedFrom":[subQ1,subQ0]});Q349=makeQuery(id+"F0.imprint","IMPRINT",FACE,{"disambiguationData":[TD([[makeQuery(id+"F0.imprint","IMPRINT",EDGE,{"disambiguationData":[TD([[subQ2,-1.0]])],"derivedFrom":subQ1}),1.0]])]});}
            var Q350;
            {var subQ0=sQuery(id+"F0.wireOp",EDGE,"E23");var subQ1=sQuery(id+"F0.wireOp",EDGE,"E9");var subQ2=makeQuery(id+"F0.imprint","INTERSECT",VERTEX,{"derivedFrom":[subQ1,subQ0]});Q350=makeQuery(id+"F0.imprint","IMPRINT",FACE,{"disambiguationData":[TD([[makeQuery(id+"F0.imprint","IMPRINT",EDGE,{"disambiguationData":[TD([[subQ2,-1.0]])],"derivedFrom":subQ1}),1.0]])]});}
            var Q351;
            {var subQ0=sQuery(id+"F0.wireOp",EDGE,"E23");var subQ1=sQuery(id+"F0.wireOp",EDGE,"E10");var subQ2=makeQuery(id+"F0.imprint","INTERSECT",VERTEX,{"derivedFrom":[subQ1,subQ0]});Q351=makeQuery(id+"F0.imprint","IMPRINT",FACE,{"disambiguationData":[TD([[makeQuery(id+"F0.imprint","IMPRINT",EDGE,{"disambiguationData":[TD([[subQ2,-1.0]])],"derivedFrom":subQ1}),1.0]])]});}
            extrude(context, id + "F1", {"entities" : qUnion([Q0, Q1, Q2, Q3, Q4, Q5, Q6, Q7, Q8, Q9, Q10, Q11, Q12, Q13, Q14, Q15, Q16, Q17, Q18, Q19, Q20, Q21, Q22, Q23, Q24, Q25, Q26, Q27, Q28, Q29, Q30, Q31, Q32, Q33, Q34, Q35, Q36, Q37, Q38, Q39, Q40, Q41, Q42, Q43, Q44, Q45, Q46, Q47, Q48, Q49, Q50, Q51, Q52, Q53, Q54, Q55, Q56, Q57, Q58, Q59, Q60, Q61, Q62, Q63, Q64, Q65, Q66, Q67, Q68, Q69, Q70, Q71, Q72, Q73, Q74, Q75, Q76, Q77, Q78, Q79, Q80, Q81, Q82, Q83, Q84, Q85, Q86, Q87, Q88, Q89, Q90, Q91, Q92, Q93, Q94, Q95, Q96, Q97, Q98, Q99, Q100, Q101, Q102, Q103, Q104, Q105, Q106, Q107, Q108, Q109, Q110, Q111, Q112, Q113, Q114, Q115, Q116, Q117, Q118, Q119, Q120, Q121, Q122, Q123, Q124, Q125, Q126, Q127, Q128, Q129, Q130, Q131, Q132, Q133, Q134, Q135, Q136, Q137, Q138, Q139, Q140, Q141, Q142, Q143, Q144, Q145, Q146, Q147, Q148, Q149, Q150, Q151, Q152, Q153, Q154, Q155, Q156, Q157, Q158, Q159, Q160, Q161, Q162, Q163, Q164, Q165, Q166, Q167, Q168, Q169, Q170, Q171, Q172, Q173, Q174, Q175, Q176, Q177, Q178, Q179, Q180, Q181, Q182, Q183, Q184, Q185, Q186, Q187, Q188, Q189, Q190, Q191, Q192, Q193, Q194, Q195, Q196, Q197, Q198, Q199, Q200, Q201, Q202, Q203, Q204, Q205, Q206, Q207, Q208, Q209, Q210, Q211, Q212, Q213, Q214, Q215, Q216, Q217, Q218, Q219, Q220, Q221, Q222, Q223, Q224, Q225, Q226, Q227, Q228, Q229, Q230, Q231, Q232, Q233, Q234, Q235, Q236, Q237, Q238, Q239, Q240, Q241, Q242, Q243, Q244, Q245, Q246, Q247, Q248, Q249, Q250, Q251, Q252, Q253, Q254, Q255, Q256, Q257, Q258, Q259, Q260, Q261, Q262, Q263, Q264, Q265, Q266, Q267, Q268, Q269, Q270, Q271, Q272, Q273, Q274, Q275, Q276, Q277, Q278, Q279, Q280, Q281, Q282, Q283, Q284, Q285, Q286, Q287, Q288, Q289, Q290, Q291, Q292, Q293, Q294, Q295, Q296, Q297, Q298, Q299, Q300, Q301, Q302, Q303, Q304, Q305, Q306, Q307, Q308, Q309, Q310, Q311, Q312, Q313, Q314, Q315, Q316, Q317, Q318, Q319, Q320, Q321, Q322, Q323, Q324, Q325, Q326, Q327, Q328, Q329, Q330, Q331, Q332, Q333, Q334, Q335, Q336, Q337, Q338, Q339, Q340, Q341, Q342, Q343, Q344, Q345, Q346, Q347, Q348, Q349, Q350, Q351]), "depth" : 4 * mm, "offsetDistance" : 25 * mm});
        }
        {
            var Q0;
            Q0=makeQuery(id+"F1.opExtrude","SWEPT_FACE",FACE,{"disambiguationData":[OSD([sQuery(id+"F0.wireOp",EDGE,"E0.left")])]});
            var Q1;
            Q1=makeQuery(id+"F1.opExtrude","SWEPT_FACE",FACE,{"disambiguationData":[OSD([sQuery(id+"F0.wireOp",EDGE,"E0.top")])]});
            var Q2;
            Q2=makeQuery(id+"F1.opExtrude","SWEPT_FACE",FACE,{"disambiguationData":[OSD([sQuery(id+"F0.wireOp",EDGE,"E0.right")])]});
            var Q3;
            Q3=makeQuery(id+"F1.opExtrude","SWEPT_FACE",FACE,{"disambiguationData":[OSD([sQuery(id+"F0.wireOp",EDGE,"E0.bottom")])]});
            fillet(context, id + "F2", {"entities" : qUnion([Q0, Q1, Q2, Q3]), "radius" : 0.1 * mm, "tangentPropagation" : true, "allowEdgeOverflow" : false});
        }
    });
